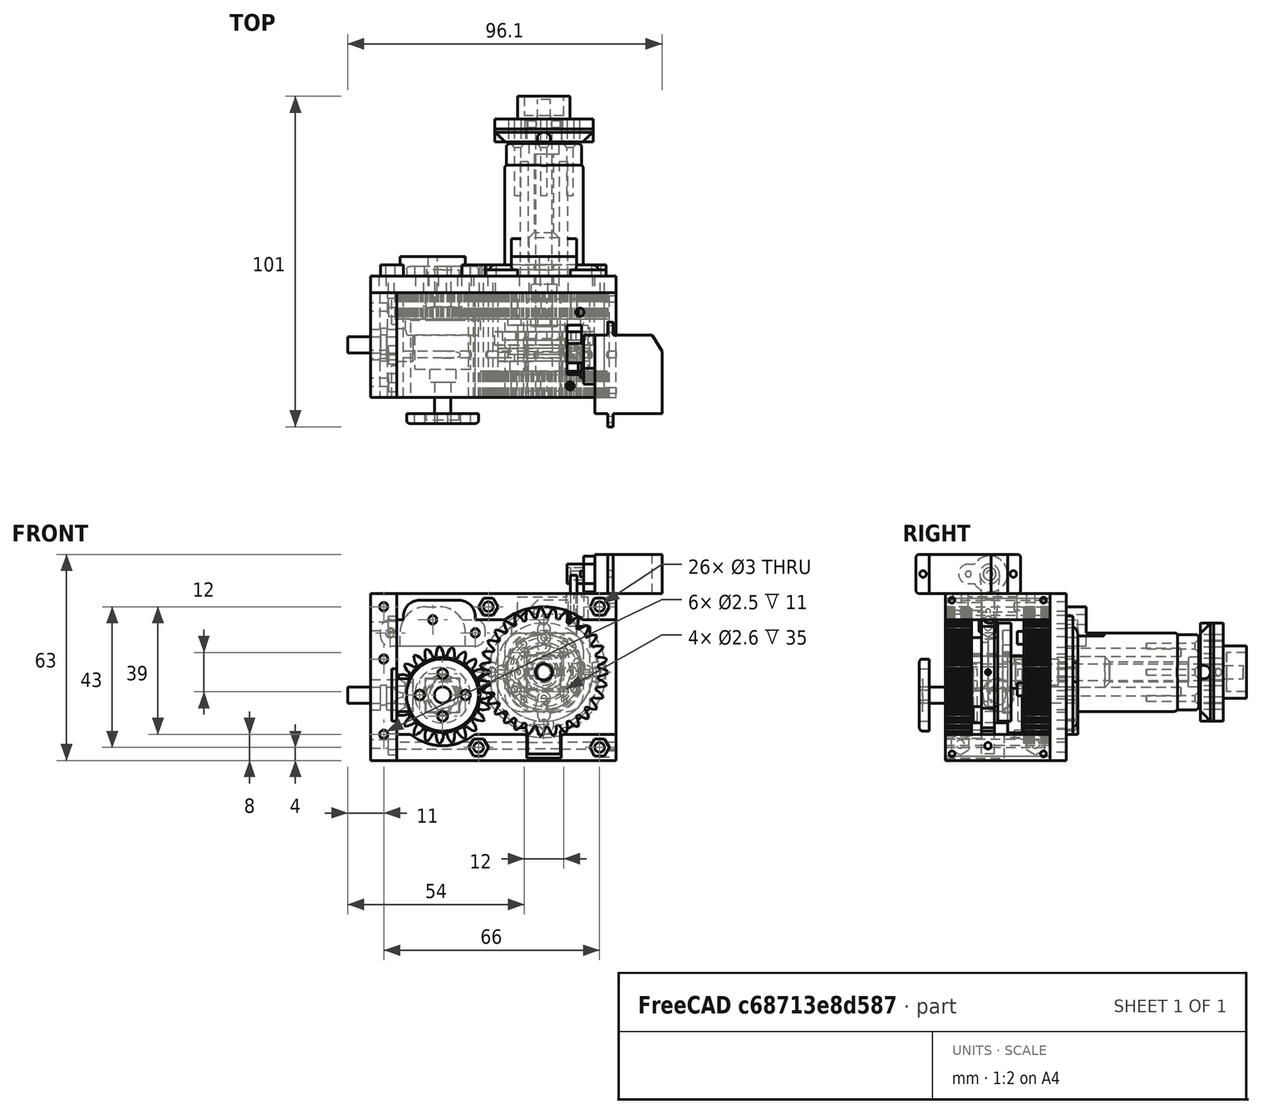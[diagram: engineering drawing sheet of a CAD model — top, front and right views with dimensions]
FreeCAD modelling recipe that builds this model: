
FCSTD DOCUMENT  (FreeCAD 0.20R)
Label: axles_00
License: Other
LicenseURL: https://www.gnu.org/licenses/gpl-3.0.en.html
objects: Part::Cylinder×477, Part::MultiFuse×208, Part::Cut×171, Part::Feature×154, Part::Box×150, Part::Chamfer×52, Part::Fillet×51, App::DocumentObjectGroup×23, Part::Part2DObjectPython×15, Part::Cone×7, Part::RegularPolygon×6, Part::Extrusion×6, Part::Compound×3, Part::Sphere×2, Mesh::Feature×2, Part::Mirroring×1
note: 1303 computed .brp shape members not serialized (recipe doc carries the construction recipe); baked Part::Feature solids carry a one-line shape summary decoded from their .brp

FEATURE [Part::Feature] Fusion017003004005003  label="rear-wheel-left"
  Placement = pos=(75,56,46) rot=(0,0,1;0rad)
  shape: bbox 96.33 x 28 x 96.33 mm, 456 faces (baked)
FEATURE [Part::Cylinder] Cylinder
  Angle = 360
  AttacherType = Attacher::AttachEngine3D
  FirstAngle = 0
  Height = 15
  Placement = pos=(0,0,-1) rot=(0,0,1;0rad)
  Radius = 8.5
  SecondAngle = 0
FEATURE [Part::Cylinder] Cylinder001
  Angle = 360
  AttacherType = Attacher::AttachEngine3D
  FirstAngle = 0
  Height = 4.5
  Placement = pos=(0,0,-1) rot=(0,0,1;0rad)
  Radius = 11.5
  SecondAngle = 0
FEATURE [Part::Cylinder] Cylinder002
  Angle = 360
  AttacherType = Attacher::AttachEngine3D
  FirstAngle = 0
  Height = 23
  Placement = pos=(0,0,-5) rot=(0,0,1;0rad)
  Radius = 4
  SecondAngle = 0
FEATURE [Part::Cylinder] Cylinder203
  Angle = 360
  AttacherType = Attacher::AttachEngine3D
  FirstAngle = 0
  Height = 5
  Placement = pos=(15,0,0) rot=(0,1,0;1.5708rad)
  Radius = 5
  SecondAngle = 0
FEATURE [Part::Cylinder] Cylinder204
  Angle = 360
  AttacherType = Attacher::AttachEngine3D
  FirstAngle = 0
  Height = 20
  Placement = pos=(0,0,0) rot=(0,1,0;1.5708rad)
  Radius = 2.5
  SecondAngle = 0
FEATURE [Part::MultiFuse] Fusion  label="differential"
  Placement = pos=(7.5,48,7.5) rot=(-1,0,0;1.5708rad)
  Refine = true
  Shapes = -> [Cylinder,Cylinder001,Cylinder002]
FEATURE [Part::MultiFuse] Fusion040  label="pinion"
  Placement = pos=(-21.5,54.5,7.5) rot=(0,0,1;0rad)
  Refine = true
  Shapes = -> [Cylinder204,Cylinder203]
FEATURE [Part::MultiFuse] Fusion041  label="differential+pinion"
  Placement = pos=(82.5,-54.5,53.5) rot=(0,1,0;3.14159rad)
  Refine = true
  Shapes = -> [Fusion,Fusion040]
FEATURE [Part::Part2DObjectPython] Line013  label="rear-wheels-axle-path"  # Draft 2D object (typed FeaturePython)
  Closed = true
  End = (75,75,46)
  FilletRadius = 0
  MapMode = 5
  Placement = pos=(75,-70,46) rot=(0,0,1;0rad)
  Points = (2) [(0,-5,0),(0,145,0)]
  Start = (75,-75,46)
FEATURE [Part::Box] Box153  label="Cube"
  AttacherType = Attacher::AttachEngine3D
  Height = 28
  Length = 24
  Placement = pos=(63,-20,32) rot=(0,0,1;0rad)
  Width = 40
FEATURE [Part::Cylinder] Cylinder406  label="Cylinder"
  Angle = 360
  AttacherType = Attacher::AttachEngine3D
  FirstAngle = 0
  Height = 48
  Placement = pos=(75,48,46) rot=(1,0,0;1.5708rad)
  Radius = 7.5
  SecondAngle = 0
FEATURE [Part::Cylinder] Cylinder407  label="Cylinder"
  Angle = 360
  AttacherType = Attacher::AttachEngine3D
  FirstAngle = 0
  Height = 39
  Placement = pos=(58,0,46) rot=(0,1,0;1.5708rad)
  Radius = 8.5
  SecondAngle = 0
FEATURE [Part::Feature] Compound001  label="joint-STEEL"
  Placement = pos=(0,-3,0) rot=(0,0,1;0rad)
  shape: bbox 11 x 24 x 40 mm, 54 faces (baked)
FEATURE [Part::Cylinder] Cylinder415  label="Cylinder"
  Angle = 360
  AttacherType = Attacher::AttachEngine3D
  FirstAngle = 0
  Height = 4
  Placement = pos=(75,69,46) rot=(1,0,0;1.5708rad)
  Radius = 7.5
  SecondAngle = 0
FEATURE [Part::Cylinder] Cylinder416  label="Cylinder"
  Angle = 360
  AttacherType = Attacher::AttachEngine3D
  FirstAngle = 0
  Height = 4
  Placement = pos=(75,69,46) rot=(1,0,0;1.5708rad)
  Radius = 5
  SecondAngle = 0
FEATURE [Part::Cut] Cut004026018020025012002  label="BEARING-10x15x4-6700"
  Base = -> Cylinder415
  Refine = true
  Tool = -> Cylinder416
FEATURE [Part::Feature] Fusion041001  label="differential+pinion"
  Placement = pos=(82.5,-54.5,53.5) rot=(0,1,0;3.14159rad)
  shape: bbox 40.5 x 23 x 23 mm, 14 faces (baked)
FEATURE [Part::Box] Box197  label="Cube197"
  AttacherType = Attacher::AttachEngine3D
  Height = 9.4
  Length = 9.8
  Placement = pos=(2.4,22.8,2.8) rot=(0,0,1;0rad)
  Width = 3.4
FEATURE [Part::Box] Box198  label="Cube198"
  AttacherType = Attacher::AttachEngine3D
  Height = 9.4
  Length = 9.8
  Placement = pos=(2.4,22.8,2.8) rot=(0,0,1;0rad)
  Width = 3.4
FEATURE [Part::Box] Box250  label="Cube250"
  AttacherType = Attacher::AttachEngine3D
  Height = 12.4
  Length = 12.8
  Placement = pos=(1.1,21.9,1.3) rot=(0,0,1;0rad)
  Width = 3.6
FEATURE [Part::Box] Box251  label="Cube251"
  AttacherType = Attacher::AttachEngine3D
  Height = 12.4
  Length = 12.8
  Placement = pos=(1.1,21.5,1.3) rot=(0,0,1;0rad)
  Width = 3.6
FEATURE [Part::Chamfer] Chamfer218  label="bearing_shape_031"
  Base = -> Box197
  Edges = 4 edges r=2.5: [Edge2,Edge4,Edge6,Edge8]
  Placement = pos=(-7.5,33.5,-7.5) rot=(0,0,1;0rad)
FEATURE [Part::Chamfer] Chamfer219  label="bearing_shape_032"
  Base = -> Box198
  Edges = 4 edges r=2.5: [Edge2,Edge4,Edge6,Edge8]
  Placement = pos=(-7.5,103.5,-7.5) rot=(0,0,1;0rad)
FEATURE [Part::Chamfer] Chamfer228008  label="bearing_shape_037"
  Base = -> Box251
  Edges = 4 edges r=3: [Edge2,Edge4,Edge6,Edge8]
  Placement = pos=(-7.5,79.5,-7.5) rot=(0,0,1;0rad)
FEATURE [Part::Chamfer] Chamfer228009  label="bearing_shape_038"
  Base = -> Box250
  Edges = 4 edges r=3: [Edge2,Edge4,Edge6,Edge8]
  Placement = pos=(-7.5,59.5,-7.5) rot=(0,0,1;0rad)
FEATURE [Part::Cylinder] Cylinder685
  Angle = 360
  AttacherType = Attacher::AttachEngine3D
  FirstAngle = 0
  Height = 16
  Placement = pos=(0,85,0) rot=(-1,0,0;1.5708rad)
  Radius = 12
  SecondAngle = 0
FEATURE [Part::Cylinder] Cylinder686
  Angle = 360
  AttacherType = Attacher::AttachEngine3D
  FirstAngle = 0
  Height = 5.5
  Placement = pos=(16,52,7.5) rot=(0,1,0;1.5708rad)
  Radius = 6
  SecondAngle = 0
FEATURE [Part::Cylinder] Cylinder687
  Angle = 360
  AttacherType = Attacher::AttachEngine3D
  FirstAngle = 0
  Height = 3
  Placement = pos=(21.5,52,7.5) rot=(0,1,0;1.5708rad)
  Radius = 4.7
  SecondAngle = 0
FEATURE [Part::Cylinder] Cylinder688
  Angle = 360
  AttacherType = Attacher::AttachEngine3D
  FirstAngle = 0
  Height = 3
  Placement = pos=(26.5,52,7.5) rot=(0,1,0;1.5708rad)
  Radius = 4.7
  SecondAngle = 0
FEATURE [Part::Cylinder] Cylinder689
  Angle = 360
  AttacherType = Attacher::AttachEngine3D
  FirstAngle = 0
  Height = 8
  Placement = pos=(21.5,52,7.5) rot=(0,1,0;1.5708rad)
  Radius = 3.2
  SecondAngle = 0
FEATURE [Part::Cylinder] Cylinder690
  Angle = 360
  AttacherType = Attacher::AttachEngine3D
  FirstAngle = 0
  Height = 3
  Placement = pos=(0,24,0) rot=(-1,0,0;1.5708rad)
  Radius = 4.6
  SecondAngle = 0
FEATURE [Part::Cylinder] Cylinder691
  Angle = 360
  AttacherType = Attacher::AttachEngine3D
  FirstAngle = 0
  Height = 3
  Placement = pos=(0,159,0) rot=(-1,0,0;1.5708rad)
  Radius = 4.6
  SecondAngle = 0
FEATURE [Part::Cylinder] Cylinder692
  Angle = 360
  AttacherType = Attacher::AttachEngine3D
  FirstAngle = 0
  Height = 138
  Placement = pos=(0,24,0) rot=(-1,0,0;1.5708rad)
  Radius = 3
  SecondAngle = 0
FEATURE [Part::MultiFuse] Fusion088026007031024007017  label="pinion-bearings-carving003"
  Placement = pos=(7.5,41,7.5) rot=(0,1,0;3.14159rad)
  Refine = true
  Shapes = -> [Cylinder686,Cylinder688,Cylinder689,Cylinder687]
FEATURE [Part::MultiFuse] Fusion088026007031024007008004058  label="inner-carving-rear"
  Placement = pos=(75,-93,46) rot=(0,1,0;3.14159rad)
  Refine = true
  Shapes = -> [Chamfer219,Chamfer218,Cylinder692,Fusion088026007031024007017,Chamfer228009,Chamfer228008,Cylinder685,Cylinder690,Cylinder691]
FEATURE [Part::Cylinder] Cylinder693  label="Cylinder"
  Angle = 360
  AttacherType = Attacher::AttachEngine3D
  FirstAngle = 0
  Height = 4
  Placement = pos=(75,69,46) rot=(1,0,0;1.5708rad)
  Radius = 11.5
  SecondAngle = 0
FEATURE [Part::Cylinder] Cylinder694  label="Cylinder"
  Angle = 360
  AttacherType = Attacher::AttachEngine3D
  FirstAngle = 0
  Height = 4
  Placement = pos=(75,69,46) rot=(1,0,0;1.5708rad)
  Radius = 8.5
  SecondAngle = 0
FEATURE [Part::Cut] Cut176013009033007019019008010045003002004008006021005002  label="BEARING-17x23x4-6703"
  Base = -> Cylinder693
  Refine = true
  Tool = -> Cylinder694
FEATURE [Part::Cylinder] Cylinder695  label="Cylinder"
  Angle = 360
  AttacherType = Attacher::AttachEngine3D
  FirstAngle = 0
  Height = 4
  Placement = pos=(75,69,46) rot=(1,0,0;1.5708rad)
  Radius = 13.5
  SecondAngle = 0
FEATURE [Part::Cylinder] Cylinder696  label="Cylinder"
  Angle = 360
  AttacherType = Attacher::AttachEngine3D
  FirstAngle = 0
  Height = 4
  Placement = pos=(75,69,46) rot=(1,0,0;1.5708rad)
  Radius = 10
  SecondAngle = 0
FEATURE [Part::Cut] Cut176013009033007019019008010045003002004008006021005003  label="BEARING-20x27x4-6704"
  Base = -> Cylinder695
  Refine = true
  Tool = -> Cylinder696
FEATURE [Part::Cylinder] Cylinder697  label="Cylinder"
  Angle = 360
  AttacherType = Attacher::AttachEngine3D
  FirstAngle = 0
  Height = 3
  Placement = pos=(75,69,46) rot=(1,0,0;1.5708rad)
  Radius = 4.5
  SecondAngle = 0
FEATURE [Part::Cylinder] Cylinder698  label="Cylinder"
  Angle = 360
  AttacherType = Attacher::AttachEngine3D
  FirstAngle = 0
  Height = 3
  Placement = pos=(75,69,46) rot=(1,0,0;1.5708rad)
  Radius = 2.5
  SecondAngle = 0
FEATURE [Part::Cut] Cut176013009033007019019008010045003002004008006021005004  label="BEARING-5x9x3-MR95ZZ"
  Base = -> Cylinder697
  Refine = true
  Tool = -> Cylinder698
FEATURE [Part::Cylinder] Cylinder699  label="Cylinder"
  Angle = 360
  AttacherType = Attacher::AttachEngine3D
  FirstAngle = 0
  Height = 3.5
  Placement = pos=(75,69,46) rot=(1,0,0;1.5708rad)
  Radius = 6
  SecondAngle = 0
FEATURE [Part::Cylinder] Cylinder700  label="Cylinder"
  Angle = 360
  AttacherType = Attacher::AttachEngine3D
  FirstAngle = 0
  Height = 3.5
  Placement = pos=(75,69,46) rot=(1,0,0;1.5708rad)
  Radius = 4
  SecondAngle = 0
FEATURE [Part::Cut] Cut176013009033007019019008010045003002004008006021005005  label="BEARING-8x12x3.5-MR128ZZ"
  Base = -> Cylinder699
  Refine = true
  Tool = -> Cylinder700
FEATURE [Part::Feature] Cut176013009033007019019008010045003002004008006021005004001  label="BEARING-5x9x3-MR95ZZ"
  Placement = pos=(0,-24.5,0) rot=(0,0,1;0rad)
  shape: bbox 9 x 3 x 9 mm, 4 faces (baked)
FEATURE [Part::Feature] Cut176013009033007019019008010045003002004008006021005004003  label="BEARING-5x9x3-MR95ZZ"
  Placement = pos=(0,-110.5,0) rot=(0,0,1;0rad)
  shape: bbox 9 x 3 x 9 mm, 4 faces (baked)
FEATURE [Part::Box] Box305  label="Cube"
  AttacherType = Attacher::AttachEngine3D
  Height = 11
  Length = 2
  Placement = pos=(-1,36,-5.5) rot=(0,0,1;0rad)
  Width = 6
FEATURE [Part::Cylinder] Cylinder828  label="Cylinder"
  Angle = 360
  AttacherType = Attacher::AttachEngine3D
  FirstAngle = 0
  Height = 3.5
  Placement = pos=(0,90,0) rot=(1,0,0;1.5708rad)
  Radius = 2
  SecondAngle = 0
FEATURE [Part::Cylinder] Cylinder830  label="Cylinder"
  Angle = 360
  AttacherType = Attacher::AttachEngine3D
  FirstAngle = 0
  Height = 38
  Placement = pos=(0,86.5,0) rot=(1,0,0;1.5708rad)
  Radius = 2.5
  SecondAngle = 0
FEATURE [Part::Cylinder] Cylinder831  label="Cylinder"
  Angle = 360
  AttacherType = Attacher::AttachEngine3D
  FirstAngle = 0
  Height = 0.5
  Placement = pos=(0,48.5,0) rot=(1,0,0;1.5708rad)
  Radius = 2
  SecondAngle = 0
FEATURE [Part::Cylinder] Cylinder832  label="Cylinder"
  Angle = 360
  AttacherType = Attacher::AttachEngine3D
  FirstAngle = 0
  Height = 2
  Placement = pos=(0,48,0) rot=(1,0,0;1.5708rad)
  Radius = 2.3
  SecondAngle = 0
FEATURE [Part::Cylinder] Cylinder833  label="Cylinder"
  Angle = 360
  AttacherType = Attacher::AttachEngine3D
  FirstAngle = 0
  Height = 6
  Placement = pos=(0,46,0) rot=(1,0,0;1.5708rad)
  Radius = 1.75
  SecondAngle = 0
FEATURE [Part::Cylinder] Cylinder834  label="Cylinder"
  Angle = 360
  AttacherType = Attacher::AttachEngine3D
  FirstAngle = 0
  Height = 11
  Placement = pos=(0,39.5,-5.5) rot=(0,0,1;1.5708rad)
  Radius = 1
  SecondAngle = 0
FEATURE [Part::Cylinder] Cylinder835  label="Cylinder"
  Angle = 360
  AttacherType = Attacher::AttachEngine3D
  FirstAngle = 0
  Height = 7
  Placement = pos=(0,41.5,0) rot=(1,0,0;1.5708rad)
  Radius = 5.5
  SecondAngle = 0
FEATURE [Part::Cylinder] Cylinder836  label="Cylinder"
  Angle = 360
  AttacherType = Attacher::AttachEngine3D
  FirstAngle = 0
  Height = 17
  Placement = pos=(0,41.5,0) rot=(1,0,0;1.5708rad)
  Radius = 2.5
  SecondAngle = 0
FEATURE [Part::Cylinder] Cylinder837  label="Cylinder"
  Angle = 360
  AttacherType = Attacher::AttachEngine3D
  FirstAngle = 0
  Height = 25
  Placement = pos=(0,41.5,0) rot=(1,0,0;1.5708rad)
  Radius = 2
  SecondAngle = 0
FEATURE [Part::Cylinder] Cylinder838  label="Cylinder"
  Angle = 360
  AttacherType = Attacher::AttachEngine3D
  FirstAngle = 0
  Height = 7
  Placement = pos=(0,41.5,0) rot=(1,0,0;1.5708rad)
  Radius = 4
  SecondAngle = 0
FEATURE [Part::MultiFuse] Fusion088026007031024007008004081022015  label="Fusion"
  Refine = true
  Shapes = -> [Cylinder837,Cylinder835,Cylinder836]
FEATURE [Part::Cut] Cut176013009033007019019008010045003002004008006021005009  label="Cut"
  Base = -> Fusion088026007031024007008004081022015
  Refine = true
  Tool = -> Cylinder838
FEATURE [Part::Chamfer] Chamfer228026
  Base = -> Cut176013009033007019019008010045003002004008006021005009
  Edges = 1 edges: [Edge4 r1=1 r2=3]
FEATURE [Part::Cut] Cut176013009033007019019008010045003002004008006021005010  label="wheel-axle-left"
  Base = -> Chamfer228026
  Placement = pos=(75,93,46) rot=(0,0,1;3.14159rad)
  Refine = true
  Tool = -> Box305
FEATURE [Part::Sphere] Sphere
  Angle1 = -90
  Angle2 = 90
  Angle3 = 360
  AttacherType = Attacher::AttachEngine3D
  Placement = pos=(0,39.5,0) rot=(0,0,1;0rad)
  Radius = 3
FEATURE [Part::MultiFuse] Fusion088026007031024007008004081022014  label="axle-shaft-left"
  Placement = pos=(75,93,46) rot=(0,0,1;3.14159rad)
  Refine = true
  Shapes = -> [Cylinder828,Cylinder830,Cylinder832,Cylinder831,Sphere,Cylinder833,Cylinder834]
FEATURE [Part::Part2DObjectPython] Line015  label="rear-axle-steering-point-left"  # Draft 2D object (typed FeaturePython)
  Closed = true
  End = (75,53.5,26)
  FilletRadius = 0
  MapMode = 5
  Placement = pos=(75,-86,42) rot=(0,0,1;0rad)
  Points = (2) [(0,139.5,24),(0,139.5,-16)]
  Start = (75,53.5,66)
FEATURE [Part::Sphere] Sphere001  label="Sphere"
  Angle1 = -90
  Angle2 = 90
  Angle3 = 360
  AttacherType = Attacher::AttachEngine3D
  Placement = pos=(75,54,46) rot=(0,0,1;0rad)
  Radius = 10
FEATURE [Part::MultiFuse] Fusion088026007031024007008004100051009001002  label="Fusion"
  Refine = true
  Shapes = -> [Cylinder406,Sphere001]
FEATURE [Part::Cylinder] Cylinder840  label="Cylinder"
  Angle = 360
  AttacherType = Attacher::AttachEngine3D
  FirstAngle = 0
  Height = 24
  Placement = pos=(75,66,46) rot=(1,0,0;1.5708rad)
  Radius = 6
  SecondAngle = 0
FEATURE [Part::Cylinder] Cylinder841  label="Cylinder"
  Angle = 360
  AttacherType = Attacher::AttachEngine3D
  FirstAngle = 0
  Height = 10
  Placement = pos=(75,66,46) rot=(1,0,0;1.5708rad)
  Radius = 11
  SecondAngle = 0
FEATURE [Part::Box] Box306  label="Cube"
  AttacherType = Attacher::AttachEngine3D
  Height = 14
  Length = 22
  Placement = pos=(56,54,39) rot=(0,0,1;0rad)
  Width = 12
FEATURE [Part::Fillet] Fillet
  Base = -> Box306
  Edges = 2 edges r=6.5: [Edge9,Edge10]
  Placement = pos=(5,-2,0) rot=(0,0,1;0rad)
FEATURE [Part::Cylinder] Cylinder842  label="Cylinder"
  Angle = 360
  AttacherType = Attacher::AttachEngine3D
  FirstAngle = 0
  Height = 15
  Placement = pos=(75,66,46) rot=(1,0,0;1.5708rad)
  Radius = 7
  SecondAngle = 0
FEATURE [Part::MultiFuse] Fusion088026007031024007008004100051009001003  label="Fusion"
  Refine = true
  Shapes = -> [Cylinder842,Cylinder841,Cylinder840]
FEATURE [Part::Cut] Cut176013009033007019019008010045003002004008006021005004004004002  label="Cut"
  Base = -> Fusion088026007031024007008004100051009001002
  Refine = true
  Tool = -> Fusion088026007031024007008004100051009001003
FEATURE [Part::Fillet] Fillet113
  Base = -> Fillet
  Edges = 4 edges r=5: [Edge2,Edge6,Edge11,Edge13]
  Placement = pos=(3,0,0) rot=(0,0,1;0rad)
FEATURE [Part::Cut] Cut176013009033007019019008010045003002004008006021005004004004003  label="Cut"
  Base = -> Cut176013009033007019019008010045003002004008006021005004004004002
  Refine = true
  Tool = -> Fillet113
FEATURE [Part::Box] Box278  label="Cube277"
  AttacherType = Attacher::AttachEngine3D
  Height = 5.4
  Length = 28
  Placement = pos=(-14,24,-13) rot=(0,0,1;0rad)
  Width = 20
FEATURE [Part::Box] Box279  label="Cube278"
  AttacherType = Attacher::AttachEngine3D
  Height = 5.4
  Length = 28
  Placement = pos=(-14,24,7.6) rot=(0,0,1;0rad)
  Width = 20
FEATURE [Part::Box] Box280  label="Cube279"
  AttacherType = Attacher::AttachEngine3D
  Height = 16
  Length = 20
  Placement = pos=(-10,48,-8) rot=(0,0,1;0rad)
  Width = 12
FEATURE [Part::Box] Box284  label="Cube283"
  AttacherType = Attacher::AttachEngine3D
  Height = 4
  Length = 18
  Placement = pos=(12.75,26,-2) rot=(0,0,1;1.26536rad)
  Width = 6
FEATURE [Part::Box] Box289  label="Cube288"
  AttacherType = Attacher::AttachEngine3D
  Height = 4
  Length = 7.2
  Placement = pos=(5.8,24,-2) rot=(0,0,1;0rad)
  Width = 12
FEATURE [Part::Box] Box290  label="Cube289"
  AttacherType = Attacher::AttachEngine3D
  Height = 4.4
  Length = 7.5
  Placement = pos=(5.7,24,-2.2) rot=(0,0,1;0rad)
  Width = 12
FEATURE [Part::Feature] Cut176013009033007019019008010045003002004002001  label="steering-knukle-body-left001"
  Placement = pos=(0,0.5,0) rot=(0,0,1;0rad)
  shape: bbox 25.81 x 12 x 15.2 mm, 30 faces (baked)
FEATURE [Part::Cylinder] Cylinder749
  Angle = 360
  AttacherType = Attacher::AttachEngine3D
  FirstAngle = 0
  Height = 6
  Placement = pos=(14.35,41,-3) rot=(0,0,1;0rad)
  Radius = 1.25
  SecondAngle = 0
FEATURE [Part::Cylinder] Cylinder752
  Angle = 360
  AttacherType = Attacher::AttachEngine3D
  FirstAngle = 0
  Height = 12
  Placement = pos=(0,24,0) rot=(-1,0,0;1.5708rad)
  Radius = 13
  SecondAngle = 0
FEATURE [Part::Cylinder] Cylinder753
  Angle = 360
  AttacherType = Attacher::AttachEngine3D
  FirstAngle = 0
  Height = 3.2
  Placement = pos=(0,24,0) rot=(-1,0,0;1.5708rad)
  Radius = 4.7
  SecondAngle = 0
FEATURE [Part::Cylinder] Cylinder754
  Angle = 360
  AttacherType = Attacher::AttachEngine3D
  FirstAngle = 0
  Height = 8
  Placement = pos=(0,34,0) rot=(-1,0,0;1.5708rad)
  Radius = 6.1
  SecondAngle = 0
FEATURE [Part::Cylinder] Cylinder755
  Angle = 360
  AttacherType = Attacher::AttachEngine3D
  FirstAngle = 0
  Height = 3.2
  Placement = pos=(0,30.8,0) rot=(-1,0,0;1.5708rad)
  Radius = 4.7
  SecondAngle = 0
FEATURE [Part::Cylinder] Cylinder756
  Angle = 360
  AttacherType = Attacher::AttachEngine3D
  FirstAngle = 0
  Height = 4
  Placement = pos=(0,27,0) rot=(-1,0,0;1.5708rad)
  Radius = 3.5
  SecondAngle = 0
FEATURE [Part::Cylinder] Cylinder788
  Angle = 360
  AttacherType = Attacher::AttachEngine3D
  FirstAngle = 0
  Height = 37
  Placement = pos=(-8,27.5,-19) rot=(0,0,1;0rad)
  Radius = 1.05
  SecondAngle = 0
FEATURE [Part::Cylinder] Cylinder789
  Angle = 360
  AttacherType = Attacher::AttachEngine3D
  FirstAngle = 0
  Height = 37
  Placement = pos=(8,33,-19) rot=(0,0,1;0rad)
  Radius = 1.05
  SecondAngle = 0
FEATURE [Part::Cylinder] Cylinder790
  Angle = 360
  AttacherType = Attacher::AttachEngine3D
  FirstAngle = 0
  Height = 37
  Placement = pos=(-8,33,-19) rot=(0,0,1;0rad)
  Radius = 1.05
  SecondAngle = 0
FEATURE [Part::Cylinder] Cylinder791
  Angle = 360
  AttacherType = Attacher::AttachEngine3D
  FirstAngle = 0
  Height = 37
  Placement = pos=(8,27.5,-19) rot=(0,0,1;0rad)
  Radius = 1.05
  SecondAngle = 0
FEATURE [Part::Cylinder] Cylinder792
  Angle = 360
  AttacherType = Attacher::AttachEngine3D
  FirstAngle = 0
  Height = 8
  Placement = pos=(0,34,0) rot=(-1,0,0;1.5708rad)
  Radius = 6.1
  SecondAngle = 0
FEATURE [Part::Cylinder] Cylinder810
  Angle = 360
  AttacherType = Attacher::AttachEngine3D
  FirstAngle = 0
  Height = 15.2
  Placement = pos=(-8,27.5,-7.6) rot=(0,0,1;0rad)
  Radius = 1.6
  SecondAngle = 0
FEATURE [Part::Cylinder] Cylinder812
  Angle = 360
  AttacherType = Attacher::AttachEngine3D
  FirstAngle = 0
  Height = 15.2
  Placement = pos=(-8,33,-7.6) rot=(0,0,1;0rad)
  Radius = 1.6
  SecondAngle = 0
FEATURE [Part::Cylinder] Cylinder813
  Angle = 360
  AttacherType = Attacher::AttachEngine3D
  FirstAngle = 0
  Height = 5.4
  Placement = pos=(8,27.5,-7.6) rot=(0,0,1;0rad)
  Radius = 1.6
  SecondAngle = 0
FEATURE [Part::Cylinder] Cylinder814
  Angle = 360
  AttacherType = Attacher::AttachEngine3D
  FirstAngle = 0
  Height = 5.4
  Placement = pos=(8,33,-7.6) rot=(0,0,1;0rad)
  Radius = 1.6
  SecondAngle = 0
FEATURE [Part::Cylinder] Cylinder815
  Angle = 360
  AttacherType = Attacher::AttachEngine3D
  FirstAngle = 0
  Height = 5.4
  Placement = pos=(8,27.5,2.2) rot=(0,0,1;0rad)
  Radius = 1.1
  SecondAngle = 0
FEATURE [Part::Cylinder] Cylinder816
  Angle = 360
  AttacherType = Attacher::AttachEngine3D
  FirstAngle = 0
  Height = 5.4
  Placement = pos=(8,33,2.2) rot=(0,0,1;0rad)
  Radius = 1.1
  SecondAngle = 0
FEATURE [Part::Fillet] Fillet125007020018
  Base = -> Box280
  Edges = 2 edges r=6: [Edge1,Edge5]
  Placement = pos=(0,-13,0) rot=(0,0,1;0rad)
FEATURE [Part::Fillet] Fillet125007020021
  Base = -> Box284
  Edges = 2 edges r=2.99: [Edge5,Edge7]
FEATURE [Part::MultiFuse] Fusion088026007031024007008004072  label="Fusion"
  Refine = true
  Shapes = -> [Box279,Box278]
FEATURE [Part::MultiFuse] Fusion088026007031024007008004081003  label="Fusion"
  Refine = true
  Shapes = -> [Cylinder754,Cylinder753,Cylinder755,Cylinder756]
FEATURE [Part::Cut] Cut176013009033007019019008010030  label="Cut"
  Base = -> Cylinder752
  Refine = true
  Tool = -> Fusion088026007031024007008004081003
FEATURE [Part::Cut] Cut176013009033007019019008010039  label="Cut"
  Base = -> Cut176013009033007019019008010030
  Refine = true
  Tool = -> Fusion088026007031024007008004072
FEATURE [Part::Cut] Cut176013009033007019019008010040  label="Cut"
  Base = -> Cut176013009033007019019008010039
  Refine = true
  Tool = -> Fillet125007020018
FEATURE [Part::Cut] Cut176013009033007019019008010041  label="Cut"
  Base = -> Cut176013009033007019019008010040
  Refine = true
  Tool = -> Box290
FEATURE [Part::MultiFuse] Fusion088026007031024007008004081010
  Refine = true
  Shapes = -> [Fillet125007020021,Box289]
FEATURE [Part::MultiFuse] Fusion088026007031024007008004081011
  Refine = true
  Shapes = -> [Cylinder788,Cylinder789,Cylinder790,Cylinder791]
FEATURE [Part::Cut] Cut176013009033007019019008010043
  Base = -> Fusion088026007031024007008004081010
  Refine = true
  Tool = -> Fusion088026007031024007008004081011
FEATURE [Part::Chamfer] Chamfer228022
  Base = -> Cut176013009033007019019008010043
  Edges = 1 edges: [Edge3 r1=0.75 r2=1.5]
FEATURE [Part::Cut] Cut176013009033007019019008010044  label="Cut"
  Base = -> Chamfer228022
  Refine = true
  Tool = -> Cylinder792
FEATURE [Part::Cut] Cut176013009033007019019008010045  label="rear-axle-steering-knukle-arm-right-ALU4mm.BAK"
  Base = -> Cut176013009033007019019008010044
  Placement = pos=(75,-93,46) rot=(0,0,1;0rad)
  Refine = true
  Tool = -> Cylinder749
FEATURE [Part::MultiFuse] Fusion088026007031024007008004081018  label="Fusion"
  Refine = true
  Shapes = -> [Cylinder810,Cylinder812,Cylinder813,Cylinder814,Cylinder815,Cylinder816]
FEATURE [Part::Cut] Cut176013009033007019019008010045003002004002  label="rear-axle-steering-knukle-body-right"
  Base = -> Cut176013009033007019019008010041
  Placement = pos=(75,-92.5,46) rot=(0,0,1;0rad)
  Refine = true
  Tool = -> Fusion088026007031024007008004081018
FEATURE [Part::Mirroring] Part__Mirroring007002003002002  label="rear-axle-steering-knukle-body-left"
  Base = (0,0,0)
  Normal = (0,1,0)
  Placement = pos=(75,93,46) rot=(0,0,1;0rad)
  Source = -> Cut176013009033007019019008010045003002004002001
FEATURE [Part::Part2DObjectPython] Line016  label="rear-axle-steering-point-right"  # Draft 2D object (typed FeaturePython)
  Closed = true
  End = (75,-53.5,26)
  FilletRadius = 0
  MapMode = 5
  Placement = pos=(75,-86,42) rot=(0,0,1;0rad)
  Points = (2) [(0,32.5,24),(0,32.5,-16)]
  Start = (75,-53.5,66)
FEATURE [Part::Box] Box201  label="Cube201"
  AttacherType = Attacher::AttachEngine3D
  Height = 12.4
  Length = 12.8
  Placement = pos=(1.1,21.7,1.3) rot=(0,0,1;0rad)
  Width = 3.8
FEATURE [Part::Box] Box202  label="Cube202"
  AttacherType = Attacher::AttachEngine3D
  Height = 12.4
  Length = 12.8
  Placement = pos=(1.1,21.5,1.3) rot=(0,0,1;0rad)
  Width = 3.8
FEATURE [Part::Chamfer] Chamfer228002  label="bearing_shape_035"
  Base = -> Box201
  Edges = 4 edges r=3: [Edge2,Edge4,Edge6,Edge8]
  Placement = pos=(-7.5,59.5,-7.5) rot=(0,0,1;0rad)
FEATURE [Part::Chamfer] Chamfer228003  label="bearing_shape_036"
  Base = -> Box202
  Edges = 4 edges r=3: [Edge2,Edge4,Edge6,Edge8]
  Placement = pos=(-7.5,79.5,-7.5) rot=(0,0,1;0rad)
FEATURE [Part::Cylinder] Cylinder601
  Angle = 360
  AttacherType = Attacher::AttachEngine3D
  FirstAngle = 0
  Height = 3
  Placement = pos=(-14.5,52,7.5) rot=(0,1,0;1.5708rad)
  Radius = 4.75
  SecondAngle = 0
FEATURE [Part::Cylinder] Cylinder602
  Angle = 360
  AttacherType = Attacher::AttachEngine3D
  FirstAngle = 0
  Height = 8
  Placement = pos=(-14.5,52,7.5) rot=(0,1,0;1.5708rad)
  Radius = 3.2
  SecondAngle = 0
FEATURE [Part::Cylinder] Cylinder603
  Angle = 360
  AttacherType = Attacher::AttachEngine3D
  FirstAngle = 0
  Height = 5.5
  Placement = pos=(-6.5,52,7.5) rot=(0,1,0;1.5708rad)
  Radius = 7
  SecondAngle = 0
FEATURE [Part::Cylinder] Cylinder604
  Angle = 360
  AttacherType = Attacher::AttachEngine3D
  FirstAngle = 0
  Height = 3.2
  Placement = pos=(-9.7,52,7.5) rot=(0,1,0;1.5708rad)
  Radius = 4.8
  SecondAngle = 0
FEATURE [Part::Cylinder] Cylinder616
  Angle = 360
  AttacherType = Attacher::AttachEngine3D
  FirstAngle = 0
  Height = 16
  Placement = pos=(0,85,0) rot=(-1,0,0;1.5708rad)
  Radius = 12
  SecondAngle = 0
FEATURE [Part::Cylinder] Cylinder620
  Angle = 360
  AttacherType = Attacher::AttachEngine3D
  FirstAngle = 0
  Height = 3.3
  Placement = pos=(0,48.5,0) rot=(-1,0,0;1.5708rad)
  Radius = 4.6
  SecondAngle = 0
FEATURE [Part::Cylinder] Cylinder621
  Angle = 360
  AttacherType = Attacher::AttachEngine3D
  FirstAngle = 0
  Height = 3.2
  Placement = pos=(0,134.3,0) rot=(-1,0,0;1.5708rad)
  Radius = 4.6
  SecondAngle = 0
FEATURE [Part::Cylinder] Cylinder622
  Angle = 360
  AttacherType = Attacher::AttachEngine3D
  FirstAngle = 0
  Height = 89
  Placement = pos=(0,48.5,0) rot=(-1,0,0;1.5708rad)
  Radius = 3
  SecondAngle = 0
FEATURE [Part::MultiFuse] Fusion247  label="pinion-bearings-carving002"
  Placement = pos=(7.5,41,7.5) rot=(0,1,0;3.14159rad)
  Refine = true
  Shapes = -> [Cylinder603,Cylinder601,Cylinder602,Cylinder604]
FEATURE [Part::MultiFuse] Fusion088026007031024007008004081019  label="inner-carving-rear"
  Placement = pos=(75,-93,46) rot=(0,0,1;0rad)
  Refine = true
  Shapes = -> [Cylinder622,Chamfer228002,Fusion247,Chamfer228003,Cylinder616,Cylinder620,Cylinder621]
FEATURE [Part::Cylinder] Cylinder843  label="Cylinder"
  Angle = 360
  AttacherType = Attacher::AttachEngine3D
  FirstAngle = 0
  Height = 89
  Placement = pos=(75,44.5,46) rot=(1,0,0;1.5708rad)
  Radius = 9
  SecondAngle = 0
FEATURE [Part::Fillet] Fillet125007020032008
  Base = -> Box153
  Edges = 4 edges r=12: [Edge9,Edge10,Edge11,Edge12]
FEATURE [Part::Fillet] Fillet125007020032009
  Base = -> Fillet125007020032008
  Edges = 8 edges r=7: [Edge2,Edge4,Edge6,Edge8,Edge13,Edge15,Edge20,Edge22]
FEATURE [Part::MultiFuse] Fusion088026007031024007008004100051009001004  label="Fusion-0001"
  Refine = true
  Shapes = -> [Cylinder407,Fillet125007020032009]
FEATURE [Part::MultiFuse] Fusion088026007031024007008004100051009001005  label="Fusion-0002"
  Refine = true
  Shapes = -> [Fusion088026007031024007008004100051009001004,Cylinder843]
FEATURE [Part::Box] Box307  label="Cube"
  AttacherType = Attacher::AttachEngine3D
  Height = 3.5
  Length = 18
  Placement = pos=(66,32.5,51.5) rot=(0,0,1;0rad)
  Width = 12
FEATURE [Part::Box] Box308  label="Cube"
  AttacherType = Attacher::AttachEngine3D
  Height = 3.5
  Length = 18
  Placement = pos=(66,32.5,37) rot=(0,0,1;0rad)
  Width = 12
FEATURE [Part::Box] Box309  label="Cube"
  AttacherType = Attacher::AttachEngine3D
  Height = 3.5
  Length = 18
  Placement = pos=(66,-44.5,37) rot=(0,0,1;0rad)
  Width = 12
FEATURE [Part::Box] Box310  label="Cube"
  AttacherType = Attacher::AttachEngine3D
  Height = 3.5
  Length = 18
  Placement = pos=(66,-44.5,51.5) rot=(0,0,1;0rad)
  Width = 12
FEATURE [Part::MultiFuse] Fusion088026007031024007008004100051009001006  label="Fusion-0002"
  Refine = true
  Shapes = -> [Box310,Box307,Box308,Box309]
FEATURE [Part::Cut] Cut176013009033007019019008010045003002004008006021005004004004004  label="rear-axle-base-01"
  Base = -> Fusion088026007031024007008004100051009001005
  Refine = true
  Tool = -> Fusion088026007031024007008004100051009001006
FEATURE [Part::Box] Box311  label="Cube290"
  AttacherType = Attacher::AttachEngine3D
  Height = 4
  Length = 19
  Placement = pos=(13,27,-2) rot=(0,0,1;0.802851rad)
  Width = 8.5
FEATURE [Part::Box] Box312  label="Cube291"
  AttacherType = Attacher::AttachEngine3D
  Height = 4
  Length = 7.2
  Placement = pos=(5.8,24,-2) rot=(0,0,1;0rad)
  Width = 12
FEATURE [Part::Cylinder] Cylinder844
  Angle = 360
  AttacherType = Attacher::AttachEngine3D
  FirstAngle = 0
  Height = 6
  Placement = pos=(26.25,42.75,-3) rot=(0,0,1;0rad)
  Radius = 1.25
  SecondAngle = 0
FEATURE [Part::Cylinder] Cylinder845
  Angle = 360
  AttacherType = Attacher::AttachEngine3D
  FirstAngle = 0
  Height = 37
  Placement = pos=(-8,27.5,-19) rot=(0,0,1;0rad)
  Radius = 1.05
  SecondAngle = 0
FEATURE [Part::Cylinder] Cylinder846
  Angle = 360
  AttacherType = Attacher::AttachEngine3D
  FirstAngle = 0
  Height = 37
  Placement = pos=(8,27.5,-19) rot=(0,0,1;0rad)
  Radius = 1.05
  SecondAngle = 0
FEATURE [Part::Cylinder] Cylinder847
  Angle = 360
  AttacherType = Attacher::AttachEngine3D
  FirstAngle = 0
  Height = 37
  Placement = pos=(-8,33,-19) rot=(0,0,1;0rad)
  Radius = 1.05
  SecondAngle = 0
FEATURE [Part::Cylinder] Cylinder848
  Angle = 360
  AttacherType = Attacher::AttachEngine3D
  FirstAngle = 0
  Height = 37
  Placement = pos=(8,33,-19) rot=(0,0,1;0rad)
  Radius = 1.05
  SecondAngle = 0
FEATURE [Part::Cylinder] Cylinder849
  Angle = 360
  AttacherType = Attacher::AttachEngine3D
  FirstAngle = 0
  Height = 8
  Placement = pos=(0,34,0) rot=(-1,0,0;1.5708rad)
  Radius = 6.1
  SecondAngle = 0
FEATURE [Part::MultiFuse] Fusion088026007031024007008004100051009001008  label="Fusion-0003"
  Refine = true
  Shapes = -> [Cylinder845,Cylinder848,Cylinder847,Cylinder846]
FEATURE [Part::Box] Box313  label="Cube292"
  AttacherType = Attacher::AttachEngine3D
  Height = 4
  Length = 10
  Placement = pos=(20,39.25,-2) rot=(0,0,1;0rad)
  Width = 7
FEATURE [Part::Box] Box314  label="Cube293"
  AttacherType = Attacher::AttachEngine3D
  Height = 4
  Length = 12
  Placement = pos=(14,46.25,-2) rot=(0,0,1;0rad)
  Width = 7
FEATURE [Part::Feature] Fusion088026007031024007008004100051009001010  label="rear-wheel-right"
  Placement = pos=(75,-84,46) rot=(0,0,1;0rad)
  shape: bbox 96.33 x 28 x 96.33 mm, 456 faces (baked)
FEATURE [Part::MultiFuse] Fusion088026007031024007008004100051009001011  label="Fusion"
  Refine = true
  Shapes = -> [Box311,Box312,Box313]
FEATURE [Part::Cut] Cut176013009033007019019008010045003002004008006021005004004004005  label="Cut"
  Base = -> Fusion088026007031024007008004100051009001011
  Refine = true
  Tool = -> Box314
FEATURE [Part::Cut] Cut176013009033007019019008010045003002004008006021005004004004006  label="Cut"
  Base = -> Cut176013009033007019019008010045003002004008006021005004004004005
  Refine = true
  Tool = -> Fusion088026007031024007008004100051009001008
FEATURE [Part::Fillet] Fillet125007020032010
  Base = -> Cut176013009033007019019008010045003002004008006021005004004004006
  Edges = 2 edges r=3: [Edge30,Edge31]
FEATURE [Part::Chamfer] Chamfer
  Base = -> Fillet125007020032010
  Edges = 1 edges: [Edge16 r1=2 r2=10]
FEATURE [Part::Fillet] Fillet125007020032011
  Base = -> Chamfer
  Edges = 2 edges r=3: [Edge17,Edge19]
FEATURE [Part::Chamfer] Chamfer228027
  Base = -> Fillet125007020032011
  Edges = 1 edges: [Edge37 r1=1.5 r2=0.75]
FEATURE [Part::Cut] Cut176013009033007019019008010045003002004008006021005004004004007  label="Cut"
  Base = -> Chamfer228027
  Refine = true
  Tool = -> Cylinder849
FEATURE [Part::Cut] Cut176013009033007019019008010045003002004008006021005004004004008  label="rear-axle-steering-knukle-arm-right-ALU4mm"
  Base = -> Cut176013009033007019019008010045003002004008006021005004004004007
  Placement = pos=(75,-92.5,46) rot=(0,0,1;0rad)
  Refine = true
  Tool = -> Cylinder844
FEATURE [Part::Feature] Cut176013009033007019019008010045003002004008006021005004004004004002004  label="BEARING-5x9x3-MR95ZZ"
  Placement = pos=(0,-0.5,0) rot=(0,0,1;0rad)
  shape: bbox 9 x 3 x 9 mm, 4 faces (baked)
FEATURE [Part::Feature] Cut176013009033007019019008010045003002004008006021005004004004004002005  label="BEARING-5x9x3-MR95ZZ"
  Placement = pos=(0,-7.5,0) rot=(0,0,1;0rad)
  shape: bbox 9 x 3 x 9 mm, 4 faces (baked)
FEATURE [Part::Feature] Cut176013009033007019019008010045003002004008006021005004004004004002006  label="BEARING-5x9x3-MR95ZZ"
  Placement = pos=(0,-134.5,0) rot=(0,0,1;0rad)
  shape: bbox 9 x 3 x 9 mm, 4 faces (baked)
FEATURE [Part::Feature] Cut176013009033007019019008010045003002004008006021005004004004004002007  label="BEARING-5x9x3-MR95ZZ"
  Placement = pos=(0,-127.5,0) rot=(0,0,1;0rad)
  shape: bbox 9 x 3 x 9 mm, 4 faces (baked)
FEATURE [Part::Feature] Cut176013009033007019019008010045003002004008006021005005001  label="BEARING-8x12x3.5-MR128ZZ"
  Placement = pos=(0,-57.5,0) rot=(0,0,1;0rad)
  shape: bbox 12 x 3.5 x 12 mm, 4 faces (baked)
FEATURE [Part::Feature] Cut176013009033007019019008010045003002004008006021005004004004004002008  label="BEARING-8x12x3.5-MR128ZZ"
  Placement = pos=(0,-77,0) rot=(0,0,1;0rad)
  shape: bbox 12 x 3.5 x 12 mm, 4 faces (baked)
FEATURE [Part::Cylinder] Cylinder850  label="Cylinder"
  Angle = 360
  AttacherType = Attacher::AttachEngine3D
  FirstAngle = 0
  Height = 14
  Placement = pos=(0,0,0) rot=(0,1,0;1.5708rad)
  Radius = 0.8
  SecondAngle = 0
FEATURE [Part::Cylinder] Cylinder851  label="Cylinder"
  Angle = 360
  AttacherType = Attacher::AttachEngine3D
  FirstAngle = 0
  Height = 7
  Placement = pos=(0,0,0) rot=(0,1,0;1.5708rad)
  Radius = 1.2
  SecondAngle = 0
FEATURE [Part::Cylinder] Cylinder852  label="Cylinder"
  Angle = 360
  AttacherType = Attacher::AttachEngine3D
  FirstAngle = 0
  Height = 2
  Placement = pos=(-2,0,0) rot=(0,1,0;1.5708rad)
  Radius = 1.8
  SecondAngle = 0
FEATURE [Part::MultiFuse] Fusion088026007031024007008004100051009001012  label="SCREW-S-T-M2x14"
  Refine = true
  Shapes = -> [Cylinder850,Cylinder851,Cylinder852]
FEATURE [Part::Cylinder] Cylinder853  label="Cylinder"
  Angle = 360
  AttacherType = Attacher::AttachEngine3D
  FirstAngle = 0
  Height = 10
  Placement = pos=(0,0,0) rot=(0,1,0;1.5708rad)
  Radius = 0.8
  SecondAngle = 0
FEATURE [Part::Cylinder] Cylinder854  label="Cylinder"
  Angle = 360
  AttacherType = Attacher::AttachEngine3D
  FirstAngle = 0
  Height = 5
  Placement = pos=(0,0,0) rot=(0,1,0;1.5708rad)
  Radius = 1.2
  SecondAngle = 0
FEATURE [Part::Cylinder] Cylinder855  label="Cylinder"
  Angle = 360
  AttacherType = Attacher::AttachEngine3D
  FirstAngle = 0
  Height = 2
  Placement = pos=(-2,0,0) rot=(0,1,0;1.5708rad)
  Radius = 1.8
  SecondAngle = 0
FEATURE [Part::MultiFuse] Fusion088026007031024007008004100051009001012005  label="SCREW-S-T-M2x10"
  Refine = true
  Shapes = -> [Cylinder853,Cylinder854,Cylinder855]
FEATURE [Part::Feature] Fusion088026007031024007008004100051009001012006001  label="SCREW-S-T-M2x014"
  Placement = pos=(68,12,56) rot=(0,0,1;0rad)
  shape: bbox 19 x 4 x 4 mm, 7 faces (baked)
FEATURE [Part::Feature] Fusion088026007031024007008004100051009001012006002  label="SCREW-S-T-M2x014"
  Placement = pos=(68,-12,56) rot=(0,0,1;0rad)
  shape: bbox 19 x 4 x 4 mm, 7 faces (baked)
FEATURE [Part::Feature] Fusion088026007031024007008004100051009001012006003  label="SCREW-S-T-M2x014"
  Placement = pos=(68,-12,36) rot=(0,0,1;0rad)
  shape: bbox 19 x 4 x 4 mm, 7 faces (baked)
FEATURE [Part::Feature] Fusion088026007031024007008004100051009001012006004  label="SCREW-S-T-M2x014"
  Placement = pos=(68,12,36) rot=(0,0,1;0rad)
  shape: bbox 19 x 4 x 4 mm, 7 faces (baked)
FEATURE [Part::Feature] Fusion088026007031024007008004100051009001012006005001  label="SCREW-S-T-M2x10"
  Placement = pos=(70,29,51.75) rot=(0,0,1;0rad)
  shape: bbox 15 x 3.6 x 3.6 mm, 7 faces (baked)
FEATURE [Part::Feature] Fusion088026007031024007008004100051009001012006005002  label="SCREW-S-T-M2x10"
  Placement = pos=(70,29,40.25) rot=(0,0,1;0rad)
  shape: bbox 15 x 3.6 x 3.6 mm, 7 faces (baked)
FEATURE [Part::Feature] Fusion088026007031024007008004100051009001012006005003  label="SCREW-S-T-M2x10"
  Placement = pos=(70,-29,40.25) rot=(0,0,1;0rad)
  shape: bbox 15 x 3.6 x 3.6 mm, 7 faces (baked)
FEATURE [Part::Feature] Fusion088026007031024007008004100051009001012006005004  label="SCREW-S-T-M2x10"
  Placement = pos=(70,-29,51.75) rot=(0,0,1;0rad)
  shape: bbox 15 x 3.6 x 3.6 mm, 7 faces (baked)
FEATURE [Part::Cylinder] Cylinder856  label="Cylinder"
  Angle = 360
  AttacherType = Attacher::AttachEngine3D
  FirstAngle = 0
  Height = 20
  Placement = pos=(80,35,36) rot=(0,0,1;0rad)
  Radius = 1
  SecondAngle = 0
FEATURE [Part::Cylinder] Cylinder857  label="Cylinder"
  Angle = 360
  AttacherType = Attacher::AttachEngine3D
  FirstAngle = 0
  Height = 20
  Placement = pos=(70,35,36) rot=(0,0,1;0rad)
  Radius = 1
  SecondAngle = 0
FEATURE [Part::Cylinder] Cylinder858  label="Cylinder"
  Angle = 360
  AttacherType = Attacher::AttachEngine3D
  FirstAngle = 0
  Height = 20
  Placement = pos=(70,40,36) rot=(0,0,1;0rad)
  Radius = 1
  SecondAngle = 0
FEATURE [Part::Cylinder] Cylinder859  label="Cylinder"
  Angle = 360
  AttacherType = Attacher::AttachEngine3D
  FirstAngle = 0
  Height = 20
  Placement = pos=(80,40,36) rot=(0,0,1;0rad)
  Radius = 1
  SecondAngle = 0
FEATURE [Part::MultiFuse] Fusion088026007031024007008004100051009001012006005005  label="screws-rear"
  Refine = true
  Shapes = -> [Fusion088026007031024007008004100051009001012006005004,Fusion088026007031024007008004100051009001012006001,Fusion088026007031024007008004100051009001012006002,Fusion088026007031024007008004100051009001012006003,Fusion088026007031024007008004100051009001012006004,Fusion088026007031024007008004100051009001012006005001,Fusion088026007031024007008004100051009001012006005002,+1 more]
FEATURE [Part::Cylinder] Cylinder860  label="Cylinder"
  Angle = 360
  AttacherType = Attacher::AttachEngine3D
  FirstAngle = 0
  Height = 20
  Placement = pos=(80,-35,36) rot=(0,0,1;0rad)
  Radius = 1
  SecondAngle = 0
FEATURE [Part::Cylinder] Cylinder861  label="Cylinder"
  Angle = 360
  AttacherType = Attacher::AttachEngine3D
  FirstAngle = 0
  Height = 20
  Placement = pos=(70,-35,36) rot=(0,0,1;0rad)
  Radius = 1
  SecondAngle = 0
FEATURE [Part::Cylinder] Cylinder862  label="Cylinder"
  Angle = 360
  AttacherType = Attacher::AttachEngine3D
  FirstAngle = 0
  Height = 20
  Placement = pos=(80,-40,36) rot=(0,0,1;0rad)
  Radius = 1
  SecondAngle = 0
FEATURE [Part::Cylinder] Cylinder863  label="Cylinder"
  Angle = 360
  AttacherType = Attacher::AttachEngine3D
  FirstAngle = 0
  Height = 20
  Placement = pos=(70,-40,36) rot=(0,0,1;0rad)
  Radius = 1
  SecondAngle = 0
FEATURE [Part::MultiFuse] Fusion088026007031024007008004100051009001012006005006  label="holes-rear"
  Refine = true
  Shapes = -> [Cylinder863,Cylinder856,Cylinder857,Cylinder858,Cylinder859,Cylinder860,Cylinder861,Cylinder862]
FEATURE [Part::Feature] Cut176013009033007019019008010045003002004008006021005004004004004002009  label="BEARING-5x9x3-MR95ZZ"
  Placement = pos=(163,-75,0) rot=(0,0,1;1.5708rad)
  shape: bbox 3 x 9 x 9 mm, 4 faces (baked)
FEATURE [Part::Feature] Cut176013009033007019019008010045003002004008006021005004004004004002010  label="BEARING-5x9x3-MR95ZZ"
  Placement = pos=(158,-75,0) rot=(0,0,1;1.5708rad)
  shape: bbox 3 x 9 x 9 mm, 4 faces (baked)
FEATURE [Part::Cylinder] Cylinder864  label="Cylinder"
  Angle = 360
  AttacherType = Attacher::AttachEngine3D
  FirstAngle = 0
  Height = 3
  Placement = pos=(91,0,46) rot=(0,1,0;1.5708rad)
  Radius = 8.5
  SecondAngle = 0
FEATURE [Part::Cylinder] Cylinder865  label="Cylinder"
  Angle = 360
  AttacherType = Attacher::AttachEngine3D
  FirstAngle = 0
  Height = 3
  Placement = pos=(91,0,46) rot=(0,1,0;1.5708rad)
  Radius = 7.5
  SecondAngle = 0
FEATURE [Part::Cut] Cut176013009033007019019008010045003002004008006021005004004004004002011  label="Cut"
  Base = -> Cylinder864
  Refine = true
  Tool = -> Cylinder865
FEATURE [Part::Chamfer] Chamfer228028
  Base = -> Cut176013009033007019019008010045003002004008006021005004004004004002011
  Edges = 1 edges r=0.9: [Edge4]
FEATURE [Part::Compound] Compound002  label="rear-axle-carvings"
  Links = -> [Fusion088026007031024007008004081019,Fusion088026007031024007008004100051009001012006005005,Fusion088026007031024007008004100051009001012006005006,Chamfer228028]
FEATURE [Part::Cut] Cut176013009033007019019008010045003002004008006021005004004004004002012  label="rear-axle-base-carved-narrow"
  Base = -> Cut176013009033007019019008010045003002004008006021005004004004004
  Refine = true
  Tool = -> Compound002
FEATURE [Part::Box] Box287  label="Cube286"
  AttacherType = Attacher::AttachEngine3D
  Height = 4.4
  Length = 24
  Placement = pos=(-12,24,7.6) rot=(0,0,1;0rad)
  Width = 12
FEATURE [Part::Box] Box288  label="Cube287"
  AttacherType = Attacher::AttachEngine3D
  Height = 3
  Length = 12
  Placement = pos=(-6,26,7.6) rot=(0,0,1;0rad)
  Width = 19.5
FEATURE [Part::Cylinder] Cylinder769
  Angle = 360
  AttacherType = Attacher::AttachEngine3D
  FirstAngle = 0
  Height = 37
  Placement = pos=(0,39,-19) rot=(0,0,1;0rad)
  Radius = 2.1
  SecondAngle = 0
FEATURE [Part::Cylinder] Cylinder770
  Angle = 360
  AttacherType = Attacher::AttachEngine3D
  FirstAngle = 0
  Height = 37
  Placement = pos=(-8,27.5,-19) rot=(0,0,1;0rad)
  Radius = 1.1
  SecondAngle = 0
FEATURE [Part::Cylinder] Cylinder771
  Angle = 360
  AttacherType = Attacher::AttachEngine3D
  FirstAngle = 0
  Height = 37
  Placement = pos=(8,33,-19) rot=(0,0,1;0rad)
  Radius = 1.1
  SecondAngle = 0
FEATURE [Part::Cylinder] Cylinder772
  Angle = 360
  AttacherType = Attacher::AttachEngine3D
  FirstAngle = 0
  Height = 37
  Placement = pos=(-8,33,-19) rot=(0,0,1;0rad)
  Radius = 1.1
  SecondAngle = 0
FEATURE [Part::Cylinder] Cylinder773
  Angle = 360
  AttacherType = Attacher::AttachEngine3D
  FirstAngle = 0
  Height = 37
  Placement = pos=(8,27.5,-19) rot=(0,0,1;0rad)
  Radius = 1.1
  SecondAngle = 0
FEATURE [Part::Cylinder] Cylinder774
  Angle = 360
  AttacherType = Attacher::AttachEngine3D
  FirstAngle = 0
  Height = 40
  Placement = pos=(0,24,0) rot=(-1,0,0;1.5708rad)
  Radius = 13
  SecondAngle = 0
FEATURE [Part::Cylinder] Cylinder775
  Angle = 360
  AttacherType = Attacher::AttachEngine3D
  FirstAngle = 0
  Height = 40
  Placement = pos=(0,24,0) rot=(-1,0,0;1.5708rad)
  Radius = 17
  SecondAngle = 0
FEATURE [Part::Cut] Cut176013009033007019019008010033  label="Cut"
  Base = -> Cylinder775
  Refine = true
  Tool = -> Cylinder774
FEATURE [Part::Cylinder] Cylinder776
  Angle = 360
  AttacherType = Attacher::AttachEngine3D
  FirstAngle = 0
  Height = 2
  Placement = pos=(8,27.5,8) rot=(0,0,1;0rad)
  Radius = 2.2
  SecondAngle = 0
FEATURE [Part::Cylinder] Cylinder777
  Angle = 360
  AttacherType = Attacher::AttachEngine3D
  FirstAngle = 0
  Height = 2
  Placement = pos=(-8,27.5,8) rot=(0,0,1;0rad)
  Radius = 2.2
  SecondAngle = 0
FEATURE [Part::Cylinder] Cylinder778
  Angle = 360
  AttacherType = Attacher::AttachEngine3D
  FirstAngle = 0
  Height = 2
  Placement = pos=(8,33,8) rot=(0,0,1;0rad)
  Radius = 2.2
  SecondAngle = 0
FEATURE [Part::Cylinder] Cylinder779
  Angle = 360
  AttacherType = Attacher::AttachEngine3D
  FirstAngle = 0
  Height = 2
  Placement = pos=(-8,33,8) rot=(0,0,1;0rad)
  Radius = 2.2
  SecondAngle = 0
FEATURE [Part::Cylinder] Cylinder780
  Angle = 360
  AttacherType = Attacher::AttachEngine3D
  FirstAngle = 0
  Height = 3
  Placement = pos=(8,27.5,8) rot=(0,0,1;0rad)
  Radius = 2.2
  SecondAngle = 0
FEATURE [Part::Cylinder] Cylinder781
  Angle = 360
  AttacherType = Attacher::AttachEngine3D
  FirstAngle = 0
  Height = 3
  Placement = pos=(8,33,8) rot=(0,0,1;0rad)
  Radius = 2.2
  SecondAngle = 0
FEATURE [Part::Cylinder] Cylinder782
  Angle = 360
  AttacherType = Attacher::AttachEngine3D
  FirstAngle = 0
  Height = 3
  Placement = pos=(-8,27.5,8) rot=(0,0,1;0rad)
  Radius = 2.2
  SecondAngle = 0
FEATURE [Part::Cylinder] Cylinder783
  Angle = 360
  AttacherType = Attacher::AttachEngine3D
  FirstAngle = 0
  Height = 3
  Placement = pos=(-8,33,8) rot=(0,0,1;0rad)
  Radius = 2.2
  SecondAngle = 0
FEATURE [Part::MultiFuse] Fusion088026007031024007008004080  label="Fusion"
  Refine = true
  Shapes = -> [Cylinder770,Cylinder771,Cylinder772,Cylinder773]
FEATURE [Part::MultiFuse] Fusion088026007031024007008004081006  label="Fusion"
  Refine = true
  Shapes = -> [Cylinder776,Cylinder778,Cylinder777,Cylinder779]
FEATURE [Part::MultiFuse] Fusion088026007031024007008004081008  label="Fusion"
  Placement = pos=(0,0,2) rot=(0,0,1;0rad)
  Refine = true
  Shapes = -> [Cylinder780,Cylinder781,Cylinder782,Cylinder783]
FEATURE [Part::Cylinder] Cylinder882
  Angle = 360
  AttacherType = Attacher::AttachEngine3D
  FirstAngle = 0
  Height = 0.15
  Placement = pos=(0,39,10.85) rot=(0,0,1;0rad)
  Radius = 3
  SecondAngle = 0
FEATURE [Part::MultiFuse] Fusion088026007031024007008004100051009001012006005014  label="Fusion"
  Placement = pos=(0,0,-0.4) rot=(0,0,1;0rad)
  Refine = true
  Shapes = -> [Cylinder882,Cylinder769]
FEATURE [Part::MultiFuse] Fusion088026007031024007008004100051009001012006005015  label="Fusion"
  Refine = true
  Shapes = -> [Box288,Box287]
FEATURE [Part::Fillet] Fillet125007020032013
  Base = -> Fusion088026007031024007008004100051009001012006005015
  Edges = 2 edges r=5.99: [Edge18,Edge21]
FEATURE [Part::Fillet] Fillet125007020032014
  Base = -> Fillet125007020032013
  Edges = 2 edges r=3: [Edge2,Edge13]
FEATURE [Part::Cut] Cut176013009033007019019008010045003002004008006021005004004004004002012010  label="Cut"
  Base = -> Fillet125007020032014
  Refine = true
  Tool = -> Cut176013009033007019019008010033
FEATURE [Part::MultiFuse] Fusion088026007031024007008004100051009001012006005016  label="Fusion"
  Refine = true
  Shapes = -> [Cut176013009033007019019008010045003002004008006021005004004004004002012010,Fusion088026007031024007008004081006]
FEATURE [Part::MultiFuse] Fusion088026007031024007008004100051009001012006005017  label="Fusion"
  Refine = true
  Shapes = -> [Fusion088026007031024007008004080,Fusion088026007031024007008004081008]
FEATURE [Part::Cut] Cut176013009033007019019008010045003002004008006021005004004004004002012011  label="Cut"
  Base = -> Fusion088026007031024007008004100051009001012006005016
  Refine = true
  Tool = -> Fusion088026007031024007008004100051009001012006005017
FEATURE [Part::Cut] Cut176013009033007019019008010045003002004008006021005004004004004002012012  label="rear-axle-steering-knukle-plate"
  Base = -> Cut176013009033007019019008010045003002004008006021005004004004004002012011
  Placement = pos=(75,-92.5,46) rot=(0,0,1;0rad)
  Refine = true
  Tool = -> Fusion088026007031024007008004100051009001012006005014
FEATURE [Part::Box] Box322  label="Cube286"
  AttacherType = Attacher::AttachEngine3D
  Height = 4.4
  Length = 24
  Placement = pos=(-12,24,7.6) rot=(0,0,1;0rad)
  Width = 12
FEATURE [Part::Box] Box323  label="Cube287"
  AttacherType = Attacher::AttachEngine3D
  Height = 3
  Length = 12
  Placement = pos=(-6,26,7.6) rot=(0,0,1;0rad)
  Width = 19.5
FEATURE [Part::Cylinder] Cylinder883
  Angle = 360
  AttacherType = Attacher::AttachEngine3D
  FirstAngle = 0
  Height = 37
  Placement = pos=(0,39,-11) rot=(0,0,1;0rad)
  Radius = 2.1
  SecondAngle = 0
FEATURE [Part::Cylinder] Cylinder884
  Angle = 360
  AttacherType = Attacher::AttachEngine3D
  FirstAngle = 0
  Height = 37
  Placement = pos=(-8,27.5,-19) rot=(0,0,1;0rad)
  Radius = 1.1
  SecondAngle = 0
FEATURE [Part::Cylinder] Cylinder885
  Angle = 360
  AttacherType = Attacher::AttachEngine3D
  FirstAngle = 0
  Height = 37
  Placement = pos=(8,33,-19) rot=(0,0,1;0rad)
  Radius = 1.1
  SecondAngle = 0
FEATURE [Part::Cylinder] Cylinder886
  Angle = 360
  AttacherType = Attacher::AttachEngine3D
  FirstAngle = 0
  Height = 37
  Placement = pos=(-8,33,-19) rot=(0,0,1;0rad)
  Radius = 1.1
  SecondAngle = 0
FEATURE [Part::Cylinder] Cylinder887
  Angle = 360
  AttacherType = Attacher::AttachEngine3D
  FirstAngle = 0
  Height = 37
  Placement = pos=(8,27.5,-19) rot=(0,0,1;0rad)
  Radius = 1.1
  SecondAngle = 0
FEATURE [Part::Cylinder] Cylinder888
  Angle = 360
  AttacherType = Attacher::AttachEngine3D
  FirstAngle = 0
  Height = 40
  Placement = pos=(0,24,0) rot=(-1,0,0;1.5708rad)
  Radius = 13
  SecondAngle = 0
FEATURE [Part::Cylinder] Cylinder889
  Angle = 360
  AttacherType = Attacher::AttachEngine3D
  FirstAngle = 0
  Height = 40
  Placement = pos=(0,24,0) rot=(-1,0,0;1.5708rad)
  Radius = 17
  SecondAngle = 0
FEATURE [Part::Cut] Cut176013009033007019019008010045003002004008006021005004004004004002012013  label="Cut"
  Base = -> Cylinder889
  Refine = true
  Tool = -> Cylinder888
FEATURE [Part::Cylinder] Cylinder890
  Angle = 360
  AttacherType = Attacher::AttachEngine3D
  FirstAngle = 0
  Height = 2
  Placement = pos=(8,27.5,8) rot=(0,0,1;0rad)
  Radius = 2.2
  SecondAngle = 0
FEATURE [Part::Cylinder] Cylinder891
  Angle = 360
  AttacherType = Attacher::AttachEngine3D
  FirstAngle = 0
  Height = 2
  Placement = pos=(-8,27.5,8) rot=(0,0,1;0rad)
  Radius = 2.2
  SecondAngle = 0
FEATURE [Part::Cylinder] Cylinder892
  Angle = 360
  AttacherType = Attacher::AttachEngine3D
  FirstAngle = 0
  Height = 2
  Placement = pos=(8,33,8) rot=(0,0,1;0rad)
  Radius = 2.2
  SecondAngle = 0
FEATURE [Part::Cylinder] Cylinder893
  Angle = 360
  AttacherType = Attacher::AttachEngine3D
  FirstAngle = 0
  Height = 2
  Placement = pos=(-8,33,8) rot=(0,0,1;0rad)
  Radius = 2.2
  SecondAngle = 0
FEATURE [Part::Cylinder] Cylinder894
  Angle = 360
  AttacherType = Attacher::AttachEngine3D
  FirstAngle = 0
  Height = 3
  Placement = pos=(8,27.5,8) rot=(0,0,1;0rad)
  Radius = 2.2
  SecondAngle = 0
FEATURE [Part::Cylinder] Cylinder895
  Angle = 360
  AttacherType = Attacher::AttachEngine3D
  FirstAngle = 0
  Height = 3
  Placement = pos=(8,33,8) rot=(0,0,1;0rad)
  Radius = 2.2
  SecondAngle = 0
FEATURE [Part::Cylinder] Cylinder896
  Angle = 360
  AttacherType = Attacher::AttachEngine3D
  FirstAngle = 0
  Height = 3
  Placement = pos=(-8,27.5,8) rot=(0,0,1;0rad)
  Radius = 2.2
  SecondAngle = 0
FEATURE [Part::Cylinder] Cylinder897
  Angle = 360
  AttacherType = Attacher::AttachEngine3D
  FirstAngle = 0
  Height = 3
  Placement = pos=(-8,33,8) rot=(0,0,1;0rad)
  Radius = 2.2
  SecondAngle = 0
FEATURE [Part::Cylinder] Cylinder898
  Angle = 360
  AttacherType = Attacher::AttachEngine3D
  FirstAngle = 0
  Height = 8.15
  Placement = pos=(0,39,10.85) rot=(0,0,1;0rad)
  Radius = 3
  SecondAngle = 0
FEATURE [Part::MultiFuse] Fusion088026007031024007008004100051009001012006005018  label="Fusion"
  Refine = true
  Shapes = -> [Cylinder884,Cylinder885,Cylinder886,Cylinder887]
FEATURE [Part::MultiFuse] Fusion088026007031024007008004100051009001012006005019  label="Fusion"
  Refine = true
  Shapes = -> [Cylinder890,Cylinder892,Cylinder891,Cylinder893]
FEATURE [Part::MultiFuse] Fusion088026007031024007008004100051009001012006005020  label="Fusion"
  Placement = pos=(0,0,2) rot=(0,0,1;0rad)
  Refine = true
  Shapes = -> [Cylinder894,Cylinder895,Cylinder896,Cylinder897]
FEATURE [Part::MultiFuse] Fusion088026007031024007008004100051009001012006005021  label="Fusion"
  Placement = pos=(75,-92.5,45.6) rot=(0,0,1;0rad)
  Refine = true
  Shapes = -> [Cylinder898,Cylinder883]
FEATURE [Part::MultiFuse] Fusion088026007031024007008004100051009001012006005022  label="Fusion"
  Refine = true
  Shapes = -> [Box323,Box322]
FEATURE [Part::Fillet] Fillet125007020032015
  Base = -> Fusion088026007031024007008004100051009001012006005022
  Edges = 2 edges r=5.99: [Edge18,Edge21]
FEATURE [Part::Fillet] Fillet125007020032016
  Base = -> Fillet125007020032015
  Edges = 2 edges r=3: [Edge2,Edge13]
FEATURE [Part::Cut] Cut176013009033007019019008010045003002004008006021005004004004004002012014  label="Cut"
  Base = -> Fillet125007020032016
  Refine = true
  Tool = -> Cut176013009033007019019008010045003002004008006021005004004004004002012013
FEATURE [Part::MultiFuse] Fusion088026007031024007008004100051009001012006005023  label="Fusion"
  Refine = true
  Shapes = -> [Cut176013009033007019019008010045003002004008006021005004004004004002012014,Fusion088026007031024007008004100051009001012006005019]
FEATURE [Part::MultiFuse] Fusion088026007031024007008004100051009001012006005024  label="Fusion"
  Refine = true
  Shapes = -> [Fusion088026007031024007008004100051009001012006005018,Fusion088026007031024007008004100051009001012006005020]
FEATURE [Part::Cut] Cut176013009033007019019008010045003002004008006021005004004004004002012015  label="Cut"
  Base = -> Fusion088026007031024007008004100051009001012006005023
  Placement = pos=(75,-92.5,46) rot=(0,0,1;0rad)
  Refine = true
  Tool = -> Fusion088026007031024007008004100051009001012006005024
FEATURE [Part::Box] Box324  label="Cube"
  AttacherType = Attacher::AttachEngine3D
  Height = 3
  Length = 10
  Placement = pos=(70,-67,56.6) rot=(0,0,1;0rad)
  Width = 10.5
FEATURE [Part::Box] Box325  label="Cube"
  AttacherType = Attacher::AttachEngine3D
  Height = 8
  Length = 7
  Placement = pos=(71.5,-64,56.6) rot=(0,0,1;0rad)
  Width = 29
FEATURE [Part::Box] Box326  label="Cube"
  AttacherType = Attacher::AttachEngine3D
  Height = 5
  Length = 7
  Placement = pos=(71.5,-43.5,56.6) rot=(0,0,1;0rad)
  Width = 32
FEATURE [Part::Cut] Cut176013009033007019019008010045003002004008006021005004004004004002012016  label="Cut"
  Base = -> Box325
  Refine = true
  Tool = -> Box326
FEATURE [Part::Chamfer] Chamfer228030
  Base = -> Cut176013009033007019019008010045003002004008006021005004004004004002012016
  Edges = 1 edges r=4.99: [Edge14]
FEATURE [Part::Chamfer] Chamfer228031
  Base = -> Chamfer228030
  Edges = 1 edges: [Edge20 r1=5 r2=16]
FEATURE [Part::Fillet] Fillet125007020032017
  Base = -> Box324
  Edges = 3 edges r=1.5: [Edge2,Edge6,Edge10]
FEATURE [Part::Fillet] Fillet125007020032018
  Base = -> Chamfer228031
  Edges = 4 edges r=1: [Edge1,Edge2,Edge10,Edge13]
FEATURE [Part::Cylinder] Cylinder899
  Angle = 360
  AttacherType = Attacher::AttachEngine3D
  FirstAngle = 0
  Height = 8.9
  Placement = pos=(75,-53.5,55) rot=(0,0,1;0rad)
  Radius = 5
  SecondAngle = 0
FEATURE [Part::Fillet] Fillet125007020032019
  Base = -> Cylinder899
  Edges = 1 edges r=1: [Edge3]
FEATURE [Part::MultiFuse] Fusion088026007031024007008004100051009001012006005025  label="Fusion"
  Refine = true
  Shapes = -> [Fillet125007020032017,Fillet125007020032018,Fillet125007020032019,Cut176013009033007019019008010045003002004008006021005004004004004002012015]
FEATURE [Part::Cut] Cut176013009033007019019008010045003002004008006021005004004004004002012017  label="Cut"
  Base = -> Fusion088026007031024007008004100051009001012006005025
  Refine = true
  Tool = -> Fusion088026007031024007008004100051009001012006005021
FEATURE [Part::Cylinder] Cylinder900
  Angle = 360
  AttacherType = Attacher::AttachEngine3D
  FirstAngle = 0
  Height = 3
  Placement = pos=(75,-32,61.6) rot=(0,0,1;0rad)
  Radius = 4
  SecondAngle = 0
FEATURE [Part::Cylinder] Cylinder901
  Angle = 360
  AttacherType = Attacher::AttachEngine3D
  FirstAngle = 0
  Height = 3
  Placement = pos=(75,-35,61.6) rot=(0,0,1;0rad)
  Radius = 1.25
  SecondAngle = 0
FEATURE [Part::Fillet] Fillet125007020032020
  Base = -> Cylinder900
  Edges = 1 edges r=1: [Edge3]
  Placement = pos=(0,-3,0) rot=(0,0,1;0rad)
FEATURE [Part::MultiFuse] Fusion088026007031024007008004100051009001012006005026  label="Fusion"
  Refine = true
  Shapes = -> [Fillet125007020032020,Cut176013009033007019019008010045003002004008006021005004004004004002012017]
FEATURE [Part::Cut] Cut176013009033007019019008010045003002004008006021005004004004004002012018  label="rear-axle-steering-knukle-upper-plate-right"
  Base = -> Fusion088026007031024007008004100051009001012006005026
  Refine = true
  Tool = -> Cylinder901
FEATURE [Part::Part2DObjectPython] Line017  label="front-wheels-axle-path"  # Draft 2D object (typed FeaturePython)
  Closed = true
  End = (260,90,62)
  FilletRadius = 0
  MapMode = 5
  Placement = pos=(260,-70,60) rot=(0,0,1;0rad)
  Points = (2) [(0,-20,2),(0,160,2)]
  Start = (260,-90,62)
FEATURE [Part::Part2DObjectPython] Line010  label="front-wheels-right-path"  # Draft 2D object (typed FeaturePython)
  Closed = true
  End = (325,-69,62)
  FilletRadius = 0
  MapMode = 5
  Placement = pos=(195,-69,62) rot=(0,0,1;0rad)
  Points = (2) [(0,0,0),(130,0,0)]
  Start = (195,-69,62)
FEATURE [Part::Part2DObjectPython] Line011  label="front-wheels-left-path"  # Draft 2D object (typed FeaturePython)
  Closed = true
  End = (325,69,62)
  FilletRadius = 0
  MapMode = 5
  Placement = pos=(195,69,62) rot=(0,0,1;0rad)
  Points = (2) [(0,0,0),(130,0,0)]
  Start = (195,69,62)
FEATURE [Part::Part2DObjectPython] Line009  label="rear-wheels-left-path"  # Draft 2D object (typed FeaturePython)
  Closed = true
  End = (140,70,46)
  FilletRadius = 0
  MapMode = 5
  Placement = pos=(10,70,46) rot=(0,0,1;0rad)
  Points = (2) [(0,0,0),(130,0,0)]
  Start = (10,70,46)
FEATURE [Part::Part2DObjectPython] Line008  label="rear-wheels-right-path"  # Draft 2D object (typed FeaturePython)
  Closed = true
  End = (140,-70,46)
  FilletRadius = 0
  MapMode = 5
  Placement = pos=(10,-70,46) rot=(0,0,1;0rad)
  Points = (2) [(0,0,0),(130,0,0)]
  Start = (10,-70,46)
FEATURE [Part::Part2DObjectPython] Line018  label="front-wheels-diff-path"  # Draft 2D object (typed FeaturePython)
  Closed = true
  End = (234,70,53)
  FilletRadius = 0
  MapMode = 5
  Placement = pos=(234,-70,53) rot=(0,0,1;0rad)
  Points = (2) [(0,0,0),(0,140,0)]
  Start = (234,-70,53)
FEATURE [Part::Feature] Cut176013009033007019019008010045003002004008006021005004004004004002012019  label="BEARING-8x12x3.5-MR128ZZ"
  Placement = pos=(154,-57.5,9) rot=(0,0,1;0rad)
  shape: bbox 12 x 3.5 x 12 mm, 4 faces (baked)
FEATURE [Part::Feature] Cut176013009033007019019008010045003002004008006021005004004004004002012020  label="BEARING-8x12x3.5-MR128ZZ"
  Placement = pos=(154,-77,9) rot=(0,0,1;0rad)
  shape: bbox 12 x 3.5 x 12 mm, 4 faces (baked)
FEATURE [Part::Box] Box328  label="Cube"
  AttacherType = Attacher::AttachEngine3D
  Height = 51
  Length = 75
  Placement = pos=(207,16,35) rot=(0,0,1;0rad)
  Width = 5
FEATURE [Part::Cylinder] Cylinder906
  Angle = 360
  AttacherType = Attacher::AttachEngine3D
  FirstAngle = 0
  Height = 37
  Placement = pos=(8,33,-19) rot=(0,0,1;0rad)
  Radius = 1.1
  SecondAngle = 0
FEATURE [Part::Box] Box330  label="Cube286"
  AttacherType = Attacher::AttachEngine3D
  Height = 4.4
  Length = 24
  Placement = pos=(-12,24,7.6) rot=(0,0,1;0rad)
  Width = 12
FEATURE [Part::Cylinder] Cylinder907
  Angle = 360
  AttacherType = Attacher::AttachEngine3D
  FirstAngle = 0
  Height = 37
  Placement = pos=(0,39,-19) rot=(0,0,1;0rad)
  Radius = 2.1
  SecondAngle = 0
FEATURE [Part::Cylinder] Cylinder908
  Angle = 360
  AttacherType = Attacher::AttachEngine3D
  FirstAngle = 0
  Height = 37
  Placement = pos=(-8,27.5,-19) rot=(0,0,1;0rad)
  Radius = 1.1
  SecondAngle = 0
FEATURE [Part::Box] Box331  label="Cube287"
  AttacherType = Attacher::AttachEngine3D
  Height = 3
  Length = 12
  Placement = pos=(-6,26,9) rot=(0,0,1;0rad)
  Width = 19.5
FEATURE [Part::MultiFuse] Fusion088026007031024007008004100051009001012006005029  label="Fusion"
  Refine = true
  Shapes = -> [Box331,Box330]
FEATURE [Part::Fillet] Fillet125007020032024
  Base = -> Fusion088026007031024007008004100051009001012006005029
  Edges = 2 edges r=5.99: [Edge18,Edge21]
FEATURE [Part::Fillet] Fillet125007020032023
  Base = -> Fillet125007020032024
  Edges = 2 edges r=3: [Edge2,Edge17]
FEATURE [Part::Cylinder] Cylinder909
  Angle = 360
  AttacherType = Attacher::AttachEngine3D
  FirstAngle = 0
  Height = 40
  Placement = pos=(0,24,0) rot=(-1,0,0;1.5708rad)
  Radius = 13
  SecondAngle = 0
FEATURE [Part::Cylinder] Cylinder910
  Angle = 360
  AttacherType = Attacher::AttachEngine3D
  FirstAngle = 0
  Height = 0.15
  Placement = pos=(0,39,10.85) rot=(0,0,1;0rad)
  Radius = 3
  SecondAngle = 0
FEATURE [Part::MultiFuse] Fusion088026007031024007008004100051009001012006005028  label="Fusion"
  Placement = pos=(0,0,1) rot=(0,0,1;0rad)
  Refine = true
  Shapes = -> [Cylinder910,Cylinder907]
FEATURE [Part::Cylinder] Cylinder911
  Angle = 360
  AttacherType = Attacher::AttachEngine3D
  FirstAngle = 0
  Height = 2
  Placement = pos=(-8,27.5,8) rot=(0,0,1;0rad)
  Radius = 2.2
  SecondAngle = 0
FEATURE [Part::Cylinder] Cylinder912
  Angle = 360
  AttacherType = Attacher::AttachEngine3D
  FirstAngle = 0
  Height = 37
  Placement = pos=(-8,33,-19) rot=(0,0,1;0rad)
  Radius = 1.1
  SecondAngle = 0
FEATURE [Part::Cylinder] Cylinder913
  Angle = 360
  AttacherType = Attacher::AttachEngine3D
  FirstAngle = 0
  Height = 2
  Placement = pos=(8,27.5,8) rot=(0,0,1;0rad)
  Radius = 2.2
  SecondAngle = 0
FEATURE [Part::Cylinder] Cylinder914
  Angle = 360
  AttacherType = Attacher::AttachEngine3D
  FirstAngle = 0
  Height = 40
  Placement = pos=(0,24,0) rot=(-1,0,0;1.5708rad)
  Radius = 17
  SecondAngle = 0
FEATURE [Part::Cut] Cut176013009033007019019008010045003002004008006021005004004004004002012021  label="Cut"
  Base = -> Cylinder914
  Refine = true
  Tool = -> Cylinder909
FEATURE [Part::Cylinder] Cylinder915
  Angle = 360
  AttacherType = Attacher::AttachEngine3D
  FirstAngle = 0
  Height = 2
  Placement = pos=(-8,33,8) rot=(0,0,1;0rad)
  Radius = 2.2
  SecondAngle = 0
FEATURE [Part::Cylinder] Cylinder916
  Angle = 360
  AttacherType = Attacher::AttachEngine3D
  FirstAngle = 0
  Height = 3
  Placement = pos=(8,27.5,8) rot=(0,0,1;0rad)
  Radius = 2.2
  SecondAngle = 0
FEATURE [Part::Cylinder] Cylinder917
  Angle = 360
  AttacherType = Attacher::AttachEngine3D
  FirstAngle = 0
  Height = 2
  Placement = pos=(8,33,8) rot=(0,0,1;0rad)
  Radius = 2.2
  SecondAngle = 0
FEATURE [Part::MultiFuse] Fusion088026007031024007008004100051009001012006005031  label="Fusion"
  Refine = true
  Shapes = -> [Cylinder913,Cylinder917,Cylinder911,Cylinder915]
FEATURE [Part::Cylinder] Cylinder918
  Angle = 360
  AttacherType = Attacher::AttachEngine3D
  FirstAngle = 0
  Height = 3
  Placement = pos=(8,33,8) rot=(0,0,1;0rad)
  Radius = 2.2
  SecondAngle = 0
FEATURE [Part::Cylinder] Cylinder919
  Angle = 360
  AttacherType = Attacher::AttachEngine3D
  FirstAngle = 0
  Height = 37
  Placement = pos=(8,27.5,-19) rot=(0,0,1;0rad)
  Radius = 1.1
  SecondAngle = 0
FEATURE [Part::MultiFuse] Fusion088026007031024007008004100051009001012006005030  label="Fusion"
  Refine = true
  Shapes = -> [Cylinder908,Cylinder906,Cylinder912,Cylinder919]
FEATURE [Part::Cylinder] Cylinder920
  Angle = 360
  AttacherType = Attacher::AttachEngine3D
  FirstAngle = 0
  Height = 3
  Placement = pos=(-8,27.5,8) rot=(0,0,1;0rad)
  Radius = 2.2
  SecondAngle = 0
FEATURE [Part::Cylinder] Cylinder921
  Angle = 360
  AttacherType = Attacher::AttachEngine3D
  FirstAngle = 0
  Height = 3
  Placement = pos=(-8,33,8) rot=(0,0,1;0rad)
  Radius = 2.2
  SecondAngle = 0
FEATURE [Part::MultiFuse] Fusion088026007031024007008004100051009001012006005027  label="Fusion"
  Placement = pos=(0,0,2) rot=(0,0,1;0rad)
  Refine = true
  Shapes = -> [Cylinder916,Cylinder918,Cylinder920,Cylinder921]
FEATURE [Part::MultiFuse] Fusion088026007031024007008004100051009001012006005033  label="Fusion"
  Refine = true
  Shapes = -> [Fusion088026007031024007008004100051009001012006005030,Fusion088026007031024007008004100051009001012006005027]
FEATURE [Part::Cut] Cut176013009033007019019008010045003002004008006021005004004004004002012022  label="Cut"
  Base = -> Fillet125007020032023
  Refine = true
  Tool = -> Cut176013009033007019019008010045003002004008006021005004004004004002012021
FEATURE [Part::MultiFuse] Fusion088026007031024007008004100051009001012006005034  label="Fusion"
  Refine = true
  Shapes = -> [Cut176013009033007019019008010045003002004008006021005004004004004002012022,Fusion088026007031024007008004100051009001012006005031]
FEATURE [Part::Cut] Cut176013009033007019019008010045003002004008006021005004004004004002012023  label="Cut"
  Base = -> Fusion088026007031024007008004100051009001012006005034
  Refine = true
  Tool = -> Fusion088026007031024007008004100051009001012006005033
FEATURE [Part::Cut] Cut176013009033007019019008010045003002004008006021005004004004004002012024  label="Cut"
  Base = -> Cut176013009033007019019008010045003002004008006021005004004004004002012023
  Placement = pos=(75,-92.5,46) rot=(1,0,0;0rad)
  Refine = true
  Tool = -> Fusion088026007031024007008004100051009001012006005028
FEATURE [Part::Box] Box332  label="Cube261"
  AttacherType = Attacher::AttachEngine3D
  Height = 3.5
  Length = 10
  Placement = pos=(70,32.5,51.5) rot=(0,0,1;0rad)
  Width = 24.5
FEATURE [Part::Box] Box333  label="Cube261"
  AttacherType = Attacher::AttachEngine3D
  Height = 3.5
  Length = 14
  Placement = pos=(68,32.5,51.5) rot=(0,0,1;0rad)
  Width = 12
FEATURE [Part::Box] Box334  label="Cube261"
  AttacherType = Attacher::AttachEngine3D
  Height = 3.5
  Length = 14
  Placement = pos=(68,32.5,51.5) rot=(0,0,1;0rad)
  Width = 25
FEATURE [Part::Cylinder] Cylinder922
  Angle = 360
  AttacherType = Attacher::AttachEngine3D
  FirstAngle = 0
  Height = 10
  Placement = pos=(-4.5,61,0) rot=(0,0,1;0rad)
  Radius = 0.8
  SecondAngle = 0
FEATURE [Part::Cylinder] Cylinder923
  Angle = 360
  AttacherType = Attacher::AttachEngine3D
  FirstAngle = 0
  Height = 10
  Placement = pos=(5.5,61,0) rot=(0,0,1;0rad)
  Radius = 0.8
  SecondAngle = 0
FEATURE [Part::Cylinder] Cylinder925
  Angle = 360
  AttacherType = Attacher::AttachEngine3D
  FirstAngle = 0
  Height = 10
  Placement = pos=(-4.5,66,0) rot=(0,0,1;0rad)
  Radius = 0.8
  SecondAngle = 0
FEATURE [Part::Cylinder] Cylinder926
  Angle = 360
  AttacherType = Attacher::AttachEngine3D
  FirstAngle = 0
  Height = 6.5
  Placement = pos=(75,53.5,51.5) rot=(0,0,1;0rad)
  Radius = 2
  SecondAngle = 0
FEATURE [Part::Cylinder] Cylinder927
  Angle = 360
  AttacherType = Attacher::AttachEngine3D
  FirstAngle = 0
  Height = 10
  Placement = pos=(75,53.5,50.5) rot=(0,0,1;0rad)
  Radius = 1.25
  SecondAngle = 0
FEATURE [Part::Cylinder] Cylinder928
  Angle = 360
  AttacherType = Attacher::AttachEngine3D
  FirstAngle = 0
  Height = 10
  Placement = pos=(5.5,66,0) rot=(0,0,1;0rad)
  Radius = 0.8
  SecondAngle = 0
FEATURE [Part::Cylinder] Cylinder929  label="Cylinder"
  Angle = 360
  AttacherType = Attacher::AttachEngine3D
  FirstAngle = 0
  Height = 25
  Placement = pos=(75,57.5,46) rot=(1,0,0;1.5708rad)
  Radius = 9
  SecondAngle = 0
FEATURE [Part::Cut] Cut176013009033007019019008010045003002004008006021005004004004004002012025  label="Cut"
  Base = -> Box334
  Refine = true
  Tool = -> Cylinder929
FEATURE [Part::Cylinder] Cylinder930
  Angle = 360
  AttacherType = Attacher::AttachEngine3D
  FirstAngle = 0
  Height = 1.5
  Placement = pos=(-4.5,61,0) rot=(0,0,1;0rad)
  Radius = 2
  SecondAngle = 0
FEATURE [Part::Cylinder] Cylinder931
  Angle = 360
  AttacherType = Attacher::AttachEngine3D
  FirstAngle = 0
  Height = 1.5
  Placement = pos=(5.5,61,0) rot=(0,0,1;0rad)
  Radius = 2
  SecondAngle = 0
FEATURE [Part::Cylinder] Cylinder932
  Angle = 360
  AttacherType = Attacher::AttachEngine3D
  FirstAngle = 0
  Height = 1.5
  Placement = pos=(-4.5,66,0) rot=(0,0,1;0rad)
  Radius = 2
  SecondAngle = 0
FEATURE [Part::Cylinder] Cylinder933
  Angle = 360
  AttacherType = Attacher::AttachEngine3D
  FirstAngle = 0
  Height = 1.5
  Placement = pos=(5.5,66,0) rot=(0,0,1;0rad)
  Radius = 2
  SecondAngle = 0
FEATURE [Part::Cylinder] Cylinder934
  Angle = 360
  AttacherType = Attacher::AttachEngine3D
  FirstAngle = 0
  Height = 1.5
  Placement = pos=(-4.5,61,0) rot=(0,0,1;0rad)
  Radius = 2
  SecondAngle = 0
FEATURE [Part::Cylinder] Cylinder935
  Angle = 360
  AttacherType = Attacher::AttachEngine3D
  FirstAngle = 0
  Height = 1.5
  Placement = pos=(5.5,61,0) rot=(0,0,1;0rad)
  Radius = 2
  SecondAngle = 0
FEATURE [Part::Cylinder] Cylinder936
  Angle = 360
  AttacherType = Attacher::AttachEngine3D
  FirstAngle = 0
  Height = 1.5
  Placement = pos=(-4.5,66,0) rot=(0,0,1;0rad)
  Radius = 2
  SecondAngle = 0
FEATURE [Part::Cylinder] Cylinder937
  Angle = 360
  AttacherType = Attacher::AttachEngine3D
  FirstAngle = 0
  Height = 1.5
  Placement = pos=(5.5,66,0) rot=(0,0,1;0rad)
  Radius = 2
  SecondAngle = 0
FEATURE [Part::MultiFuse] Fusion088026007031024007008004100051009001012006005035  label="Fusion"
  Placement = pos=(74.5,-26,46) rot=(0,0,1;0rad)
  Refine = true
  Shapes = -> [Cylinder923,Cylinder925,Cylinder922,Cylinder928]
FEATURE [Part::MultiFuse] Fusion088026007031024007008004100051009001012006005036  label="Fusion"
  Refine = true
  Shapes = -> [Box333,Box332]
FEATURE [Part::Chamfer] Chamfer228033
  Base = -> Fusion088026007031024007008004100051009001012006005036
  Edges = 2 edges: [Edge7 r1=1.99 r2=6,Edge13 r1=1.99 r2=6]
FEATURE [Part::Fillet] Fillet125007020032025
  Base = -> Chamfer228033
  Edges = 2 edges r=4.99: [Edge29,Edge30]
FEATURE [Part::MultiFuse] Fusion088026007031024007008004100051009001012006005038  label="Fusion"
  Placement = pos=(74.5,-26,51.5) rot=(0,0,1;0rad)
  Refine = true
  Shapes = -> [Cylinder931,Cylinder932,Cylinder930,Cylinder933]
FEATURE [Part::MultiFuse] Fusion088026007031024007008004100051009001012006005039  label="Fusion"
  Placement = pos=(74.5,-26,53) rot=(0,0,1;0rad)
  Refine = true
  Shapes = -> [Cylinder935,Cylinder936,Cylinder934,Cylinder937]
FEATURE [Part::MultiFuse] Fusion088026007031024007008004100051009001012006005040  label="Fusion"
  Refine = true
  Shapes = -> [Fusion088026007031024007008004100051009001012006005039,Fusion088026007031024007008004100051009001012006005035]
FEATURE [Part::Cylinder] Cylinder938
  Angle = 360
  AttacherType = Attacher::AttachEngine3D
  FirstAngle = 0
  Height = 3.5
  Placement = pos=(75,52,51.5) rot=(0,0,1;0rad)
  Radius = 5
  SecondAngle = 0
FEATURE [Part::Cut] Cut176013009033007019019008010045003002004008006021005004004004004002012026  label="Cut"
  Base = -> Fillet125007020032025
  Refine = true
  Tool = -> Cut176013009033007019019008010045003002004008006021005004004004004002012025
FEATURE [Part::MultiFuse] Fusion088026007031024007008004100051009001012006005041  label="Fusion"
  Refine = true
  Shapes = -> [Cut176013009033007019019008010045003002004008006021005004004004004002012026,Cylinder938]
FEATURE [Part::MultiFuse] Fusion088026007031024007008004100051009001012006005042  label="Fusion"
  Refine = true
  Shapes = -> [Fusion088026007031024007008004100051009001012006005041,Cylinder926]
FEATURE [Part::Cut] Cut176013009033007019019008010045003002004008006021005004004004004002012027  label="Cut"
  Base = -> Fusion088026007031024007008004100051009001012006005042
  Refine = true
  Tool = -> Cylinder927
FEATURE [Part::MultiFuse] Fusion088026007031024007008004100051009001012006005043  label="Fusion"
  Refine = true
  Shapes = -> [Fusion088026007031024007008004100051009001012006005038,Cut176013009033007019019008010045003002004008006021005004004004004002012027]
FEATURE [Part::Cut] Cut176013009033007019019008010045003002004008006021005004004004004002012028  label="rear-axle-knukle-holder-upper-right"
  Base = -> Fusion088026007031024007008004100051009001012006005043
  Placement = pos=(150,-7e-15,0) rot=(0,0,1;3.14159rad)
  Refine = true
  Tool = -> Fusion088026007031024007008004100051009001012006005040
FEATURE [Part::Cylinder] Cylinder939
  Angle = 360
  AttacherType = Attacher::AttachEngine3D
  FirstAngle = 0
  Height = 3.5
  Placement = pos=(75,-52,51.5) rot=(0,0,1;0rad)
  Radius = 5.5
  SecondAngle = 0
FEATURE [Part::Cut] Cut176013009033007019019008010045003002004008006021005004004004004002012029  label="rear-axle-steering-knukle-upper-plate-right"
  Base = -> Cut176013009033007019019008010045003002004008006021005004004004004002012024
  Refine = true
  Tool = -> Cylinder939
FEATURE [Part::Cylinder] Cylinder940  label="Cylinder"
  Angle = 360
  AttacherType = Attacher::AttachEngine3D
  FirstAngle = 0
  Height = 3.5
  Placement = pos=(75,48,46) rot=(1,0,0;1.5708rad)
  Radius = 9
  SecondAngle = 0
FEATURE [Part::Cylinder] Cylinder941  label="Cylinder"
  Angle = 360
  AttacherType = Attacher::AttachEngine3D
  FirstAngle = 0
  Height = 3.5
  Placement = pos=(75,48,46) rot=(1,0,0;1.5708rad)
  Radius = 3
  SecondAngle = 0
FEATURE [Part::Cut] Cut176013009033007019019008010045003002004008006021005004004004004002012030  label="Cut"
  Base = -> Cylinder940
  Refine = true
  Tool = -> Cylinder941
FEATURE [Part::Box] Box335  label="Cube"
  AttacherType = Attacher::AttachEngine3D
  Height = 28
  Length = 24
  Placement = pos=(63,-20,32) rot=(0,0,1;0rad)
  Width = 40
FEATURE [Part::Box] Box336  label="Cube"
  AttacherType = Attacher::AttachEngine3D
  Height = 3.5
  Length = 18
  Placement = pos=(66,32.5,51.5) rot=(0,0,1;0rad)
  Width = 16
FEATURE [Part::Box] Box337  label="Cube"
  AttacherType = Attacher::AttachEngine3D
  Height = 3.5
  Length = 18
  Placement = pos=(66,32.5,37) rot=(0,0,1;0rad)
  Width = 16
FEATURE [Part::Box] Box338  label="Cube"
  AttacherType = Attacher::AttachEngine3D
  Height = 3.5
  Length = 18
  Placement = pos=(66,-48.5,37) rot=(0,0,1;0rad)
  Width = 16
FEATURE [Part::Box] Box339  label="Cube"
  AttacherType = Attacher::AttachEngine3D
  Height = 3.5
  Length = 18
  Placement = pos=(66,-48.5,51.5) rot=(0,0,1;0rad)
  Width = 16
FEATURE [Part::Cylinder] Cylinder942  label="Cylinder"
  Angle = 360
  AttacherType = Attacher::AttachEngine3D
  FirstAngle = 0
  Height = 40
  Placement = pos=(57,0,46) rot=(0,1,0;1.5708rad)
  Radius = 8.6
  SecondAngle = 0
FEATURE [Part::Cylinder] Cylinder943  label="Cylinder"
  Angle = 360
  AttacherType = Attacher::AttachEngine3D
  FirstAngle = 0
  Height = 96
  Placement = pos=(75,48,46) rot=(1,0,0;1.5708rad)
  Radius = 9
  SecondAngle = 0
FEATURE [Part::Fillet] Fillet125007020032026
  Base = -> Box335
  Edges = 4 edges r=12: [Edge9,Edge10,Edge11,Edge12]
FEATURE [Part::Fillet] Fillet125007020032027
  Base = -> Fillet125007020032026
  Edges = 8 edges r=7: [Edge2,Edge4,Edge6,Edge8,Edge13,Edge15,Edge20,Edge22]
FEATURE [Part::MultiFuse] Fusion088026007031024007008004100051009001012006005046  label="Fusion-0002"
  Refine = true
  Shapes = -> [Box339,Box336,Box337,Box338]
FEATURE [Part::Box] Box340  label="Cube201"
  AttacherType = Attacher::AttachEngine3D
  Height = 12.4
  Length = 12.8
  Placement = pos=(1.1,21.7,1.3) rot=(0,0,1;0rad)
  Width = 3.8
FEATURE [Part::Box] Box341  label="Cube202"
  AttacherType = Attacher::AttachEngine3D
  Height = 12.4
  Length = 12.8
  Placement = pos=(1.1,21.5,1.3) rot=(0,0,1;0rad)
  Width = 3.8
FEATURE [Part::Chamfer] Chamfer228034  label="bearing_shape_035"
  Base = -> Box340
  Edges = 4 edges r=3: [Edge2,Edge4,Edge6,Edge8]
  Placement = pos=(-7.5,59.5,-7.5) rot=(0,0,1;0rad)
FEATURE [Part::Chamfer] Chamfer228035  label="bearing_shape_036"
  Base = -> Box341
  Edges = 4 edges r=3: [Edge2,Edge4,Edge6,Edge8]
  Placement = pos=(-7.5,79.5,-7.5) rot=(0,0,1;0rad)
FEATURE [Part::Cylinder] Cylinder944
  Angle = 360
  AttacherType = Attacher::AttachEngine3D
  FirstAngle = 0
  Height = 3
  Placement = pos=(-14.5,52,7.5) rot=(0,1,0;1.5708rad)
  Radius = 4.75
  SecondAngle = 0
FEATURE [Part::Cylinder] Cylinder945
  Angle = 360
  AttacherType = Attacher::AttachEngine3D
  FirstAngle = 0
  Height = 8
  Placement = pos=(-14.5,52,7.5) rot=(0,1,0;1.5708rad)
  Radius = 3.2
  SecondAngle = 0
FEATURE [Part::Cylinder] Cylinder946
  Angle = 360
  AttacherType = Attacher::AttachEngine3D
  FirstAngle = 0
  Height = 5.5
  Placement = pos=(-6.5,52,7.5) rot=(0,1,0;1.5708rad)
  Radius = 7
  SecondAngle = 0
FEATURE [Part::Cylinder] Cylinder947
  Angle = 360
  AttacherType = Attacher::AttachEngine3D
  FirstAngle = 0
  Height = 3.2
  Placement = pos=(-9.7,52,7.5) rot=(0,1,0;1.5708rad)
  Radius = 4.8
  SecondAngle = 0
FEATURE [Part::Cylinder] Cylinder948
  Angle = 360
  AttacherType = Attacher::AttachEngine3D
  FirstAngle = 0
  Height = 16
  Placement = pos=(0,85,0) rot=(-1,0,0;1.5708rad)
  Radius = 12
  SecondAngle = 0
FEATURE [Part::Cylinder] Cylinder949
  Angle = 360
  AttacherType = Attacher::AttachEngine3D
  FirstAngle = 0
  Height = 4.2
  Placement = pos=(0,47.5,0) rot=(-1,0,0;1.5708rad)
  Radius = 4.6
  SecondAngle = 0
FEATURE [Part::Cylinder] Cylinder950
  Angle = 360
  AttacherType = Attacher::AttachEngine3D
  FirstAngle = 0
  Height = 4.2
  Placement = pos=(0,134.3,0) rot=(-1,0,0;1.5708rad)
  Radius = 4.6
  SecondAngle = 0
FEATURE [Part::Cylinder] Cylinder951
  Angle = 360
  AttacherType = Attacher::AttachEngine3D
  FirstAngle = 0
  Height = 96
  Placement = pos=(0,45,0) rot=(-1,0,0;1.5708rad)
  Radius = 3
  SecondAngle = 0
FEATURE [Part::Cylinder] Cylinder952  label="Cylinder"
  Angle = 360
  AttacherType = Attacher::AttachEngine3D
  FirstAngle = 0
  Height = 20
  Placement = pos=(79.25,35,36) rot=(0,0,1;0rad)
  Radius = 1
  SecondAngle = 0
FEATURE [Part::Cylinder] Cylinder953  label="Cylinder"
  Angle = 360
  AttacherType = Attacher::AttachEngine3D
  FirstAngle = 0
  Height = 20
  Placement = pos=(70.75,35,36) rot=(0,0,1;0rad)
  Radius = 1
  SecondAngle = 0
FEATURE [Part::Cylinder] Cylinder954  label="Cylinder"
  Angle = 360
  AttacherType = Attacher::AttachEngine3D
  FirstAngle = 0
  Height = 20
  Placement = pos=(70.75,40,36) rot=(0,0,1;0rad)
  Radius = 1
  SecondAngle = 0
FEATURE [Part::Cylinder] Cylinder955  label="Cylinder"
  Angle = 360
  AttacherType = Attacher::AttachEngine3D
  FirstAngle = 0
  Height = 20
  Placement = pos=(79.25,40,36) rot=(0,0,1;0rad)
  Radius = 1
  SecondAngle = 0
FEATURE [Part::Cylinder] Cylinder956  label="Cylinder"
  Angle = 360
  AttacherType = Attacher::AttachEngine3D
  FirstAngle = 0
  Height = 20
  Placement = pos=(79.25,-35,36) rot=(0,0,1;0rad)
  Radius = 1
  SecondAngle = 0
FEATURE [Part::Cylinder] Cylinder957  label="Cylinder"
  Angle = 360
  AttacherType = Attacher::AttachEngine3D
  FirstAngle = 0
  Height = 20
  Placement = pos=(70.75,-35,36) rot=(0,0,1;0rad)
  Radius = 1
  SecondAngle = 0
FEATURE [Part::Cylinder] Cylinder958  label="Cylinder"
  Angle = 360
  AttacherType = Attacher::AttachEngine3D
  FirstAngle = 0
  Height = 20
  Placement = pos=(79.25,-40,36) rot=(0,0,1;0rad)
  Radius = 1
  SecondAngle = 0
FEATURE [Part::Cylinder] Cylinder959  label="Cylinder"
  Angle = 360
  AttacherType = Attacher::AttachEngine3D
  FirstAngle = 0
  Height = 20
  Placement = pos=(70.75,-40,36) rot=(0,0,1;0rad)
  Radius = 1
  SecondAngle = 0
FEATURE [Part::Cylinder] Cylinder960  label="Cylinder"
  Angle = 360
  AttacherType = Attacher::AttachEngine3D
  FirstAngle = 0
  Height = 3
  Placement = pos=(91,0,46) rot=(0,1,0;1.5708rad)
  Radius = 8.5
  SecondAngle = 0
FEATURE [Part::Cylinder] Cylinder961  label="Cylinder"
  Angle = 360
  AttacherType = Attacher::AttachEngine3D
  FirstAngle = 0
  Height = 3
  Placement = pos=(91,0,46) rot=(0,1,0;1.5708rad)
  Radius = 7.5
  SecondAngle = 0
FEATURE [Part::Cut] Cut176013009033007019019008010045003002004008006021005004004004004002012032  label="Cut"
  Base = -> Cylinder960
  Refine = true
  Tool = -> Cylinder961
FEATURE [Part::Chamfer] Chamfer228036
  Base = -> Cut176013009033007019019008010045003002004008006021005004004004004002012032
  Edges = 1 edges r=0.9: [Edge4]
FEATURE [Part::Feature] Fusion088026007031024007008004100051009001012006005048  label="SCREW-S-T-M2x014"
  Placement = pos=(68,12,56) rot=(0,0,1;0rad)
  shape: bbox 19 x 4 x 4 mm, 7 faces (baked)
FEATURE [Part::Feature] Fusion088026007031024007008004100051009001012006005049  label="SCREW-S-T-M2x014"
  Placement = pos=(68,-12,56) rot=(0,0,1;0rad)
  shape: bbox 19 x 4 x 4 mm, 7 faces (baked)
FEATURE [Part::Feature] Fusion088026007031024007008004100051009001012006005050  label="SCREW-S-T-M2x014"
  Placement = pos=(68,-12,36) rot=(0,0,1;0rad)
  shape: bbox 19 x 4 x 4 mm, 7 faces (baked)
FEATURE [Part::Feature] Fusion088026007031024007008004100051009001012006005051  label="SCREW-S-T-M2x014"
  Placement = pos=(68,12,36) rot=(0,0,1;0rad)
  shape: bbox 19 x 4 x 4 mm, 7 faces (baked)
FEATURE [Part::Feature] Fusion088026007031024007008004100051009001012006005052  label="SCREW-S-T-M2x10"
  Placement = pos=(70,29,51.75) rot=(0,0,1;0rad)
  shape: bbox 15 x 3.6 x 3.6 mm, 7 faces (baked)
FEATURE [Part::Feature] Fusion088026007031024007008004100051009001012006005053  label="SCREW-S-T-M2x10"
  Placement = pos=(70,29,40.25) rot=(0,0,1;0rad)
  shape: bbox 15 x 3.6 x 3.6 mm, 7 faces (baked)
FEATURE [Part::Feature] Fusion088026007031024007008004100051009001012006005054  label="SCREW-S-T-M2x10"
  Placement = pos=(70,-29,40.25) rot=(0,0,1;0rad)
  shape: bbox 15 x 3.6 x 3.6 mm, 7 faces (baked)
FEATURE [Part::Feature] Fusion088026007031024007008004100051009001012006005055  label="SCREW-S-T-M2x10"
  Placement = pos=(70,-29,51.75) rot=(0,0,1;0rad)
  shape: bbox 15 x 3.6 x 3.6 mm, 7 faces (baked)
FEATURE [Part::MultiFuse] Fusion088026007031024007008004100051009001012006005056  label="screws-rear"
  Refine = true
  Shapes = -> [Fusion088026007031024007008004100051009001012006005055,Fusion088026007031024007008004100051009001012006005048,Fusion088026007031024007008004100051009001012006005049,Fusion088026007031024007008004100051009001012006005050,Fusion088026007031024007008004100051009001012006005051,Fusion088026007031024007008004100051009001012006005052,Fusion088026007031024007008004100051009001012006005053,+1 more]
FEATURE [Part::MultiFuse] Fusion088026007031024007008004100051009001012006005057  label="holes-rear"
  Refine = true
  Shapes = -> [Cylinder959,Cylinder952,Cylinder953,Cylinder954,Cylinder955,Cylinder956,Cylinder957,Cylinder958]
FEATURE [Part::MultiFuse] Fusion088026007031024007008004100051009001012006005058  label="pinion-bearings-carving002"
  Placement = pos=(7.5,41,7.5) rot=(0,1,0;3.14159rad)
  Refine = true
  Shapes = -> [Cylinder946,Cylinder944,Cylinder945,Cylinder947]
FEATURE [Part::MultiFuse] Fusion088026007031024007008004100051009001012006005047  label="inner-carving-rear"
  Placement = pos=(75,-93,46) rot=(0,0,1;0rad)
  Refine = true
  Shapes = -> [Cylinder951,Chamfer228034,Fusion088026007031024007008004100051009001012006005058,Chamfer228035,Cylinder948,Cylinder949,Cylinder950]
FEATURE [Part::Box] Box346  label="Cube261"
  AttacherType = Attacher::AttachEngine3D
  Height = 3.5
  Length = 14
  Placement = pos=(68,32.5,51.5) rot=(0,0,1;0rad)
  Width = 25
FEATURE [Part::Cylinder] Cylinder964  label="Cylinder741"
  Angle = 360
  AttacherType = Attacher::AttachEngine3D
  FirstAngle = 0
  Height = 1.4
  Placement = pos=(75,53.5,53.6) rot=(0,0,1;0rad)
  Radius = 8
  SecondAngle = 0
FEATURE [Part::Cylinder] Cylinder969  label="Cylinder"
  Angle = 360
  AttacherType = Attacher::AttachEngine3D
  FirstAngle = 0
  Height = 25
  Placement = pos=(75,57.5,46) rot=(1,0,0;1.5708rad)
  Radius = 9
  SecondAngle = 0
FEATURE [Part::Cut] Cut176013009033007019019008010045003002004008006021005004004004004002012033005  label="Cut"
  Base = -> Box346
  Refine = true
  Tool = -> Cylinder969
FEATURE [Part::MultiFuse] Fusion088026007031024007008004100051009001012006005067  label="rear-axle-carvings"
  Refine = true
  Shapes = -> [Chamfer228036,Fusion088026007031024007008004100051009001012006005047,Fusion088026007031024007008004100051009001012006005056,Fusion088026007031024007008004100051009001012006005057]
FEATURE [Part::Feature] Cut176013009033007019019008010045003002004008006021005004004004004002012033009001  label="rear-axle-base-carved"
  shape: bbox 39 x 96 x 28 mm, 141 faces (baked)
FEATURE [Part::Box] Box347  label="Cube"
  AttacherType = Attacher::AttachEngine3D
  Height = 28
  Length = 17
  Placement = pos=(58,-50,32) rot=(0,0,1;0rad)
  Width = 100
FEATURE [Part::Box] Box348  label="Cube"
  AttacherType = Attacher::AttachEngine3D
  Height = 28
  Length = 22
  Placement = pos=(75,-50,32) rot=(0,0,1;0rad)
  Width = 100
FEATURE [Part::Cut] Cut176013009033007019019008010045003002004008006021005004004004004002012033009003  label="rear-axle-pinion-side"
  Base = -> Cut176013009033007019019008010045003002004008006021005004004004004002012033009001
  Refine = true
  Tool = -> Box347
FEATURE [Part::Box] Box351  label="Cube"
  AttacherType = Attacher::AttachEngine3D
  Height = 10
  Length = 10
  Placement = pos=(255,-14,55) rot=(0,0,1;0rad)
  Width = 22
FEATURE [Part::Box] Box352  label="Cube"
  AttacherType = Attacher::AttachEngine3D
  Height = 10
  Length = 10
  Placement = pos=(255,8,55) rot=(0,0,1;0rad)
  Width = 6
FEATURE [Part::Box] Box353  label="Cube"
  AttacherType = Attacher::AttachEngine3D
  Height = 10.4
  Length = 10.4
  Placement = pos=(254.8,8,54.8) rot=(0,0,1;0rad)
  Width = 6
FEATURE [Part::Box] Box354  label="Cube"
  AttacherType = Attacher::AttachEngine3D
  Height = 10.4
  Length = 10.4
  Placement = pos=(254.8,-14,54.8) rot=(0,0,1;0rad)
  Width = 6
FEATURE [Part::Cylinder] Cylinder997  label="Cylinder"
  Angle = 360
  AttacherType = Attacher::AttachEngine3D
  FirstAngle = 0
  Height = 8
  Placement = pos=(260,-16,60) rot=(-1,0,0;1.5708rad)
  Radius = 2.5
  SecondAngle = 0
FEATURE [Part::Cylinder] Cylinder998  label="Cylinder"
  Angle = 360
  AttacherType = Attacher::AttachEngine3D
  FirstAngle = 0
  Height = 8
  Placement = pos=(260,8,60) rot=(-1,0,0;1.5708rad)
  Radius = 2.5
  SecondAngle = 0
FEATURE [Part::Feature] Diff_Gear_35T_pitch160001001003_solid  label="Diff_Gear_35T_pitch160"
  shape: bbox 32.85 x 8 x 32.88 mm, 1956 faces (baked)
FEATURE [Part::Feature] Diff_Gear_35T_pitch160001001003_solid001  label="Diff_Gear_35T_pitch160"
  Placement = pos=(0,24,0) rot=(0,0,1;0rad)
  shape: bbox 32.85 x 8 x 32.88 mm, 1956 faces (baked)
FEATURE [Part::MultiFuse] Fusion088026007031024007008004100051009001012006005074  label="Fusion"
  Refine = true
  Shapes = -> [Box353,Cylinder998]
FEATURE [Part::MultiFuse] Fusion088026007031024007008004100051009001012006005075  label="Fusion"
  Refine = true
  Shapes = -> [Box354,Cylinder997]
FEATURE [Part::Cut] Cut176013009033007019019008010045003002004008006021005004004004004002012033009009  label="diff_front_gear_right"
  Base = -> Diff_Gear_35T_pitch160001001003_solid
  Refine = true
  Tool = -> Fusion088026007031024007008004100051009001012006005075
FEATURE [Part::Cut] Cut176013009033007019019008010045003002004008006021005004004004004002012033009010  label="Cut"
  Base = -> Diff_Gear_35T_pitch160001001003_solid001
  Refine = true
  Tool = -> Fusion088026007031024007008004100051009001012006005074
FEATURE [Part::Cylinder] Cylinder999  label="Cylinder"
  Angle = 360
  AttacherType = Attacher::AttachEngine3D
  FirstAngle = 0
  Height = 8
  Placement = pos=(260,68,60) rot=(-1,0,0;1.5708rad)
  Radius = 8
  SecondAngle = 0
FEATURE [Part::Feature] Fusion088026007031024007008004100051055007010008005001  label="front-hub-screws"
  Placement = pos=(260,97,60) rot=(0,0,1;3.14159rad)
  shape: bbox 23.97 x 16 x 25 mm, 70 faces, 10 solids (baked)
FEATURE [Part::Cylinder] Cylinder1000  label="Cylinder"
  Angle = 360
  AttacherType = Attacher::AttachEngine3D
  FirstAngle = 0
  Height = 3
  Placement = pos=(260,66,60) rot=(-1,0,0;1.5708rad)
  Radius = 15
  SecondAngle = 0
FEATURE [Part::Cylinder] Cylinder1001  label="Cylinder"
  Angle = 360
  AttacherType = Attacher::AttachEngine3D
  FirstAngle = 0
  Height = 4
  Placement = pos=(260,62,60) rot=(-1,0,0;1.5708rad)
  Radius = 15
  SecondAngle = 0
FEATURE [Part::Feature] Fusion088026007031024007008004100051018001  label="axle-rod-lock-SHAPE"
  Placement = pos=(260,69.5,60) rot=(-1,0,0;1.5708rad)
  shape: bbox 11.6 x 10 x 5.628 mm, 19 faces (baked)
FEATURE [Part::Cylinder] Cylinder1002  label="Cylinder"
  Angle = 360
  AttacherType = Attacher::AttachEngine3D
  FirstAngle = 0
  Height = 6
  Placement = pos=(260,70,60) rot=(-1,0,0;1.5708rad)
  Radius = 6
  SecondAngle = 0
FEATURE [Part::MultiFuse] Fusion088026007031024007008004100051055007010008005002  label="Fusion"
  Refine = true
  Shapes = -> [Cylinder1000,Cylinder999]
FEATURE [Part::Cut] Cut176013009033007019019008010045003002004008006021005004004004004002012033009011  label="Cut"
  Base = -> Fusion088026007031024007008004100051055007010008005002
  Refine = true
  Tool = -> Cylinder1002
FEATURE [Part::Cut] Cut176013009033007019019008010045003002004008006021005004004004004002012033009012  label="Cut"
  Base = -> Cut176013009033007019019008010045003002004008006021005004004004004002012033009011
  Refine = true
  Tool = -> Fusion088026007031024007008004100051018001
FEATURE [Part::Cylinder] Cylinder1003  label="Cylinder"
  Angle = 360
  AttacherType = Attacher::AttachEngine3D
  FirstAngle = 0
  Height = 4
  Placement = pos=(260,62,60) rot=(-1,0,0;1.5708rad)
  Radius = 5.6
  SecondAngle = 0
FEATURE [Part::Cut] Cut176013009033007019019008010045003002004008006021005004004004004002012033009013  label="Cut"
  Base = -> Cylinder1001
  Refine = true
  Tool = -> Cylinder1003
FEATURE [Part::Chamfer] Chamfer228039
  Base = -> Cut176013009033007019019008010045003002004008006021005004004004004002012033009013
  Edges = 1 edges r=2.99: [Edge2]
  Placement = pos=(0,0,2) rot=(0,0,1;0rad)
FEATURE [Part::Feature] Fusion088026007031024007008004100051055007010008005003  label="front-hub-screws"
  Placement = pos=(260,97,62) rot=(0,0,1;3.14159rad)
  shape: bbox 23.97 x 16 x 25 mm, 70 faces, 10 solids (baked)
FEATURE [Part::Cut] Cut176013009033007019019008010045003002004008006021005004004004004002012033009014  label="front-hub-external-left"
  Base = -> Cut176013009033007019019008010045003002004008006021005004004004004002012033009012
  Placement = pos=(0,0,2) rot=(0,0,1;0rad)
  Refine = true
  Tool = -> Fusion088026007031024007008004100051055007010008005001
FEATURE [Part::Cylinder] Cylinder1004  label="Cylinder"
  Angle = 360
  AttacherType = Attacher::AttachEngine3D
  FirstAngle = 0
  Height = 4
  Placement = pos=(75,69,46) rot=(1,0,0;1.5708rad)
  Radius = 5.5
  SecondAngle = 0
FEATURE [Part::Cylinder] Cylinder1005  label="Cylinder"
  Angle = 360
  AttacherType = Attacher::AttachEngine3D
  FirstAngle = 0
  Height = 4
  Placement = pos=(75,69,46) rot=(1,0,0;1.5708rad)
  Radius = 2.5
  SecondAngle = 0
FEATURE [Part::Cut] Cut176013009033007019019008010045003002004008006021005004004004004002012033009016  label="BUSH-5x11x4"
  Base = -> Cylinder1004
  Refine = true
  Tool = -> Cylinder1005
FEATURE [Part::Feature] Cut176013009033007019019008010045003002004008006021005004004004004002012033009016001  label="BUSH-5x11x4"
  Placement = pos=(185,-3,16) rot=(0,0,1;0rad)
  shape: bbox 11 x 4 x 11 mm, 4 faces (baked)
FEATURE [Part::Cylinder] Cylinder1006  label="Cylinder"
  Angle = 360
  AttacherType = Attacher::AttachEngine3D
  FirstAngle = 0
  Height = 2.5
  Placement = pos=(75,69,46) rot=(1,0,0;1.5708rad)
  Radius = 4
  SecondAngle = 0
FEATURE [Part::Cylinder] Cylinder1007  label="Cylinder"
  Angle = 360
  AttacherType = Attacher::AttachEngine3D
  FirstAngle = 0
  Height = 2.5
  Placement = pos=(75,69,46) rot=(1,0,0;1.5708rad)
  Radius = 2.5
  SecondAngle = 0
FEATURE [Part::Cut] Cut176013009033007019019008010045003002004008006021005004004004004002012033009016002  label="BEARING-5x8x2.5-MR85ZZ"
  Base = -> Cylinder1006
  Refine = true
  Tool = -> Cylinder1007
FEATURE [Part::Cylinder] Cylinder1008  label="Cylinder"
  Angle = 360
  AttacherType = Attacher::AttachEngine3D
  FirstAngle = 0
  Height = 2.5
  Placement = pos=(260,8,60) rot=(1,0,0;1.5708rad)
  Radius = 4
  SecondAngle = 0
FEATURE [Part::Cylinder] Cylinder1009  label="Cylinder"
  Angle = 360
  AttacherType = Attacher::AttachEngine3D
  FirstAngle = 0
  Height = 22
  Placement = pos=(260,8,60) rot=(1,0,0;1.5708rad)
  Radius = 2.5
  SecondAngle = 0
FEATURE [Part::MultiFuse] Fusion088026007031024007008004100051055007010008005004  label="Fusion"
  Refine = true
  Shapes = -> [Cylinder1009,Cylinder1008]
FEATURE [Part::Cut] Cut176013009033007019019008010045003002004008006021005004004004004002012033009016002002  label="diff_front_gear_lock_right"
  Base = -> Box351
  Placement = pos=(0,0,2) rot=(0,0,1;0rad)
  Refine = true
  Tool = -> Fusion088026007031024007008004100051055007010008005004
FEATURE [Part::Cylinder] Cylinder1010  label="Cylinder"
  Angle = 360
  AttacherType = Attacher::AttachEngine3D
  FirstAngle = 0
  Height = 6
  Placement = pos=(260,14,60) rot=(1,0,0;1.5708rad)
  Radius = 2.5
  SecondAngle = 0
FEATURE [Part::Cut] Cut176013009033007019019008010045003002004008006021005004004004004002012033009016002003  label="diff_front_gear_lock_left"
  Base = -> Box352
  Placement = pos=(0,0,2) rot=(0,0,1;0rad)
  Refine = true
  Tool = -> Cylinder1010
FEATURE [Part::Box] Box355  label="Cube"
  AttacherType = Attacher::AttachEngine3D
  Height = 10
  Length = 10
  Placement = pos=(255,8,55) rot=(0,0,1;0rad)
  Width = 4.5
FEATURE [Part::Cylinder] Cylinder1011  label="Cylinder"
  Angle = 360
  AttacherType = Attacher::AttachEngine3D
  FirstAngle = 0
  Height = 6
  Placement = pos=(260,14,60) rot=(1,0,0;1.5708rad)
  Radius = 2.5
  SecondAngle = 0
FEATURE [Part::Cut] Cut176013009033007019019008010045003002004008006021005004004004004002012033009016002004  label="diff_rear_gear_lock_left"
  Base = -> Box355
  Placement = pos=(-31,3.5,-5) rot=(0,0,1;0rad)
  Refine = true
  Tool = -> Cylinder1011
FEATURE [Part::Box] Box356  label="Cube"
  AttacherType = Attacher::AttachEngine3D
  Height = 10.4
  Length = 10.4
  Placement = pos=(228.8,8,47.8) rot=(0,0,1;0rad)
  Width = 8
FEATURE [Part::Cylinder] Cylinder1012  label="Cylinder"
  Angle = 360
  AttacherType = Attacher::AttachEngine3D
  FirstAngle = 0
  Height = 3.5
  Placement = pos=(234,11.5,53) rot=(1,0,0;1.5708rad)
  Radius = 6.2
  SecondAngle = 0
FEATURE [Part::MultiFuse] Fusion088026007031024007008004100051055007010008005005  label="Fusion"
  Refine = true
  Shapes = -> [Box356,Cylinder1012]
FEATURE [Part::Feature] Diff_Gear_26T_pitch160001001003_solid  label="Diff_Gear_26T_pitch160"
  Placement = pos=(0,0,53) rot=(0,0,1;0rad)
  shape: bbox 24.88 x 8 x 24.78 mm, 1452 faces (baked)
FEATURE [Part::Feature] Diff_Gear_26T_pitch160001001003_solid001  label="Diff_Gear_26T_pitch160"
  Placement = pos=(0,-24,53) rot=(0,0,1;0rad)
  shape: bbox 24.88 x 8 x 24.78 mm, 1452 faces (baked)
FEATURE [Part::Cut] Cut176013009033007019019008010045003002004008006021005004004004004002012033009016002005  label="diff_rear_gear_left"
  Base = -> Diff_Gear_26T_pitch160001001003_solid
  Refine = true
  Tool = -> Fusion088026007031024007008004100051055007010008005005
FEATURE [Part::Box] Box357  label="Cube"
  AttacherType = Attacher::AttachEngine3D
  Height = 10.4
  Length = 10.4
  Placement = pos=(228.8,-16,47.8) rot=(0,0,1;0rad)
  Width = 8
FEATURE [Part::Cylinder] Cylinder1013  label="Cylinder"
  Angle = 360
  AttacherType = Attacher::AttachEngine3D
  FirstAngle = 0
  Height = 3.5
  Placement = pos=(234,-8,53) rot=(1,0,0;1.5708rad)
  Radius = 6.2
  SecondAngle = 0
FEATURE [Part::MultiFuse] Fusion088026007031024007008004100051055007010008005006  label="Fusion"
  Refine = true
  Shapes = -> [Box357,Cylinder1013]
FEATURE [Part::Cut] Cut176013009033007019019008010045003002004008006021005004004004004002012033009016002006  label="diff_rear_gear_right"
  Base = -> Diff_Gear_26T_pitch160001001003_solid001
  Refine = true
  Tool = -> Fusion088026007031024007008004100051055007010008005006
FEATURE [Part::Box] Box358  label="Cube"
  AttacherType = Attacher::AttachEngine3D
  Height = 10
  Length = 10
  Placement = pos=(255,8,55) rot=(0,0,1;0rad)
  Width = 4.5
FEATURE [Part::Cylinder] Cylinder1014  label="Cylinder"
  Angle = 360
  AttacherType = Attacher::AttachEngine3D
  FirstAngle = 0
  Height = 6
  Placement = pos=(260,14,60) rot=(1,0,0;1.5708rad)
  Radius = 2.5
  SecondAngle = 0
FEATURE [Part::Cut] Cut176013009033007019019008010045003002004008006021005004004004004002012033009016002007  label="diff_rear_gear_lock_right"
  Base = -> Box358
  Placement = pos=(-31,-24,-5) rot=(0,0,1;0rad)
  Refine = true
  Tool = -> Cylinder1014
FEATURE [Part::Box] Box361  label="Cube"
  AttacherType = Attacher::AttachEngine3D
  Height = 24
  Length = 24
  Placement = pos=(248,21,48) rot=(0,0,1;0rad)
  Width = 34
FEATURE [Part::Cylinder] Cylinder1015  label="Cylinder"
  Angle = 360
  AttacherType = Attacher::AttachEngine3D
  FirstAngle = 0
  Height = 7.5
  Placement = pos=(260,54,62) rot=(-1,0,0;1.5708rad)
  Radius = 11.5
  SecondAngle = 0
FEATURE [Part::Cylinder] Cylinder1016  label="Cylinder"
  Angle = 360
  AttacherType = Attacher::AttachEngine3D
  FirstAngle = 0
  Height = 2
  Placement = pos=(260,21,62) rot=(-1,0,0;1.5708rad)
  Radius = 19
  SecondAngle = 0
FEATURE [Part::Cylinder] Cylinder1017  label="Cylinder"
  Angle = 360
  AttacherType = Attacher::AttachEngine3D
  FirstAngle = 0
  Height = 2
  Placement = pos=(260,22.5,62) rot=(-1,0,0;1.5708rad)
  Radius = 17
  SecondAngle = 0
FEATURE [Part::Fillet] Fillet125007020032034
  Base = -> Cylinder1017
  Edges = 1 edges r=1.99: [Edge3]
FEATURE [Part::Fillet] Fillet125007020032035
  Base = -> Box361
  Edges = 4 edges r=5: [Edge2,Edge4,Edge6,Edge8]
FEATURE [Part::Fillet] Fillet125007020032036
  Base = -> Fillet125007020032035
  Edges = 4 edges r=1: [Edge3,Edge16,Edge17,Edge19]
  Placement = pos=(0,0,2) rot=(0,0,1;0rad)
FEATURE [Part::Cylinder] Cylinder1022  label="Cylinder"
  Angle = 360
  AttacherType = Attacher::AttachEngine3D
  FirstAngle = 0
  Height = 2
  Placement = pos=(260,5,70.5) rot=(-1,0,0;1.5708rad)
  Radius = 2
  SecondAngle = 0
FEATURE [Part::Cylinder] Cylinder1023  label="Cylinder"
  Angle = 360
  AttacherType = Attacher::AttachEngine3D
  FirstAngle = 0
  Height = 2
  Placement = pos=(269.093,5,54.75) rot=(-0.377964,0.654654,0.654654;2.41886rad)
  Radius = 2
  SecondAngle = 0
FEATURE [Part::Cylinder] Cylinder1024  label="Cylinder"
  Angle = 360
  AttacherType = Attacher::AttachEngine3D
  FirstAngle = 0
  Height = 2
  Placement = pos=(250.907,5,54.75) rot=(0.377964,0.654654,0.654654;3.86433rad)
  Radius = 2
  SecondAngle = 0
FEATURE [Part::MultiFuse] Fusion088026007031024007008004100051055007010008005010  label="Fusion"
  Refine = true
  Shapes = -> [Cylinder1022,Cylinder1023,Cylinder1024]
FEATURE [Part::Cylinder] Cylinder1025  label="Cylinder"
  Angle = 360
  AttacherType = Attacher::AttachEngine3D
  FirstAngle = 0
  Height = 8
  Placement = pos=(260,5,70.5) rot=(-1,0,0;1.5708rad)
  Radius = 1
  SecondAngle = 0
FEATURE [Part::Cylinder] Cylinder1026  label="Cylinder"
  Angle = 360
  AttacherType = Attacher::AttachEngine3D
  FirstAngle = 0
  Height = 8
  Placement = pos=(269.093,5,54.75) rot=(-0.377964,0.654654,0.654654;2.41886rad)
  Radius = 1
  SecondAngle = 0
FEATURE [Part::Cylinder] Cylinder1027  label="Cylinder"
  Angle = 360
  AttacherType = Attacher::AttachEngine3D
  FirstAngle = 0
  Height = 8
  Placement = pos=(250.907,5,54.75) rot=(0.377964,0.654654,0.654654;3.86433rad)
  Radius = 1
  SecondAngle = 0
FEATURE [Part::MultiFuse] Fusion088026007031024007008004100051055007010008005011  label="Fusion"
  Refine = true
  Shapes = -> [Cylinder1025,Cylinder1026,Cylinder1027]
FEATURE [Part::Cylinder] Cylinder1028  label="Cylinder"
  Angle = 360
  AttacherType = Attacher::AttachEngine3D
  FirstAngle = 0
  Height = 6
  Placement = pos=(260,5,70.5) rot=(-1,0,0;1.5708rad)
  Radius = 0.9
  SecondAngle = 0
FEATURE [Part::Cylinder] Cylinder1029  label="Cylinder"
  Angle = 360
  AttacherType = Attacher::AttachEngine3D
  FirstAngle = 0
  Height = 6
  Placement = pos=(269.093,5,54.75) rot=(-0.377964,0.654654,0.654654;2.41886rad)
  Radius = 0.9
  SecondAngle = 0
FEATURE [Part::Cylinder] Cylinder1030  label="Cylinder"
  Angle = 360
  AttacherType = Attacher::AttachEngine3D
  FirstAngle = 0
  Height = 6
  Placement = pos=(250.907,5,54.75) rot=(0.377964,0.654654,0.654654;3.86433rad)
  Radius = 0.9
  SecondAngle = 0
FEATURE [Part::MultiFuse] Fusion088026007031024007008004100051055007010008005012  label="Fusion"
  Placement = pos=(0,3,0) rot=(0,0,1;0rad)
  Refine = true
  Shapes = -> [Cylinder1028,Cylinder1029,Cylinder1030]
FEATURE [Part::MultiFuse] Fusion088026007031024007008004100051055007010008005013  label="diff_front_gear_lock_screws"
  Placement = pos=(0,1,2) rot=(0,0,1;0rad)
  Refine = true
  Shapes = -> [Fusion088026007031024007008004100051055007010008005011,Fusion088026007031024007008004100051055007010008005010]
FEATURE [Part::Cut] Cut176013009033007019019008010045003002004008006021005004004004004002012033009016002012  label="diff_front_gear_left"
  Base = -> Cut176013009033007019019008010045003002004008006021005004004004004002012033009010
  Refine = true
  Tool = -> Fusion088026007031024007008004100051055007010008005012
FEATURE [Part::Part2DObjectPython] Line019  label="front-wheels-diff-path"  # Draft 2D object (typed FeaturePython)
  Closed = true
  End = (228.5,70,55)
  FilletRadius = 0
  MapMode = 5
  Placement = pos=(228.5,-70,55) rot=(0,0,1;0rad)
  Points = (2) [(0,0,0),(0,140,0)]
  Start = (228.5,-70,55)
FEATURE [Part::Cylinder] Cylinder1042  label="Cylinder"
  Angle = 360
  AttacherType = Attacher::AttachEngine3D
  FirstAngle = 0
  Height = 69
  Placement = pos=(260,0,60) rot=(-1,0,0;1.5708rad)
  Radius = 2.5
  SecondAngle = 0
FEATURE [Part::Cylinder] Cylinder1043  label="Cylinder"
  Angle = 360
  AttacherType = Attacher::AttachEngine3D
  FirstAngle = 0
  Height = 6
  Placement = pos=(260,69,60) rot=(-1,0,0;1.5708rad)
  Radius = 2
  SecondAngle = 0
FEATURE [Part::Cylinder] Cylinder1044  label="Cylinder"
  Angle = 360
  AttacherType = Attacher::AttachEngine3D
  FirstAngle = 0
  Height = 10
  Placement = pos=(255,67.5,60) rot=(0,1,0;1.5708rad)
  Radius = 1
  SecondAngle = 0
FEATURE [Part::MultiFuse] Fusion088026007031024007008004100051055007010008005020  label="front-axle-rod"
  Refine = true
  Shapes = -> [Cylinder1042,Cylinder1043,Cylinder1044]
FEATURE [Part::Feature] Fusion088026007031024007008004100051055007010008005020001  label="front-axle-rod-left"
  Placement = pos=(0,0,2) rot=(0,0,1;0rad)
  shape: bbox 10 x 75 x 5 mm, 9 faces (baked)
FEATURE [Part::Feature] Part__Mirroring007002003002018002002002002  label="front-axle-rod-right"
  Placement = pos=(0,0,2) rot=(0,0,1;0rad)
  shape: bbox 10 x 75 x 5 mm, 9 faces (baked)
FEATURE [Part::Feature] Cut176013009033007019019008010045003002004008006021005004004004004002012033009016002012014  label="BEARING-5x9x3-MR95ZZ"
  Placement = pos=(185,-100,16) rot=(0,0,1;0rad)
  shape: bbox 9 x 3 x 9 mm, 4 faces (baked)
FEATURE [Part::Feature] Cut176013009033007019019008010045003002004008006021005004004004004002012033009016002012015  label="BEARING-5x9x3-MR95ZZ"
  Placement = pos=(185,-35,16) rot=(0,0,1;0rad)
  shape: bbox 9 x 3 x 9 mm, 4 faces (baked)
FEATURE [Part::Box] Box367  label="Cube"
  AttacherType = Attacher::AttachEngine3D
  Height = 2
  Length = 4
  Placement = pos=(73,52,49) rot=(0,0,1;0rad)
  Width = 7
FEATURE [Part::Box] Box368  label="Cube"
  AttacherType = Attacher::AttachEngine3D
  Height = 4
  Length = 2
  Placement = pos=(70,55,44) rot=(0,0,1;0rad)
  Width = 7
FEATURE [Part::Box] Box369  label="Cube"
  AttacherType = Attacher::AttachEngine3D
  Height = 2
  Length = 4
  Placement = pos=(73,52,41) rot=(0,0,1;0rad)
  Width = 7
FEATURE [Part::Box] Box370  label="Cube"
  AttacherType = Attacher::AttachEngine3D
  Height = 4
  Length = 2
  Placement = pos=(78,55,44) rot=(0,0,1;0rad)
  Width = 7
FEATURE [Part::Box] Box371  label="Cube"
  AttacherType = Attacher::AttachEngine3D
  Height = 5
  Length = 5
  Placement = pos=(72.5,55,43.5) rot=(0,0,1;0rad)
  Width = 4
FEATURE [Part::Cylinder] Cylinder1045  label="Cylinder"
  Angle = 360
  AttacherType = Attacher::AttachEngine3D
  FirstAngle = 0
  Height = 11
  Placement = pos=(75,57,40.5) rot=(0,0,1;1.5708rad)
  Radius = 1
  SecondAngle = 0
FEATURE [Part::Cylinder] Cylinder1046  label="Cylinder"
  Angle = 360
  AttacherType = Attacher::AttachEngine3D
  FirstAngle = 0
  Height = 9
  Placement = pos=(75,69,46) rot=(1,0,0;1.5708rad)
  Radius = 5.5
  SecondAngle = 0
FEATURE [Part::Cylinder] Cylinder1047  label="Cylinder"
  Angle = 360
  AttacherType = Attacher::AttachEngine3D
  FirstAngle = 0
  Height = 9
  Placement = pos=(75,54,46) rot=(1,0,0;1.5708rad)
  Radius = 5.5
  SecondAngle = 0
FEATURE [Part::Cylinder] Cylinder1048  label="Cylinder"
  Angle = 360
  AttacherType = Attacher::AttachEngine3D
  FirstAngle = 0
  Height = 9
  Placement = pos=(75,69,46) rot=(1,0,0;1.5708rad)
  Radius = 2.5
  SecondAngle = 0
FEATURE [Part::Cylinder] Cylinder1049  label="Cylinder"
  Angle = 360
  AttacherType = Attacher::AttachEngine3D
  FirstAngle = 0
  Height = 11
  Placement = pos=(69.5,57,46) rot=(0,1,0;1.5708rad)
  Radius = 1
  SecondAngle = 0
FEATURE [Part::Cylinder] Cylinder1050  label="Cylinder"
  Angle = 360
  AttacherType = Attacher::AttachEngine3D
  FirstAngle = 0
  Height = 9
  Placement = pos=(75,54,46) rot=(1,0,0;1.5708rad)
  Radius = 2.5
  SecondAngle = 0
FEATURE [Part::MultiFuse] Fusion088026007031024007008004100051055007010008005020004  label="Fusion"
  Refine = true
  Shapes = -> [Box367,Box369,Box371,Cylinder1045,Cylinder1047,Cylinder1049]
FEATURE [Part::Cut] Cut176013009033007019019008010045003002004008006021005004004004004002012033009016002012016  label="Cut"
  Base = -> Fusion088026007031024007008004100051055007010008005020004
  Placement = pos=(0,-57,0) rot=(0,0,1;0rad)
  Refine = true
  Tool = -> Cylinder1050
FEATURE [Part::MultiFuse] Fusion088026007031024007008004100051055007010008005020005  label="Fusion"
  Refine = true
  Shapes = -> [Box368,Box370,Cylinder1046]
FEATURE [Part::Cut] Cut176013009033007019019008010045003002004008006021005004004004004002012033009016002012017  label="Cut"
  Base = -> Fusion088026007031024007008004100051055007010008005020005
  Placement = pos=(0,-57,0) rot=(0,0,1;0rad)
  Refine = true
  Tool = -> Cylinder1048
FEATURE [Part::Fillet] Fillet125007020032038
  Base = -> Cut176013009033007019019008010045003002004008006021005004004004004002012033009016002012017
  Edges = 4 edges r=1: [Edge7,Edge17,Edge27,Edge29]
  Placement = pos=(86.9057,-75,1.56741) rot=(-0.129428,-0.129428,0.983106;1.58783rad)
FEATURE [Part::Fillet] Fillet125007020032039
  Base = -> Cut176013009033007019019008010045003002004008006021005004004004004002012033009016002012016
  Edges = 4 edges r=1: [Edge2,Edge10,Edge28,Edge36]
  Placement = pos=(75,-75,0) rot=(0,0,1;1.5708rad)
FEATURE [Part::Feature] Compound003001  label="Joint"
  Placement = pos=(36,0,0) rot=(0,0,1;0rad)
  shape: bbox 25.01 x 11 x 13.99 mm, 52 faces, 2 solids (baked)
FEATURE [Part::Compound] Compound003002  label="joint-STEEL"
  Links = -> [Fillet125007020032038,Fillet125007020032039]
FEATURE [Part::Feature] Compound003002001  label="Joint"
  Placement = pos=(70,0,9) rot=(0,0,1;0rad)
  shape: bbox 25.01 x 11 x 13.92 mm, 52 faces, 2 solids (baked)
FEATURE [Part::Cylinder] Cylinder1051  label="Cylinder"
  Angle = 360
  AttacherType = Attacher::AttachEngine3D
  FirstAngle = 0
  Height = 22
  Placement = pos=(118.375,0,47.903) rot=(0,1,0;1.309rad)
  Radius = 4
  SecondAngle = 0
FEATURE [Part::MultiFuse] Fusion088026007031024007008004100051055007010008005020006  label="rear-prop-shaft-STEEL"
  Refine = true
  Shapes = -> [Compound003002001,Compound003001,Cylinder1051]
FEATURE [Part::Fillet] Fillet125007020032040
  Base = -> Cylinder1015
  Edges = 1 edges r=1: [Edge3]
FEATURE [Part::Feature] Fusion088026007031024007008004100051055007010008005020019001  label="differential+pinion+rod"
  Placement = pos=(2,0,110) rot=(1,0,0;3.14159rad)
  shape: bbox 40.5 x 48 x 23 mm, 18 faces (baked)
FEATURE [Part::Part2DObjectPython] Line020  label="front-axle-midframe-path"  # Draft 2D object (typed FeaturePython)
  Closed = true
  End = (350,0,62)
  FilletRadius = 0
  MapMode = 5
  Placement = pos=(0,0,62) rot=(0,0,1;0rad)
  Points = (2) [(160,0,0),(350,0,0)]
  Start = (160,0,62)
FEATURE [Part::Box] Box375  label="Cube"
  AttacherType = Attacher::AttachEngine3D
  Height = 10.2
  Length = 10.2
  Placement = pos=(254.9,8,54.9) rot=(0,0,1;0rad)
  Width = 6
FEATURE [Part::Cylinder] Cylinder1064  label="Cylinder"
  Angle = 360
  AttacherType = Attacher::AttachEngine3D
  FirstAngle = 0
  Height = 6
  Placement = pos=(269.093,5,54.75) rot=(-0.377964,0.654654,0.654654;2.41886rad)
  Radius = 0.9
  SecondAngle = 0
FEATURE [Part::Cylinder] Cylinder1065  label="Cylinder"
  Angle = 360
  AttacherType = Attacher::AttachEngine3D
  FirstAngle = 0
  Height = 8
  Placement = pos=(260,8,60) rot=(-1,0,0;1.5708rad)
  Radius = 2.5
  SecondAngle = 0
FEATURE [Part::MultiFuse] Fusion088026007031024007008004100051055007010008005020019004  label="Fusion"
  Refine = true
  Shapes = -> [Box375,Cylinder1065]
FEATURE [Part::Cylinder] Cylinder1066  label="Cylinder"
  Angle = 360
  AttacherType = Attacher::AttachEngine3D
  FirstAngle = 0
  Height = 6
  Placement = pos=(260,5,70.5) rot=(-1,0,0;1.5708rad)
  Radius = 0.9
  SecondAngle = 0
FEATURE [Part::Cylinder] Cylinder1067  label="Cylinder"
  Angle = 360
  AttacherType = Attacher::AttachEngine3D
  FirstAngle = 0
  Height = 6
  Placement = pos=(250.907,5,54.75) rot=(0.377964,0.654654,0.654654;3.86433rad)
  Radius = 0.9
  SecondAngle = 0
FEATURE [Part::MultiFuse] Fusion088026007031024007008004100051055007010008005020019002  label="Fusion"
  Placement = pos=(0,3,0) rot=(0,0,1;0rad)
  Refine = true
  Shapes = -> [Cylinder1066,Cylinder1064,Cylinder1067]
FEATURE [Part::MultiFuse] Fusion088026007031024007008004100051055007010008005020019003  label="Fusion"
  Placement = pos=(0,0,2) rot=(0,0,1;0rad)
  Refine = true
  Shapes = -> [Fusion088026007031024007008004100051055007010008005020019004,Fusion088026007031024007008004100051055007010008005020019002]
FEATURE [Part::Feature] Cut176013009033007019019008010045003002004008006021005004004004004002012033009016002012007006  label="BEARING-5x9x3-MR95ZZ"
  Placement = pos=(146,75,9) rot=(0,0,-1;1.5708rad)
  shape: bbox 3 x 9 x 9 mm, 4 faces (baked)
FEATURE [Part::Feature] Cut176013009033007019019008010045003002004008006021005004004004004002012033009016002012007007  label="BEARING-5x9x3-MR95ZZ"
  Placement = pos=(141,75,9) rot=(0,0,-1;1.5708rad)
  shape: bbox 3 x 9 x 9 mm, 4 faces (baked)
FEATURE [Part::RegularPolygon] RegularPolygon  label="Regular polygon"
  AttacherType = Attacher::AttachEngine3D
  Circumradius = 3
  Placement = pos=(0,0,0) rot=(1,0,0;1.5708rad)
  Polygon = 6
FEATURE [Part::Extrusion] Extrude  label="HEX-BAR-32mm"
  Base = -> RegularPolygon
  Dir = (0,1,0)
  DirMode = 0
  FaceMakerClass = Part::FaceMakerBullseye
  LengthFwd = 32
  LengthRev = 0
  Solid = true
  Symmetric = false
FEATURE [Part::Feature] Extrude001  label="HEX-BAR-32mm"
  Placement = pos=(277,-16,82) rot=(0,0,1;0rad)
  shape: bbox 6 x 32 x 5.196 mm, 8 faces (baked)
FEATURE [Part::Feature] Extrude002  label="HEX-BAR-32mm"
  Placement = pos=(277,-16,39) rot=(0,0,1;0rad)
  shape: bbox 6 x 32 x 5.196 mm, 8 faces (baked)
FEATURE [Part::Feature] Extrude003  label="HEX-BAR-32mm"
  Placement = pos=(240,-16,39) rot=(0,0,1;0rad)
  shape: bbox 6 x 32 x 5.196 mm, 8 faces (baked)
FEATURE [Part::Feature] Extrude005  label="HEX-BAR-32mm"
  Placement = pos=(243,-16,82) rot=(0,0,1;0rad)
  shape: bbox 6 x 32 x 5.196 mm, 8 faces (baked)
FEATURE [Part::Box] Box722  label="Cube948"
  AttacherType = Attacher::AttachEngine3D
  Height = 3
  Length = 1.5
  Placement = pos=(80,6.5,9) rot=(0,0,1;0rad)
  Width = 12
FEATURE [Part::Chamfer] Chamfer039025078004018
  Base = -> Box722
  Edges = 2 edges: [Edge9 r1=0.7 r2=3.5,Edge11 r1=0.7 r2=3.5]
FEATURE [Part::Cylinder] Cylinder1492014  label="Cylinder1492016"
  Angle = 360
  AttacherType = Attacher::AttachEngine3D
  FirstAngle = 0
  Height = 4.5
  Placement = pos=(79,12.5,12) rot=(0,1,0;1.5708rad)
  Radius = 3
  SecondAngle = 0
FEATURE [Part::Feature] Fusion004002009002027014004009002002008002004029002015013017006002012002031033002013006007008014029072011018024002019049062029014012006016002033001057001  label="pendulum-lock-SERVO"
  Placement = pos=(109,18,6) rot=(0,0,1;3.14159rad)
  shape: bbox 27.75 x 32 x 12 mm, 30 faces (baked)
FEATURE [Part::Feature] Part__Mirroring012031002002001  label="Chamfer039025078004018 (Mirror #27)001"
  Placement = pos=(0,0,24) rot=(0,0,1;0rad)
  shape: bbox 1.5 x 12 x 3 mm, 8 faces (baked)
FEATURE [Part::MultiFuse] Fusion004002009002027014004009002002008002004029002015013017006002012002031033002013006007008014029072011018024002019049062029014012006016002033001057004  label="Fusion-0393"
  Refine = true
  Shapes = -> [Part__Mirroring012031002002001,Chamfer039025078004018]
FEATURE [Part::MultiFuse] Fusion004002009002027014004009002002008002004029002015013017006002012002031033002013006007008014029072011018024002019049062029014012006016002033001057005  label="Fusion-0394"
  Refine = true
  Shapes = -> [Fusion004002009002027014004009002002008002004029002015013017006002012002031033002013006007008014029072011018024002019049062029014012006016002033001057004,Cylinder1492014]
FEATURE [Part::MultiFuse] Fusion004002009002027014004009002002008002004029002015013017006002012002031033002013006007008014029072011018024002019049062029014012006016002033001057008  label="SERVO-EMAX_ES08MA_II"
  Placement = pos=(0,-12.5,0) rot=(0,0,1;0rad)
  Refine = true
  Shapes = -> [Fusion004002009002027014004009002002008002004029002015013017006002012002031033002013006007008014029072011018024002019049062029014012006016002033001057005,Fusion004002009002027014004009002002008002004029002015013017006002012002031033002013006007008014029072011018024002019049062029014012006016002033001057001]
FEATURE [Part::Box] Box081  label="Cube081"
  AttacherType = Attacher::AttachEngine3D
  Height = 20
  Length = 41
  Placement = pos=(50,-20,20) rot=(0,0,1;0rad)
  Width = 40
FEATURE [Part::Box] Box082  label="Cube082"
  AttacherType = Attacher::AttachEngine3D
  Height = 20
  Length = 3
  Placement = pos=(60,-27,20) rot=(0,0,1;0rad)
  Width = 54
FEATURE [Part::Cylinder] Cylinder282  label="Cylinder284"
  Angle = 360
  AttacherType = Attacher::AttachEngine3D
  FirstAngle = 0
  Height = 10
  Placement = pos=(59,11,30) rot=(0,-1,0;1.5708rad)
  Radius = 8
  SecondAngle = 0
FEATURE [Part::Cylinder] Cylinder337  label="Cylinder339"
  Angle = 360
  AttacherType = Attacher::AttachEngine3D
  FirstAngle = 0
  Height = 10
  Placement = pos=(57,-28.75,25) rot=(0,1,0;1.5708rad)
  Radius = 2
  SecondAngle = 0
FEATURE [Part::Cylinder] Cylinder338  label="Cylinder340"
  Angle = 360
  AttacherType = Attacher::AttachEngine3D
  FirstAngle = 0
  Height = 10
  Placement = pos=(57,-28.75,35) rot=(0,1,0;1.5708rad)
  Radius = 2
  SecondAngle = 0
FEATURE [Part::Cylinder] Cylinder339  label="Cylinder341"
  Angle = 360
  AttacherType = Attacher::AttachEngine3D
  FirstAngle = 0
  Height = 10
  Placement = pos=(57,20.25,35) rot=(0,1,0;1.5708rad)
  Radius = 2
  SecondAngle = 0
FEATURE [Part::Cylinder] Cylinder340  label="Cylinder342"
  Angle = 360
  AttacherType = Attacher::AttachEngine3D
  FirstAngle = 0
  Height = 10
  Placement = pos=(57,20.25,25) rot=(0,1,0;1.5708rad)
  Radius = 2
  SecondAngle = 0
FEATURE [Part::MultiFuse] Fusion004002009002027014004009002002008002004029002015013017006002012002031033002013006007008014029072011018014  label="Fusion-0108"
  Placement = pos=(0,4.25,0) rot=(0,0,1;0rad)
  Refine = true
  Shapes = -> [Cylinder337,Cylinder338,Cylinder340,Cylinder339]
FEATURE [Part::MultiFuse] Fusion004002009002027014004009002002008002004029002015013017006002012002031033002013006007008014029072011018015  label="Fusion-0109"
  Refine = true
  Shapes = -> [Cylinder282,Box081,Box082]
FEATURE [Part::Cut] Cut176013009033007019019008010045003002004008006010017027003005052  label="chassis-steering-SERVO"
  Base = -> Fusion004002009002027014004009002002008002004029002015013017006002012002031033002013006007008014029072011018015
  Placement = pos=(5,-5,0) rot=(0,0,1;0rad)
  Refine = true
  Tool = -> Fusion004002009002027014004009002002008002004029002015013017006002012002031033002013006007008014029072011018014
FEATURE [App::DocumentObjectGroup] Group013  label="Bearings"
  Group = -> [Cut004026018020025012002,Cut176013009033007019019008010045003002004008006021005002,Cut176013009033007019019008010045003002004008006021005003,Cut176013009033007019019008010045003002004008006021005004,Cut176013009033007019019008010045003002004008006021005005,Cut176013009033007019019008010045003002004008006021005004004004004002012033009016002,+1 more]
FEATURE [App::DocumentObjectGroup] Group015  label="Servos"
  Group = -> [Cut176013009033007019019008010045003002004008006010017027003005052,Fusion004002009002027014004009002002008002004029002015013017006002012002031033002013006007008014029072011018024002019049062029014012006016002033001057008]
FEATURE [Part::Cylinder] Cylinder1492015  label="Cylinder"
  Angle = 360
  AttacherType = Attacher::AttachEngine3D
  FirstAngle = 0
  Height = 3
  Placement = pos=(58,0,46) rot=(0,1,0;1.5708rad)
  Radius = 4
  SecondAngle = 0
FEATURE [Part::Cylinder] Cylinder1492016  label="Cylinder"
  Angle = 360
  AttacherType = Attacher::AttachEngine3D
  FirstAngle = 0
  Height = 5
  Placement = pos=(58,0,6) rot=(0,1,0;1.5708rad)
  Radius = 0.9
  SecondAngle = 0
FEATURE [Part::Cylinder] Cylinder1492017  label="Cylinder"
  Angle = 360
  AttacherType = Attacher::AttachEngine3D
  FirstAngle = 0
  Height = 5
  Placement = pos=(58,0,-6) rot=(0,1,0;1.5708rad)
  Radius = 0.9
  SecondAngle = 0
FEATURE [Part::MultiFuse] Fusion004002009002027014004009002002008002004029002015013017006002012002031033002013006007008014029072011018024002019049062029014012006016002033001057009  label="Fusion"
  Refine = true
  Shapes = -> [Cylinder1492017,Cylinder1492016]
FEATURE [Part::Feature] Fusion004002009002027014004009002002008002004029002015013017006002012002031033002013006007008014029072011018024002019049062029014012006016002033001057009001  label="Fusion"
  Placement = pos=(0,0,0) rot=(1,0,0;1.0472rad)
  shape: bbox 5 x 12.19 x 7.8 mm, 6 faces, 2 solids (baked)
FEATURE [Part::Feature] Fusion004002009002027014004009002002008002004029002015013017006002012002031033002013006007008014029072011018024002019049062029014012006016002033001057009002  label="Fusion"
  Placement = pos=(0,0,0) rot=(1,0,0;2.0944rad)
  shape: bbox 5 x 12.19 x 7.8 mm, 6 faces, 2 solids (baked)
FEATURE [Part::MultiFuse] Fusion004002009002027014004009002002008002004029002015013017006002012002031033002013006007008014029072011018024002019049062029014012006016002033001057009003  label="Fusion"
  Placement = pos=(0,0,46) rot=(0,0,1;0rad)
  Refine = true
  Shapes = -> [Fusion004002009002027014004009002002008002004029002015013017006002012002031033002013006007008014029072011018024002019049062029014012006016002033001057009002,Fusion004002009002027014004009002002008002004029002015013017006002012002031033002013006007008014029072011018024002019049062029014012006016002033001057009,+1 more]
FEATURE [Part::MultiFuse] Fusion004002009002027014004009002002008002004029002015013017006002012002031033002013006007008014029072011018024002019049062029014012006016002033001057009004  label="Fusion"
  Placement = pos=(-1,0,0) rot=(0,0,1;0rad)
  Refine = true
  Shapes = -> [Fusion004002009002027014004009002002008002004029002015013017006002012002031033002013006007008014029072011018024002019049062029014012006016002033001057009003,Cylinder1492015]
FEATURE [Part::Box] Box723  label="Cube"
  AttacherType = Attacher::AttachEngine3D
  Height = 30
  Length = 5
  Placement = pos=(87,-25,46) rot=(0,0,1;0rad)
  Width = 50
FEATURE [Part::Chamfer] Chamfer039025078004019
  Base = -> Box723
  Edges = 2 edges: [Edge9 r1=11 r2=12,Edge11 r1=11 r2=12]
FEATURE [Part::Cylinder] Cylinder1492018  label="Cylinder"
  Angle = 360
  AttacherType = Attacher::AttachEngine3D
  FirstAngle = 0
  Height = 5
  Placement = pos=(87,0,46) rot=(0,1,0;1.5708rad)
  Radius = 14
  SecondAngle = 0
FEATURE [Part::Box] Box724  label="Cube"
  AttacherType = Attacher::AttachEngine3D
  Height = 22
  Length = 5
  Placement = pos=(87,-32,60) rot=(0,0,1;0rad)
  Width = 64
FEATURE [Part::Chamfer] Chamfer039025078004020
  Base = -> Box724
  Edges = 2 edges: [Edge9 r1=21.99 r2=7,Edge11 r1=21.99 r2=7]
FEATURE [Part::Box] Box725  label="Cube"
  AttacherType = Attacher::AttachEngine3D
  Height = 22
  Length = 5
  Placement = pos=(87,-32,60) rot=(0,0,1;0rad)
  Width = 64
FEATURE [Part::Chamfer] Chamfer039025078004021
  Base = -> Box725
  Edges = 2 edges: [Edge9 r1=21.99 r2=7,Edge11 r1=21.99 r2=7]
  Placement = pos=(-29,0,0) rot=(0,0,1;0rad)
FEATURE [Part::Box] Box726  label="Cube"
  AttacherType = Attacher::AttachEngine3D
  Height = 32
  Length = 5
  Placement = pos=(58,-25,32) rot=(0,0,1;0rad)
  Width = 50
FEATURE [Part::Chamfer] Chamfer039025078004022
  Base = -> Box726
  Edges = 2 edges: [Edge9 r1=7 r2=22,Edge11 r1=7 r2=22]
FEATURE [Part::Chamfer] Chamfer039025078004023
  Base = -> Chamfer039025078004022
  Edges = 2 edges: [Edge8 r1=18 r2=10,Edge17 r1=18 r2=10]
FEATURE [Part::Cylinder] Cylinder1492019  label="Cylinder"
  Angle = 360
  AttacherType = Attacher::AttachEngine3D
  FirstAngle = 0
  Height = 4
  Placement = pos=(87,0,46) rot=(0,1,0;1.5708rad)
  Radius = 11.5
  SecondAngle = 0
FEATURE [Part::Cylinder] Cylinder1492020  label="Cylinder"
  Angle = 360
  AttacherType = Attacher::AttachEngine3D
  FirstAngle = 0
  Height = 5
  Placement = pos=(87,0,46) rot=(0,1,0;1.5708rad)
  Radius = 10.5
  SecondAngle = 0
FEATURE [Part::Feature] Cut176013009033007019019008010045003002004008006021005002002  label="BEARING-17x23x4-6703"
  Placement = pos=(156,-75,0) rot=(0,0,1;1.5708rad)
  shape: bbox 4 x 23 x 23 mm, 4 faces (baked)
FEATURE [Part::Feature] Cut176013009033007019019008010045003002004008006021005004004004004002012033009016002012007009  label="BEARING-17x23x4-6703"
  Placement = pos=(127,-75,0) rot=(0,0,1;1.5708rad)
  shape: bbox 4 x 23 x 23 mm, 4 faces (baked)
FEATURE [Part::Cylinder] Cylinder1492021  label="Cylinder"
  Angle = 360
  AttacherType = Attacher::AttachEngine3D
  FirstAngle = 0
  Height = 5
  Placement = pos=(58,0,46) rot=(0,1,0;1.5708rad)
  Radius = 10.5
  SecondAngle = 0
FEATURE [Part::Cylinder] Cylinder1492022  label="Cylinder"
  Angle = 360
  AttacherType = Attacher::AttachEngine3D
  FirstAngle = 0
  Height = 4
  Placement = pos=(59,0,46) rot=(0,1,0;1.5708rad)
  Radius = 11.5
  SecondAngle = 0
FEATURE [Part::MultiFuse] Fusion004002009002027014004009002002008002004029002015013017006002012002031033002013006007008014029072011018024002019049062029014012006016002033001057009007  label="Fusion"
  Refine = true
  Shapes = -> [Cylinder1492019,Cylinder1492020]
FEATURE [Part::MultiFuse] Fusion004002009002027014004009002002008002004029002015013017006002012002031033002013006007008014029072011018024002019049062029014012006016002033001057009008  label="Fusion"
  Refine = true
  Shapes = -> [Cylinder1492021,Cylinder1492022]
FEATURE [Part::Box] Box727  label="Cube"
  AttacherType = Attacher::AttachEngine3D
  Height = 34
  Length = 5
  Placement = pos=(87,-20,62) rot=(0,0,1;0rad)
  Width = 40
FEATURE [Part::Box] Box728  label="Cube"
  AttacherType = Attacher::AttachEngine3D
  Height = 34
  Length = 5
  Placement = pos=(58,-20,62) rot=(0,0,1;0rad)
  Width = 40
FEATURE [Part::Box] Box731  label="Cube"
  AttacherType = Attacher::AttachEngine3D
  Height = 29
  Length = 5
  Placement = pos=(87,-27,68) rot=(0,0,1;0rad)
  Width = 54
FEATURE [Part::Box] Box732  label="Cube"
  AttacherType = Attacher::AttachEngine3D
  Height = 30
  Length = 5
  Placement = pos=(58,-27,67) rot=(0,0,1;0rad)
  Width = 54
FEATURE [Part::RegularPolygon] RegularPolygon001  label="Regular polygon"
  AttacherType = Attacher::AttachEngine3D
  Circumradius = 3
  Placement = pos=(0,0,0) rot=(1,0,0;1.5708rad)
  Polygon = 6
FEATURE [Part::Extrusion] Extrude007  label="HEX-BAR-25mm"
  Base = -> RegularPolygon001
  Dir = (0,1,0)
  DirMode = 0
  FaceMakerClass = Part::FaceMakerBullseye
  LengthFwd = 25
  LengthRev = 0
  Solid = true
  Symmetric = false
FEATURE [App::DocumentObjectGroup] Group017  label="Hex bars"
  Group = -> [Extrude,Extrude007]
FEATURE [Part::Part2DObjectPython] Line021  label="rear-wheels-tilting-path"  # Draft 2D object (typed FeaturePython)
  Closed = true
  End = (140,7.87924e-09,46)
  FilletRadius = 0
  MapMode = 5
  Placement = pos=(10,7.87924e-09,46) rot=(1,0,0;0.139626rad)
  Points = (2) [(0,0,0),(130,0,0)]
  Start = (10,7.87924e-09,46)
FEATURE [Part::Feature] Part__Mirroring007002003002018002002002006  label="axle-shaft-right"
  shape: bbox 6 x 53.5 x 11 mm, 15 faces (baked)
FEATURE [Part::Feature] Part__Mirroring007002003002018002002002005001  label="wheel-axle-right"
  shape: bbox 11 x 25 x 11 mm, 19 faces, 2 solids (baked)
FEATURE [App::DocumentObjectGroup] Group007  label="Inner Parts"
  Group = -> [Fusion041001,Fusion088026007031024007008004081022014,Cut176013009033007019019008010045003002004008006021005010,Part__Mirroring007002003002018002002002006,Part__Mirroring007002003002018002002002005001]
FEATURE [Part::Box] Box733  label="Cube"
  AttacherType = Attacher::AttachEngine3D
  Height = 22
  Length = 25
  Placement = pos=(62,-32,60) rot=(0,0,1;0rad)
  Width = 7
FEATURE [Part::Chamfer] Chamfer039025078004026
  Base = -> Box733
  Edges = 1 edges: [Edge9 r1=21.99 r2=6.99]
FEATURE [Part::Chamfer] Chamfer039025078004027
  Base = -> Box727
  Edges = 2 edges r=8: [Edge9,Edge11]
  Placement = pos=(0,0,7.5) rot=(0,0,1;0rad)
FEATURE [Part::MultiFuse] Fusion004002009002027014004009002002008002004029002015013017006002012002031033002013006007008014029072011018024002019049062029014012006016002033001057009016  label="Fusion"
  Refine = true
  Shapes = -> [Chamfer039025078004019,Chamfer039025078004020]
FEATURE [Part::MultiFuse] Fusion004002009002027014004009002002008002004029002015013017006002012002031033002013006007008014029072011018024002019049062029014012006016002033001057009017  label="Fusion"
  Refine = true
  Shapes = -> [Fusion004002009002027014004009002002008002004029002015013017006002012002031033002013006007008014029072011018024002019049062029014012006016002033001057009016,Cylinder1492018]
FEATURE [Part::MultiFuse] Fusion004002009002027014004009002002008002004029002015013017006002012002031033002013006007008014029072011018024002019049062029014012006016002033001057009018  label="Fusion"
  Refine = true
  Shapes = -> [Fusion004002009002027014004009002002008002004029002015013017006002012002031033002013006007008014029072011018024002019049062029014012006016002033001057009017,Box731]
FEATURE [Part::Cut] Cut176013009033007019019008010045003002004008006021005004004004004002012033009016002012007017  label="Cut"
  Base = -> Fusion004002009002027014004009002002008002004029002015013017006002012002031033002013006007008014029072011018024002019049062029014012006016002033001057009018
  Refine = true
  Tool = -> Fusion004002009002027014004009002002008002004029002015013017006002012002031033002013006007008014029072011018024002019049062029014012006016002033001057009007
FEATURE [Part::Cut] Cut176013009033007019019008010045003002004008006021005004004004004002012033009016002012007018  label="Cut"
  Base = -> Cut176013009033007019019008010045003002004008006021005004004004004002012033009016002012007017
  Refine = true
  Tool = -> Chamfer039025078004027
FEATURE [Part::MultiFuse] Fusion004002009002027014004009002002008002004029002015013017006002012002031033002013006007008014029072011018024002019049062029014012006016002033001057009019  label="Fusion"
  Refine = true
  Shapes = -> [Box732,Chamfer039025078004023,Chamfer039025078004021]
FEATURE [Part::Chamfer] Chamfer039025078004028
  Base = -> Box728
  Edges = 2 edges r=8: [Edge9,Edge11]
  Placement = pos=(0,0,7.5) rot=(0,0,1;0rad)
FEATURE [Part::Cut] Cut176013009033007019019008010045003002004008006021005004004004004002012033009016002012007019  label="Cut"
  Base = -> Fusion004002009002027014004009002002008002004029002015013017006002012002031033002013006007008014029072011018024002019049062029014012006016002033001057009019
  Refine = true
  Tool = -> Chamfer039025078004028
FEATURE [Part::Feature] Cut176013009033007019019008010045003002004008006021005004004004004002012018001  label="rear-axle-steering-knukle-upper-plate-right"
  Placement = pos=(1.4e-14,-6.40196,0.447669) rot=(-1,0,0;0.139626rad)
  shape: bbox 21.09 x 38.85 x 11.71 mm, 67 faces (baked)
FEATURE [Part::Box] Box734  label="Cube"
  AttacherType = Attacher::AttachEngine3D
  Height = 33
  Length = 25
  Placement = pos=(62,-20,64.5) rot=(0,0,1;0rad)
  Width = 40
FEATURE [Part::Box] Box736  label="Cube"
  AttacherType = Attacher::AttachEngine3D
  Height = 22
  Length = 25
  Placement = pos=(62,-35,60) rot=(0,0,1;0rad)
  Width = 7
FEATURE [Part::Chamfer] Chamfer039025078004029
  Base = -> Box736
  Edges = 1 edges: [Edge11 r1=21.99 r2=6.99]
  Placement = pos=(0,60,0) rot=(0,0,1;0rad)
FEATURE [Part::Box] Box737  label="Cube"
  AttacherType = Attacher::AttachEngine3D
  Height = 25
  Length = 25
  Placement = pos=(62,-25,57) rot=(0,0,1;0rad)
  Width = 50
FEATURE [Part::Cylinder] Cylinder1492030  label="Cylinder"
  Angle = 360
  AttacherType = Attacher::AttachEngine3D
  FirstAngle = 0
  Height = 59
  Placement = pos=(75,0,46) rot=(-1,0,0;1.43117rad)
  Radius = 9
  SecondAngle = 0
FEATURE [Part::Box] Box738  label="Cube"
  AttacherType = Attacher::AttachEngine3D
  Height = 31.5
  Length = 25
  Placement = pos=(63,0,30) rot=(1,0,0;0rad)
  Width = 18
FEATURE [Part::Cut] Cut176013009033007019019008010045003002004008006021005004004004004002012033009016002012007021  label="Cut"
  Base = -> Cut176013009033007019019008010045003002004008006021005004004004004002012033009016002012007019
  Refine = true
  Tool = -> Fusion004002009002027014004009002002008002004029002015013017006002012002031033002013006007008014029072011018024002019049062029014012006016002033001057009008
FEATURE [Part::Feature] Cut176013009033007019019008010045003002004008006021005004004004004002012033009016002012007022002  label="rear-axle-base-carved"
  Placement = pos=(1.4e-14,-7.98577,0.701105) rot=(-1,0,0;0.174533rad)
  shape: bbox 39 x 97.67 x 34.4 mm, 141 faces (baked)
FEATURE [Part::Fillet] Fillet125007020032041
  Base = -> Box738
  Edges = 1 edges r=7: [Edge12]
  Placement = pos=(-1,0,0) rot=(0,0,1;0rad)
FEATURE [Part::MultiFuse] Fusion004002009002027014004009002002008002004029002015013017006002012002031033002013006007008014029072011018024002019049062029014012006016002033001057009021  label="Fusion"
  Refine = true
  Shapes = -> [Cylinder1492030,Fillet125007020032041]
FEATURE [Part::Box] Box742  label="Cube"
  AttacherType = Attacher::AttachEngine3D
  Height = 3
  Length = 6
  Placement = pos=(72,-50,62) rot=(0,0,1;0rad)
  Width = 18
FEATURE [Part::Cylinder] Cylinder1492060
  Angle = 360
  AttacherType = Attacher::AttachEngine3D
  FirstAngle = 0
  Height = 3
  Placement = pos=(75,-35,62) rot=(0,0,1;0rad)
  Radius = 1.25
  SecondAngle = 0
FEATURE [Part::Box] Box743  label="Cube"
  AttacherType = Attacher::AttachEngine3D
  Height = 3
  Length = 10
  Placement = pos=(70,-62.5,62) rot=(0,0,1;0rad)
  Width = 15
FEATURE [Part::MultiFuse] Fusion004002009002027014004009002002008002004029002015013017006002012002031033002013006007008014029072011018024002019049062029014012006016002033001057009041  label="Fusion"
  Refine = true
  Shapes = -> [Box743,Box742]
FEATURE [Part::Chamfer] Chamfer039025078004032
  Base = -> Fusion004002009002027014004009002002008002004029002015013017006002012002031033002013006007008014029072011018024002019049062029014012006016002033001057009041
  Edges = 2 edges r=1.9: [Edge9,Edge16]
FEATURE [Part::Cylinder] Cylinder1492065
  Angle = 360
  AttacherType = Attacher::AttachEngine3D
  FirstAngle = 0
  Height = 3
  Placement = pos=(69.5,-49,53.6) rot=(0,0,1;0rad)
  Radius = 2.2
  SecondAngle = 0
FEATURE [Part::Cylinder] Cylinder1492066
  Angle = 360
  AttacherType = Attacher::AttachEngine3D
  FirstAngle = 0
  Height = 3
  Placement = pos=(80.5,-49,53.6) rot=(0,0,1;0rad)
  Radius = 2.2
  SecondAngle = 0
FEATURE [Part::Cylinder] Cylinder1492068
  Angle = 360
  AttacherType = Attacher::AttachEngine3D
  FirstAngle = 0
  Height = 8.4
  Placement = pos=(69.5,-49,60) rot=(0,0,1;0rad)
  Radius = 1.1
  SecondAngle = 0
FEATURE [Part::Cylinder] Cylinder1492069
  Angle = 360
  AttacherType = Attacher::AttachEngine3D
  FirstAngle = 0
  Height = 8.4
  Placement = pos=(80.5,-49,60) rot=(0,0,1;0rad)
  Radius = 1.1
  SecondAngle = 0
FEATURE [Part::Cylinder] Cylinder1492070
  Angle = 360
  AttacherType = Attacher::AttachEngine3D
  FirstAngle = 0
  Height = 8.4
  Placement = pos=(75,-60,60) rot=(0,0,1;0rad)
  Radius = 1.1
  SecondAngle = 0
FEATURE [Part::MultiFuse] Fusion004002009002027014004009002002008002004029002015013017006002012002031033002013006007008014029072011018024002019049062029014012006016002033001057009044  label="Fusion"
  Placement = pos=(0,0,8.4) rot=(0,0,1;0rad)
  Refine = true
  Shapes = -> [Cylinder1492065,Cylinder1492066]
FEATURE [Part::MultiFuse] Fusion004002009002027014004009002002008002004029002015013017006002012002031033002013006007008014029072011018024002019049062029014012006016002033001057009045  label="Fusion"
  Refine = true
  Shapes = -> [Chamfer039025078004032,Fusion004002009002027014004009002002008002004029002015013017006002012002031033002013006007008014029072011018024002019049062029014012006016002033001057009044]
FEATURE [Part::Fillet] Fillet125007020032044
  Base = -> Fusion004002009002027014004009002002008002004029002015013017006002012002031033002013006007008014029072011018024002019049062029014012006016002033001057009045
  Edges = 4 edges r=3: [Edge4,Edge16,Edge18,Edge27]
FEATURE [Part::Fillet] Fillet125007020032045
  Base = -> Fillet125007020032044
  Edges = 4 edges r=2.99: [Edge22,Edge40,Edge41,Edge42]
FEATURE [Part::MultiFuse] Fusion004002009002027014004009002002008002004029002015013017006002012002031033002013006007008014029072011018024002019049062029014012006016002033001057009046  label="Fusion"
  Refine = true
  Shapes = -> [Cylinder1492060,Cylinder1492068,Cylinder1492069,Cylinder1492070]
FEATURE [Part::Cut] Cut176013009033007019019008010045003002004008006021005004004004004002012033009016002012007022011  label="rear-axle-steering-knukle-lever-ALU3mm"
  Base = -> Fillet125007020032045
  Refine = true
  Tool = -> Fusion004002009002027014004009002002008002004029002015013017006002012002031033002013006007008014029072011018024002019049062029014012006016002033001057009046
FEATURE [Part::Cylinder] Cylinder1492075  label="Cylinder"
  Angle = 360
  AttacherType = Attacher::AttachEngine3D
  FirstAngle = 0
  Height = 34
  Placement = pos=(58,21.5,64) rot=(0,1,0;1.5708rad)
  Radius = 1.5
  SecondAngle = 0
FEATURE [Part::Cylinder] Cylinder1492076  label="Cylinder"
  Angle = 360
  AttacherType = Attacher::AttachEngine3D
  FirstAngle = 0
  Height = 34
  Placement = pos=(58,25,77) rot=(0,1,0;1.5708rad)
  Radius = 1.5
  SecondAngle = 0
FEATURE [Part::Cylinder] Cylinder1492077  label="Cylinder"
  Angle = 360
  AttacherType = Attacher::AttachEngine3D
  FirstAngle = 0
  Height = 34
  Placement = pos=(58,-25,77) rot=(0,1,0;1.5708rad)
  Radius = 1.5
  SecondAngle = 0
FEATURE [Part::Cylinder] Cylinder1492078  label="Cylinder"
  Angle = 360
  AttacherType = Attacher::AttachEngine3D
  FirstAngle = 0
  Height = 34
  Placement = pos=(58,-21.5,64) rot=(0,1,0;1.5708rad)
  Radius = 1.5
  SecondAngle = 0
FEATURE [Part::MultiFuse] Fusion004002009002027014004009002002008002004029002015013017006002012002031033002013006007008014029072011018024002019049062029014012006016002033001057009048  label="Fusion"
  Refine = true
  Shapes = -> [Cylinder1492075,Cylinder1492076,Cylinder1492077,Cylinder1492078]
FEATURE [Part::Cylinder] Cylinder1492079  label="Cylinder"
  Angle = 360
  AttacherType = Attacher::AttachEngine3D
  FirstAngle = 0
  Height = 35
  Placement = pos=(57,21.5,64) rot=(0,1,0;1.5708rad)
  Radius = 1.5
  SecondAngle = 0
FEATURE [Part::Cylinder] Cylinder1492080  label="Cylinder"
  Angle = 360
  AttacherType = Attacher::AttachEngine3D
  FirstAngle = 0
  Height = 35
  Placement = pos=(57,25,77) rot=(0,1,0;1.5708rad)
  Radius = 1.5
  SecondAngle = 0
FEATURE [Part::Cylinder] Cylinder1492081  label="Cylinder"
  Angle = 360
  AttacherType = Attacher::AttachEngine3D
  FirstAngle = 0
  Height = 35
  Placement = pos=(57,-25,77) rot=(0,1,0;1.5708rad)
  Radius = 1.5
  SecondAngle = 0
FEATURE [Part::Cylinder] Cylinder1492082  label="Cylinder"
  Angle = 360
  AttacherType = Attacher::AttachEngine3D
  FirstAngle = 0
  Height = 35
  Placement = pos=(57,-21.5,64) rot=(0,1,0;1.5708rad)
  Radius = 1.5
  SecondAngle = 0
FEATURE [Part::MultiFuse] Fusion004002009002027014004009002002008002004029002015013017006002012002031033002013006007008014029072011018024002019049062029014012006016002033001057009049  label="Fusion"
  Refine = true
  Shapes = -> [Cylinder1492079,Cylinder1492080,Cylinder1492081,Cylinder1492082]
FEATURE [Part::Cut] Cut176013009033007019019008010045003002004008006021005004004004004002012033009016002012007022014  label="Cut"
  Base = -> Cut176013009033007019019008010045003002004008006021005004004004004002012033009016002012007018
  Refine = true
  Tool = -> Fusion004002009002027014004009002002008002004029002015013017006002012002031033002013006007008014029072011018024002019049062029014012006016002033001057009048
FEATURE [Part::Cut] Cut176013009033007019019008010045003002004008006021005004004004004002012033009016002012007022015  label="Cut"
  Base = -> Cut176013009033007019019008010045003002004008006021005004004004004002012033009016002012007021
  Refine = true
  Tool = -> Fusion004002009002027014004009002002008002004029002015013017006002012002031033002013006007008014029072011018024002019049062029014012006016002033001057009049
FEATURE [Part::Feature] Fusion088026007031024007008004100051055007010008005003006007005002001  label="front-wheel-right"
  Placement = pos=(260,-87,62) rot=(0,0,1;0rad)
  shape: bbox 129.9 x 36 x 129.9 mm, 584 faces (baked)
FEATURE [Part::Feature] Fusion004002009002027014004009002002008002004029002015013017006002012002031033002013006007008014029072011018024002019049062029014012006016002033001057009050  label="front-wheel-left"
  Placement = pos=(260,51,62) rot=(0,0,1;0rad)
  shape: bbox 129.9 x 36 x 129.9 mm, 584 faces (baked)
FEATURE [Mesh::Feature] Diff_Gear_23T_pitch213  label="Diff-Gear-23T-pitch213"
  Placement = pos=(0,0,0) rot=(1,0,0;1.5708rad)
FEATURE [Mesh::Feature] Diff_Gear_31T_pitch213  label="Diff-Gear-31T-pitch213"
  Placement = pos=(0,0,0) rot=(1,0,0;1.5708rad)
FEATURE [App::DocumentObjectGroup] Group018  label="Gears"
  Group = -> [Diff_Gear_23T_pitch213,Diff_Gear_31T_pitch213]
FEATURE [Part::Feature] Diff_Gear_31T_pitch213001_solid  label="Diff_Gear_31T_pitch213"
  Placement = pos=(260,16,62) rot=(0,0,1;0rad)
  shape: bbox 38.98 x 8 x 39.03 mm, 1732 faces (baked)
FEATURE [Part::Cut] Cut176013009033007019019008010045003002004008006021005004004004004002012033009016002012007022017  label="diff_front_gear_left"
  Base = -> Diff_Gear_31T_pitch213001_solid
  Refine = true
  Tool = -> Fusion088026007031024007008004100051055007010008005020019003
FEATURE [Part::Feature] Diff_Gear_23T_pitch213001_solid  label="Diff_Gear_23T_pitch213"
  Placement = pos=(228.5,16,55) rot=(0,0,1;0rad)
  shape: bbox 29.48 x 8 x 29.55 mm, 1284 faces (baked)
FEATURE [Part::Box] Box376  label="Cube"
  AttacherType = Attacher::AttachEngine3D
  Height = 10.5
  Length = 10.5
  Placement = pos=(228.75,8,47.75) rot=(0,0,1;0rad)
  Width = 8
FEATURE [Part::Cylinder] Cylinder1068  label="Cylinder"
  Angle = 360
  AttacherType = Attacher::AttachEngine3D
  FirstAngle = 0
  Height = 3.75
  Placement = pos=(234,11.75,53) rot=(1,0,0;1.5708rad)
  Radius = 6.05
  SecondAngle = 0
FEATURE [Part::MultiFuse] Fusion088026007031024007008004100051055007010008005020019005  label="Fusion"
  Placement = pos=(-5.5,0,2) rot=(0,0,1;0rad)
  Refine = true
  Shapes = -> [Box376,Cylinder1068]
FEATURE [Part::Cut] Cut176013009033007019019008010045003002004008006021005004004004004002012033009016002012007022016  label="diff_rear_gear_left"
  Base = -> Diff_Gear_23T_pitch213001_solid
  Placement = pos=(0.5,0,0) rot=(0,0,1;0rad)
  Refine = true
  Tool = -> Fusion088026007031024007008004100051055007010008005020019005
FEATURE [Part::Feature] Cut176013009033007019019008010045003002004008006021005004078021006001  label="rim-front-external-right"
  Placement = pos=(75,-87,62) rot=(0,0,1;0rad)
  shape: bbox 79.47 x 17 x 79.47 mm, 83 faces (baked)
FEATURE [Part::Feature] Cut176013009033007019019008010045003002004008006021005004078021008001  label="rim-front-internal-right"
  Placement = pos=(75,-87,62) rot=(0,0,1;0rad)
  shape: bbox 79.47 x 17 x 79.47 mm, 46 faces (baked)
FEATURE [Part::Feature] Cut176013009033007019019008010045003002004008006021005004078021012001  label="rim-rear-internal-right"
  Placement = pos=(75,-84,46) rot=(0,0,1;0rad)
  shape: bbox 63.76 x 12.5 x 63.76 mm, 44 faces (baked)
FEATURE [Part::Feature] Cut176013009033007019019008010045003002004008006021005004078021017006001  label="rim-rear-external-right"
  Placement = pos=(75,-84,46) rot=(0,0,1;0rad)
  shape: bbox 63.76 x 15.5 x 63.76 mm, 94 faces (baked)
FEATURE [Part::Feature] Part__Mirroring007002003002018002002002005004005  label="rim-front-external-left"
  Placement = pos=(75,87,62) rot=(0,0,1;0rad)
  shape: bbox 79.47 x 17 x 79.47 mm, 83 faces (baked)
FEATURE [Part::Feature] Part__Mirroring007002003002018002002002005004002001  label="rim-front-internal-left"
  Placement = pos=(75,87,62) rot=(0,0,1;0rad)
  shape: bbox 79.47 x 17 x 79.47 mm, 46 faces (baked)
FEATURE [Part::Feature] Part__Mirroring007002003002018002002002005004003001  label="rim-rear-internal-left"
  Placement = pos=(75,84,46) rot=(0,0,1;0rad)
  shape: bbox 63.76 x 12.5 x 63.76 mm, 44 faces (baked)
FEATURE [Part::Feature] Part__Mirroring007002003002018002002002005004004001  label="rim-rear-external-left"
  Placement = pos=(75,84,46) rot=(0,0,1;0rad)
  shape: bbox 63.76 x 15.5 x 63.76 mm, 94 faces (baked)
FEATURE [App::DocumentObjectGroup] Group  label="Wheels"
  Group = -> [Fusion017003004005003,Fusion088026007031024007008004100051009001010,Fusion088026007031024007008004100051055007010008005003006007005002001,Fusion004002009002027014004009002002008002004029002015013017006002012002031033002013006007008014029072011018024002019049062029014012006016002033001057009050,Cut176013009033007019019008010045003002004008006021005004078021006001,+7 more]
FEATURE [Part::Box] Box006  label="frame-left_ALU"
  AttacherType = Attacher::AttachEngine3D
  Height = 15
  Length = 300
  Placement = pos=(11,27,82) rot=(0,0,1;0rad)
  Width = 5
FEATURE [Part::Box] Box007  label="frame-right_ALU"
  AttacherType = Attacher::AttachEngine3D
  Height = 15
  Length = 300
  Placement = pos=(11,-32,82) rot=(0,0,1;0rad)
  Width = 5
FEATURE [Part::Cylinder] Cylinder1492083  label="Cylinder"
  Angle = 360
  AttacherType = Attacher::AttachEngine3D
  FirstAngle = 0
  Height = 4
  Placement = pos=(0,0,-13) rot=(1,0,0;1.5708rad)
  Radius = 2
  SecondAngle = 0
FEATURE [Part::Cylinder] Cylinder1492085  label="Cylinder"
  Angle = 360
  AttacherType = Attacher::AttachEngine3D
  FirstAngle = 0
  Height = 4
  Placement = pos=(0,0,13) rot=(1,0,0;1.5708rad)
  Radius = 2
  SecondAngle = 0
FEATURE [Part::Cylinder] Cylinder1492086  label="Cylinder"
  Angle = 360
  AttacherType = Attacher::AttachEngine3D
  FirstAngle = 0
  Height = 4
  Placement = pos=(13,0,0) rot=(1,0,0;1.5708rad)
  Radius = 2
  SecondAngle = 0
FEATURE [Part::Cylinder] Cylinder1492087  label="Cylinder"
  Angle = 360
  AttacherType = Attacher::AttachEngine3D
  FirstAngle = 0
  Height = 4
  Placement = pos=(-13,0,0) rot=(1,0,0;1.5708rad)
  Radius = 2
  SecondAngle = 0
FEATURE [Part::MultiFuse] Fusion004002009002027014004009002002008002004029002015013017006002012002031033002013006007008014029072011018024002019049062029014012006016002033001057009052  label="Fusion"
  Placement = pos=(260,66,62) rot=(0,0,1;0rad)
  Refine = true
  Shapes = -> [Cylinder1492083,Cylinder1492085,Cylinder1492086,Cylinder1492087]
FEATURE [Part::MultiFuse] Fusion004002009002027014004009002002008002004029002015013017006002012002031033002013006007008014029072011018024002019049062029014012006016002033001057009053  label="Fusion"
  Refine = true
  Shapes = -> [Chamfer228039,Fusion004002009002027014004009002002008002004029002015013017006002012002031033002013006007008014029072011018024002019049062029014012006016002033001057009052]
FEATURE [Part::Cut] Cut176013009033007019019008010045003002004008006021005004004004004002012033009016002012007022019  label="front-hub-internal-left"
  Base = -> Fusion004002009002027014004009002002008002004029002015013017006002012002031033002013006007008014029072011018024002019049062029014012006016002033001057009053
  Refine = true
  Tool = -> Fusion088026007031024007008004100051055007010008005003
FEATURE [Part::Box] Box745  label="Cube261"
  AttacherType = Attacher::AttachEngine3D
  Height = 2.1
  Length = 10
  Placement = pos=(70,32.5,51.5) rot=(0,0,1;0rad)
  Width = 24.5
FEATURE [Part::Box] Box746  label="Cube261"
  AttacherType = Attacher::AttachEngine3D
  Height = 2.1
  Length = 14
  Placement = pos=(68,32.5,51.5) rot=(0,0,1;0rad)
  Width = 15.5
FEATURE [Part::Box] Box747  label="Cube261"
  AttacherType = Attacher::AttachEngine3D
  Height = 2.1
  Length = 10
  Placement = pos=(70,32.5,51.5) rot=(0,0,1;0rad)
  Width = 24.5
FEATURE [Part::Box] Box748  label="Cube261"
  AttacherType = Attacher::AttachEngine3D
  Height = 2.1
  Length = 14
  Placement = pos=(68,32.5,51.5) rot=(0,0,1;0rad)
  Width = 15.5
FEATURE [Part::Cylinder] Cylinder1492088
  Angle = 360
  AttacherType = Attacher::AttachEngine3D
  FirstAngle = 0
  Height = 5
  Placement = pos=(75,53.5,51.5) rot=(0,0,1;0rad)
  Radius = 2
  SecondAngle = 0
FEATURE [Part::Cylinder] Cylinder1492089
  Angle = 360
  AttacherType = Attacher::AttachEngine3D
  FirstAngle = 0
  Height = 8.1
  Placement = pos=(75,53.5,50.5) rot=(0,0,1;0rad)
  Radius = 1.25
  SecondAngle = 0
FEATURE [Part::Cylinder] Cylinder1492090  label="Cylinder"
  Angle = 360
  AttacherType = Attacher::AttachEngine3D
  FirstAngle = 0
  Height = 20
  Placement = pos=(79.25,35,36) rot=(0,0,1;0rad)
  Radius = 1
  SecondAngle = 0
FEATURE [Part::Cylinder] Cylinder1492091  label="Cylinder"
  Angle = 360
  AttacherType = Attacher::AttachEngine3D
  FirstAngle = 0
  Height = 20
  Placement = pos=(70.75,35,36) rot=(0,0,1;0rad)
  Radius = 1
  SecondAngle = 0
FEATURE [Part::Cylinder] Cylinder1492092  label="Cylinder"
  Angle = 360
  AttacherType = Attacher::AttachEngine3D
  FirstAngle = 0
  Height = 20
  Placement = pos=(70.75,40,36) rot=(0,0,1;0rad)
  Radius = 1
  SecondAngle = 0
FEATURE [Part::Cylinder] Cylinder1492093  label="Cylinder"
  Angle = 360
  AttacherType = Attacher::AttachEngine3D
  FirstAngle = 0
  Height = 20
  Placement = pos=(79.25,40,36) rot=(0,0,1;0rad)
  Radius = 1
  SecondAngle = 0
FEATURE [Part::Cylinder] Cylinder1492098
  Angle = 360
  AttacherType = Attacher::AttachEngine3D
  FirstAngle = 0
  Height = 5
  Placement = pos=(75,53.5,35.5) rot=(0,0,1;0rad)
  Radius = 2
  SecondAngle = 0
FEATURE [Part::Cylinder] Cylinder1492099
  Angle = 360
  AttacherType = Attacher::AttachEngine3D
  FirstAngle = 0
  Height = 8.1
  Placement = pos=(75,53.5,34.5) rot=(0,0,1;0rad)
  Radius = 1.25
  SecondAngle = 0
FEATURE [Part::Cylinder] Cylinder1492100  label="Cylinder"
  Angle = 360
  AttacherType = Attacher::AttachEngine3D
  FirstAngle = 0
  Height = 20
  Placement = pos=(79.25,35,36) rot=(0,0,1;0rad)
  Radius = 1
  SecondAngle = 0
FEATURE [Part::Cylinder] Cylinder1492101  label="Cylinder"
  Angle = 360
  AttacherType = Attacher::AttachEngine3D
  FirstAngle = 0
  Height = 20
  Placement = pos=(70.75,35,36) rot=(0,0,1;0rad)
  Radius = 1
  SecondAngle = 0
FEATURE [Part::Cylinder] Cylinder1492102  label="Cylinder"
  Angle = 360
  AttacherType = Attacher::AttachEngine3D
  FirstAngle = 0
  Height = 20
  Placement = pos=(70.75,40,36) rot=(0,0,1;0rad)
  Radius = 1
  SecondAngle = 0
FEATURE [Part::Cylinder] Cylinder1492103  label="Cylinder"
  Angle = 360
  AttacherType = Attacher::AttachEngine3D
  FirstAngle = 0
  Height = 20
  Placement = pos=(79.25,40,36) rot=(0,0,1;0rad)
  Radius = 1
  SecondAngle = 0
FEATURE [Part::MultiFuse] Fusion004002009002027014004009002002008002004029002015013017006002012002031033002013006007008014029072011018024002019049062029014012006016002033001057009054  label="Fusion"
  Refine = true
  Shapes = -> [Box746,Box745]
FEATURE [Part::Chamfer] Chamfer039025078004033
  Base = -> Fusion004002009002027014004009002002008002004029002015013017006002012002031033002013006007008014029072011018024002019049062029014012006016002033001057009054
  Edges = 2 edges: [Edge7 r1=1.99 r2=3.5,Edge13 r1=1.99 r2=3.5]
FEATURE [Part::Fillet] Fillet125007020032046
  Base = -> Chamfer039025078004033
  Edges = 2 edges r=4.99: [Edge29,Edge30]
FEATURE [Part::MultiFuse] Fusion004002009002027014004009002002008002004029002015013017006002012002031033002013006007008014029072011018024002019049062029014012006016002033001057009057  label="Fusion"
  Refine = true
  Shapes = -> [Box748,Box747]
FEATURE [Part::Chamfer] Chamfer039025078004034
  Base = -> Fusion004002009002027014004009002002008002004029002015013017006002012002031033002013006007008014029072011018024002019049062029014012006016002033001057009057
  Edges = 2 edges: [Edge7 r1=1.99 r2=3.5,Edge13 r1=1.99 r2=3.5]
FEATURE [Part::Fillet] Fillet125007020032047
  Base = -> Chamfer039025078004034
  Edges = 2 edges r=4.99: [Edge29,Edge30]
  Placement = pos=(0,0,-13.1) rot=(0,0,1;0rad)
FEATURE [Part::MultiFuse] Fusion004002009002027014004009002002008002004029002015013017006002012002031033002013006007008014029072011018024002019049062029014012006016002033001057009059  label="Fusion"
  Refine = true
  Shapes = -> [Cylinder1492098,Fillet125007020032047]
FEATURE [Part::Cut] Cut176013009033007019019008010045003002004008006021005004004004004002012033009016002012007022022  label="Cut"
  Base = -> Fusion004002009002027014004009002002008002004029002015013017006002012002031033002013006007008014029072011018024002019049062029014012006016002033001057009059
  Refine = true
  Tool = -> Cylinder1492099
FEATURE [Part::MultiFuse] Fusion004002009002027014004009002002008002004029002015013017006002012002031033002013006007008014029072011018024002019049062029014012006016002033001057009060  label="Fusion"
  Refine = true
  Shapes = -> [Cylinder1492090,Cylinder1492091,Cylinder1492092,Cylinder1492093]
FEATURE [Part::MultiFuse] Fusion004002009002027014004009002002008002004029002015013017006002012002031033002013006007008014029072011018024002019049062029014012006016002033001057009061  label="Fusion"
  Refine = true
  Shapes = -> [Cylinder1492100,Cylinder1492101,Cylinder1492102,Cylinder1492103]
FEATURE [Part::Cut] Cut176013009033007019019008010045003002004008006021005004004004004002012033009016002012007022025  label="rear-axle-knukle-holder-lower-left-ALU5mm"
  Base = -> Cut176013009033007019019008010045003002004008006021005004004004004002012033009016002012007022022
  Refine = true
  Tool = -> Fusion004002009002027014004009002002008002004029002015013017006002012002031033002013006007008014029072011018024002019049062029014012006016002033001057009061
FEATURE [Part::Feature] Part__Mirroring007002003002018002002002005004004003  label="rear-axle-knukle-holder-upper-right-ALU5mm"
  shape: bbox 14 x 24.5 x 5 mm, 21 faces (baked)
FEATURE [Part::Feature] Part__Mirroring007002003002018002002002005004004002001  label="rear-axle-knukle-holder-lower-right-ALU5mm"
  shape: bbox 14 x 24.5 x 5 mm, 21 faces (baked)
FEATURE [Part::Box] Box749  label="Cube286"
  AttacherType = Attacher::AttachEngine3D
  Height = 4.4
  Length = 24
  Placement = pos=(-12,24,7.6) rot=(0,0,1;0rad)
  Width = 12
FEATURE [Part::Box] Box750  label="Cube287"
  AttacherType = Attacher::AttachEngine3D
  Height = 4.4
  Length = 12
  Placement = pos=(-6,26,7.6) rot=(0,0,1;0rad)
  Width = 19.5
FEATURE [Part::Cylinder] Cylinder1492104
  Angle = 360
  AttacherType = Attacher::AttachEngine3D
  FirstAngle = 0
  Height = 37
  Placement = pos=(0,39,-19) rot=(0,0,1;0rad)
  Radius = 2.1
  SecondAngle = 0
FEATURE [Part::Cylinder] Cylinder1492105
  Angle = 360
  AttacherType = Attacher::AttachEngine3D
  FirstAngle = 0
  Height = 37
  Placement = pos=(-8,27.5,-19) rot=(0,0,1;0rad)
  Radius = 1.1
  SecondAngle = 0
FEATURE [Part::Cylinder] Cylinder1492106
  Angle = 360
  AttacherType = Attacher::AttachEngine3D
  FirstAngle = 0
  Height = 37
  Placement = pos=(8,33,-19) rot=(0,0,1;0rad)
  Radius = 1.1
  SecondAngle = 0
FEATURE [Part::Cylinder] Cylinder1492107
  Angle = 360
  AttacherType = Attacher::AttachEngine3D
  FirstAngle = 0
  Height = 37
  Placement = pos=(-8,33,-19) rot=(0,0,1;0rad)
  Radius = 1.1
  SecondAngle = 0
FEATURE [Part::Cylinder] Cylinder1492108
  Angle = 360
  AttacherType = Attacher::AttachEngine3D
  FirstAngle = 0
  Height = 37
  Placement = pos=(8,27.5,-19) rot=(0,0,1;0rad)
  Radius = 1.1
  SecondAngle = 0
FEATURE [Part::Cylinder] Cylinder1492109
  Angle = 360
  AttacherType = Attacher::AttachEngine3D
  FirstAngle = 0
  Height = 40
  Placement = pos=(0,24,0) rot=(-1,0,0;1.5708rad)
  Radius = 13
  SecondAngle = 0
FEATURE [Part::Cylinder] Cylinder1492110
  Angle = 360
  AttacherType = Attacher::AttachEngine3D
  FirstAngle = 0
  Height = 40
  Placement = pos=(0,24,0) rot=(-1,0,0;1.5708rad)
  Radius = 17
  SecondAngle = 0
FEATURE [Part::Cut] Cut176013009033007019019008010045003002004008006021005004004004004002012033009016002012007022024002  label="Cut"
  Base = -> Cylinder1492110
  Refine = true
  Tool = -> Cylinder1492109
FEATURE [Part::Cylinder] Cylinder1492111
  Angle = 360
  AttacherType = Attacher::AttachEngine3D
  FirstAngle = 0
  Height = 3
  Placement = pos=(8,27.5,8) rot=(0,0,1;0rad)
  Radius = 2.2
  SecondAngle = 0
FEATURE [Part::Cylinder] Cylinder1492112
  Angle = 360
  AttacherType = Attacher::AttachEngine3D
  FirstAngle = 0
  Height = 3
  Placement = pos=(-8,27.5,8) rot=(0,0,1;0rad)
  Radius = 2.2
  SecondAngle = 0
FEATURE [Part::Cylinder] Cylinder1492113
  Angle = 360
  AttacherType = Attacher::AttachEngine3D
  FirstAngle = 0
  Height = 3
  Placement = pos=(8,33,8) rot=(0,0,1;0rad)
  Radius = 2.2
  SecondAngle = 0
FEATURE [Part::Cylinder] Cylinder1492114
  Angle = 360
  AttacherType = Attacher::AttachEngine3D
  FirstAngle = 0
  Height = 3
  Placement = pos=(-8,33,8) rot=(0,0,1;0rad)
  Radius = 2.2
  SecondAngle = 0
FEATURE [Part::Cylinder] Cylinder1492115
  Angle = 360
  AttacherType = Attacher::AttachEngine3D
  FirstAngle = 0
  Height = 3
  Placement = pos=(8,27.5,8) rot=(0,0,1;0rad)
  Radius = 2.2
  SecondAngle = 0
FEATURE [Part::Cylinder] Cylinder1492116
  Angle = 360
  AttacherType = Attacher::AttachEngine3D
  FirstAngle = 0
  Height = 3
  Placement = pos=(8,33,8) rot=(0,0,1;0rad)
  Radius = 2.2
  SecondAngle = 0
FEATURE [Part::Cylinder] Cylinder1492117
  Angle = 360
  AttacherType = Attacher::AttachEngine3D
  FirstAngle = 0
  Height = 3
  Placement = pos=(-8,27.5,8) rot=(0,0,1;0rad)
  Radius = 2.2
  SecondAngle = 0
FEATURE [Part::Cylinder] Cylinder1492118
  Angle = 360
  AttacherType = Attacher::AttachEngine3D
  FirstAngle = 0
  Height = 3
  Placement = pos=(-8,33,8) rot=(0,0,1;0rad)
  Radius = 2.2
  SecondAngle = 0
FEATURE [Part::MultiFuse] Fusion004002009002027014004009002002008002004029002015013017006002012002031033002013006007008014029072011018024002019049062029014012006016002033001057009062  label="Fusion"
  Refine = true
  Shapes = -> [Cylinder1492105,Cylinder1492106,Cylinder1492107,Cylinder1492108]
FEATURE [Part::MultiFuse] Fusion088026007031024007008004081005  label="Fusion"
  Refine = true
  Shapes = -> [Box750,Box749]
FEATURE [Part::Cut] Cut176013009033007019019008010035  label="Cut"
  Base = -> Fusion088026007031024007008004081005
  Refine = true
  Tool = -> Cylinder1492104
FEATURE [Part::Fillet] Fillet125007020022
  Base = -> Cut176013009033007019019008010035
  Edges = 2 edges r=5.999: [Edge22,Edge26]
FEATURE [Part::Fillet] Fillet125007020023
  Base = -> Fillet125007020022
  Edges = 2 edges r=3: [Edge14,Edge28]
FEATURE [Part::Cut] Cut176013009033007019019008010036  label="Cut"
  Base = -> Fillet125007020023
  Refine = true
  Tool = -> Cut176013009033007019019008010045003002004008006021005004004004004002012033009016002012007022024002
FEATURE [Part::MultiFuse] Fusion004002009002027014004009002002008002004029002015013017006002012002031033002013006007008014029072011018024002019049062029014012006016002033001057009063  label="Fusion"
  Refine = true
  Shapes = -> [Cylinder1492111,Cylinder1492113,Cylinder1492112,Cylinder1492114]
FEATURE [Part::MultiFuse] Fusion088026007031024007008004081007  label="Fusion"
  Refine = true
  Shapes = -> [Cut176013009033007019019008010036,Fusion004002009002027014004009002002008002004029002015013017006002012002031033002013006007008014029072011018024002019049062029014012006016002033001057009063]
FEATURE [Part::Cut] Cut176013009033007019019008010037  label="Cut"
  Base = -> Fusion088026007031024007008004081007
  Refine = true
  Tool = -> Fusion004002009002027014004009002002008002004029002015013017006002012002031033002013006007008014029072011018024002019049062029014012006016002033001057009062
FEATURE [Part::MultiFuse] Fusion004002009002027014004009002002008002004029002015013017006002012002031033002013006007008014029072011018024002019049062029014012006016002033001057009064  label="Fusion"
  Placement = pos=(0,0,3) rot=(0,0,1;0rad)
  Refine = true
  Shapes = -> [Cylinder1492115,Cylinder1492116,Cylinder1492117,Cylinder1492118]
FEATURE [Part::Cut] Cut176013009033007019019008010038  label="Cut"
  Base = -> Cut176013009033007019019008010037
  Placement = pos=(75,-92.5,46) rot=(0,0,1;0rad)
  Refine = true
  Tool = -> Fusion004002009002027014004009002002008002004029002015013017006002012002031033002013006007008014029072011018024002019049062029014012006016002033001057009064
FEATURE [Part::Cylinder] Cylinder1492119
  Angle = 360
  AttacherType = Attacher::AttachEngine3D
  FirstAngle = 0
  Height = 8.4
  Placement = pos=(75,-53.5,56.2) rot=(0,0,1;0rad)
  Radius = 3.2
  SecondAngle = 0
FEATURE [Part::Cut] Cut176013009033007019019008010045003002004008006021005004004004004002012033009016002012007022024003  label="rear-axle-steering-knukle-upper-plate-right"
  Base = -> Cut176013009033007019019008010038
  Refine = true
  Tool = -> Cylinder1492119
FEATURE [Part::Box] Box751  label="Cube"
  AttacherType = Attacher::AttachEngine3D
  Height = 4
  Length = 10
  Placement = pos=(70,-68.5,58) rot=(0,0,1;0rad)
  Width = 20
FEATURE [Part::Chamfer] Chamfer039025078004035
  Base = -> Box751
  Edges = 1 edges: [Edge10 r1=3.99 r2=6]
FEATURE [Part::Cylinder] Cylinder1492120
  Angle = 360
  AttacherType = Attacher::AttachEngine3D
  FirstAngle = 0
  Height = 8.4
  Placement = pos=(69.5,-49,53.6) rot=(0,0,1;0rad)
  Radius = 2.2
  SecondAngle = 0
FEATURE [Part::Cylinder] Cylinder1492121
  Angle = 360
  AttacherType = Attacher::AttachEngine3D
  FirstAngle = 0
  Height = 8.4
  Placement = pos=(80.5,-49,53.6) rot=(0,0,1;0rad)
  Radius = 2.2
  SecondAngle = 0
FEATURE [Part::Cylinder] Cylinder1492122
  Angle = 360
  AttacherType = Attacher::AttachEngine3D
  FirstAngle = 0
  Height = 8.4
  Placement = pos=(69.5,-49,53.6) rot=(0,0,1;0rad)
  Radius = 0.9
  SecondAngle = 0
FEATURE [Part::Cylinder] Cylinder1492123
  Angle = 360
  AttacherType = Attacher::AttachEngine3D
  FirstAngle = 0
  Height = 8.4
  Placement = pos=(80.5,-49,53.6) rot=(0,0,1;0rad)
  Radius = 0.9
  SecondAngle = 0
FEATURE [Part::Cylinder] Cylinder1492124
  Angle = 360
  AttacherType = Attacher::AttachEngine3D
  FirstAngle = 0
  Height = 8.4
  Placement = pos=(75,-60,53.6) rot=(0,0,1;0rad)
  Radius = 0.9
  SecondAngle = 0
FEATURE [Part::MultiFuse] Fusion004002009002027014004009002002008002004029002015013017006002012002031033002013006007008014029072011018024002019049062029014012006016002033001057009065  label="Fusion"
  Refine = true
  Shapes = -> [Cylinder1492124,Cylinder1492123,Cylinder1492122]
FEATURE [Part::MultiFuse] Fusion004002009002027014004009002002008002004029002015013017006002012002031033002013006007008014029072011018024002019049062029014012006016002033001057009066  label="Fusion"
  Refine = true
  Shapes = -> [Chamfer039025078004035,Cylinder1492120,Cylinder1492121]
FEATURE [Part::Cut] Cut176013009033007019019008010045003002004008006021005004004004004002012033009016002012007022024004  label="Cut"
  Base = -> Fusion004002009002027014004009002002008002004029002015013017006002012002031033002013006007008014029072011018024002019049062029014012006016002033001057009066
  Refine = true
  Tool = -> Fusion004002009002027014004009002002008002004029002015013017006002012002031033002013006007008014029072011018024002019049062029014012006016002033001057009065
FEATURE [Part::Cut] Cut176013009033007019019008010045003002004008006021005004004004004002012033009016002012007022024005  label="Cut"
  Base = -> Cut176013009033007019019008010045003002004008006021005004004004004002012033009016002012007022024004
  Refine = true
  Tool = -> Cylinder1492119
FEATURE [Part::Feature] Part__Mirroring007002003002018002002002005004004002002  label="rear-axle-steering-knukle-upper-plate-left"
  shape: bbox 21.09 x 21.5 x 4.4 mm, 33 faces (baked)
FEATURE [Part::Feature] Part__Mirroring007002003002018002002002005004004002003001  label="rear-axle-steering-knukle-lower-plate-left"
  Placement = pos=(0,0,92) rot=(0,0,1;0rad)
  shape: bbox 21.09 x 21.5 x 4.4 mm, 33 faces (baked)
FEATURE [Part::Feature] Part__Mirroring007002003002018002002002005004004002003002  label="rear-axle-steering-knukle-lower-plate-right"
  Placement = pos=(0,0,92) rot=(0,0,1;0rad)
  shape: bbox 21.09 x 21.5 x 4.4 mm, 33 faces (baked)
FEATURE [Part::MultiFuse] Fusion004002009002027014004009002002008002004029002015013017006002012002031033002013006007008014029072011018024002019049062029014012006016002033001057009067  label="rear-axle-steering-knukle-upper-plate-right"
  Refine = true
  Shapes = -> [Cut176013009033007019019008010045003002004008006021005004004004004002012033009016002012007022024003,Cut176013009033007019019008010045003002004008006021005004004004004002012033009016002012007022024005]
FEATURE [Part::Feature] Part__Mirroring007002003002018002002002005004004002003003  label="rear-axle-steering-knukle-arm-left-ALU4mm"
  shape: bbox 24.2 x 22.25 x 4 mm, 22 faces (baked)
FEATURE [Part::Chamfer] Chamfer039025078004030
  Base = -> Box734
  Edges = 2 edges: [Edge9 r1=4 r2=3,Edge11 r1=4 r2=3]
FEATURE [Part::Cut] Cut176013009033007019019008010045003002004008006021005004004004004002012033009016002012007022024006  label="Cut"
  Base = -> Box737
  Refine = true
  Tool = -> Chamfer039025078004030
FEATURE [Part::MultiFuse] Fusion004002009002027014004009002002008002004029002015013017006002012002031033002013006007008014029072011018024002019049062029014012006016002033001057009068  label="Fusion"
  Refine = true
  Shapes = -> [Cut176013009033007019019008010045003002004008006021005004004004004002012033009016002012007022024006,Chamfer039025078004029,Chamfer039025078004026]
FEATURE [Part::Box] Box752  label="Cube"
  AttacherType = Attacher::AttachEngine3D
  Height = 15
  Length = 25
  Placement = pos=(62,-27,82) rot=(0,0,1;0rad)
  Width = 6
FEATURE [Part::Box] Box753  label="Cube"
  AttacherType = Attacher::AttachEngine3D
  Height = 15
  Length = 25
  Placement = pos=(62,21,82) rot=(0,0,1;0rad)
  Width = 6
FEATURE [App::DocumentObjectGroup] Group019  label="Hex bars"
  Group = -> [Extrude001,Extrude002,Extrude003,Extrude005]
FEATURE [Part::Cylinder] Cylinder1492125  label="Cylinder"
  Angle = 360
  AttacherType = Attacher::AttachEngine3D
  FirstAngle = 0
  Height = 34
  Placement = pos=(58,24,85) rot=(0,1,0;1.5708rad)
  Radius = 1.5
  SecondAngle = 0
FEATURE [Part::Cylinder] Cylinder1492126  label="Cylinder"
  Angle = 360
  AttacherType = Attacher::AttachEngine3D
  FirstAngle = 0
  Height = 34
  Placement = pos=(58,24,93) rot=(0,1,0;1.5708rad)
  Radius = 1.5
  SecondAngle = 0
FEATURE [Part::Cylinder] Cylinder1492127  label="Cylinder"
  Angle = 360
  AttacherType = Attacher::AttachEngine3D
  FirstAngle = 0
  Height = 34
  Placement = pos=(58,-24,93) rot=(0,1,0;1.5708rad)
  Radius = 1.5
  SecondAngle = 0
FEATURE [Part::Cylinder] Cylinder1492128  label="Cylinder"
  Angle = 360
  AttacherType = Attacher::AttachEngine3D
  FirstAngle = 0
  Height = 34
  Placement = pos=(58,-24,85) rot=(0,1,0;1.5708rad)
  Radius = 1.5
  SecondAngle = 0
FEATURE [Part::MultiFuse] Fusion004002009002027014004009002002008002004029002015013017006002012002031033002013006007008014029072011018024002019049062029014012006016002033001057009070  label="Fusion"
  Refine = true
  Shapes = -> [Cylinder1492125,Cylinder1492126,Cylinder1492127,Cylinder1492128]
FEATURE [Part::Cylinder] Cylinder1492129  label="Cylinder"
  Angle = 360
  AttacherType = Attacher::AttachEngine3D
  FirstAngle = 0
  Height = 34
  Placement = pos=(58,24,85) rot=(0,1,0;1.5708rad)
  Radius = 1.5
  SecondAngle = 0
FEATURE [Part::Cylinder] Cylinder1492130  label="Cylinder"
  Angle = 360
  AttacherType = Attacher::AttachEngine3D
  FirstAngle = 0
  Height = 34
  Placement = pos=(58,24,93) rot=(0,1,0;1.5708rad)
  Radius = 1.5
  SecondAngle = 0
FEATURE [Part::Cylinder] Cylinder1492131  label="Cylinder"
  Angle = 360
  AttacherType = Attacher::AttachEngine3D
  FirstAngle = 0
  Height = 34
  Placement = pos=(58,-24,93) rot=(0,1,0;1.5708rad)
  Radius = 1.5
  SecondAngle = 0
FEATURE [Part::Cylinder] Cylinder1492132  label="Cylinder"
  Angle = 360
  AttacherType = Attacher::AttachEngine3D
  FirstAngle = 0
  Height = 34
  Placement = pos=(58,-24,85) rot=(0,1,0;1.5708rad)
  Radius = 1.5
  SecondAngle = 0
FEATURE [Part::MultiFuse] Fusion004002009002027014004009002002008002004029002015013017006002012002031033002013006007008014029072011018024002019049062029014012006016002033001057009071  label="Fusion"
  Refine = true
  Shapes = -> [Cylinder1492129,Cylinder1492130,Cylinder1492131,Cylinder1492132]
FEATURE [Part::Cut] Cut176013009033007019019008010045003002004008006021005004004004004002012033009016002012007022024009  label="Cut"
  Base = -> Cut176013009033007019019008010045003002004008006021005004004004004002012033009016002012007022014
  Refine = true
  Tool = -> Fusion004002009002027014004009002002008002004029002015013017006002012002031033002013006007008014029072011018024002019049062029014012006016002033001057009070
FEATURE [Part::Cut] Cut176013009033007019019008010045003002004008006021005004004004004002012033009016002012007022024010  label="Cut"
  Base = -> Cut176013009033007019019008010045003002004008006021005004004004004002012033009016002012007022015
  Refine = true
  Tool = -> Fusion004002009002027014004009002002008002004029002015013017006002012002031033002013006007008014029072011018024002019049062029014012006016002033001057009071
FEATURE [Part::Box] Box754  label="Cube"
  AttacherType = Attacher::AttachEngine3D
  Height = 5
  Length = 25
  Placement = pos=(62,-17,64.5) rot=(0,0,1;0rad)
  Width = 34
FEATURE [Part::Cylinder] Cylinder1492133  label="Cylinder"
  Angle = 360
  AttacherType = Attacher::AttachEngine3D
  FirstAngle = 0
  Height = 34
  Placement = pos=(58,6,67) rot=(0,1,0;1.5708rad)
  Radius = 1.1
  SecondAngle = 0
FEATURE [Part::Cylinder] Cylinder1492134  label="Cylinder"
  Angle = 360
  AttacherType = Attacher::AttachEngine3D
  FirstAngle = 0
  Height = 34
  Placement = pos=(58,-6,67) rot=(0,1,0;1.5708rad)
  Radius = 1.1
  SecondAngle = 0
FEATURE [Part::MultiFuse] Fusion004002009002027014004009002002008002004029002015013017006002012002031033002013006007008014029072011018024002019049062029014012006016002033001057009072  label="Fusion"
  Refine = true
  Shapes = -> [Cylinder1492134,Cylinder1492133]
FEATURE [Part::Cut] Cut176013009033007019019008010045003002004008006021005004004004004002012033009016002012007022024011  label="rear-axle-front-holder-ALU5mm"
  Base = -> Cut176013009033007019019008010045003002004008006021005004004004004002012033009016002012007022024009
  Refine = true
  Tool = -> Fusion004002009002027014004009002002008002004029002015013017006002012002031033002013006007008014029072011018024002019049062029014012006016002033001057009072
FEATURE [Part::Cylinder] Cylinder1492135  label="Cylinder"
  Angle = 360
  AttacherType = Attacher::AttachEngine3D
  FirstAngle = 0
  Height = 34
  Placement = pos=(58,6,67) rot=(0,1,0;1.5708rad)
  Radius = 1.1
  SecondAngle = 0
FEATURE [Part::Cylinder] Cylinder1492136  label="Cylinder"
  Angle = 360
  AttacherType = Attacher::AttachEngine3D
  FirstAngle = 0
  Height = 34
  Placement = pos=(58,-6,67) rot=(0,1,0;1.5708rad)
  Radius = 1.1
  SecondAngle = 0
FEATURE [Part::MultiFuse] Fusion004002009002027014004009002002008002004029002015013017006002012002031033002013006007008014029072011018024002019049062029014012006016002033001057009073  label="Fusion"
  Refine = true
  Shapes = -> [Cylinder1492136,Cylinder1492135]
FEATURE [Part::Cut] Cut176013009033007019019008010045003002004008006021005004004004004002012033009016002012007022024012  label="rear-axle-rear-holder-ALU5mm"
  Base = -> Cut176013009033007019019008010045003002004008006021005004004004004002012033009016002012007022024010
  Placement = pos=(-1,0,0) rot=(0,0,1;0rad)
  Refine = true
  Tool = -> Fusion004002009002027014004009002002008002004029002015013017006002012002031033002013006007008014029072011018024002019049062029014012006016002033001057009073
FEATURE [Part::Cylinder] Cylinder1492137  label="Cylinder"
  Angle = 360
  AttacherType = Attacher::AttachEngine3D
  FirstAngle = 0
  Height = 34
  Placement = pos=(58,6,67) rot=(0,1,0;1.5708rad)
  Radius = 0.8
  SecondAngle = 0
FEATURE [Part::Cylinder] Cylinder1492138  label="Cylinder"
  Angle = 360
  AttacherType = Attacher::AttachEngine3D
  FirstAngle = 0
  Height = 34
  Placement = pos=(58,-6,67) rot=(0,1,0;1.5708rad)
  Radius = 0.8
  SecondAngle = 0
FEATURE [Part::MultiFuse] Fusion004002009002027014004009002002008002004029002015013017006002012002031033002013006007008014029072011018024002019049062029014012006016002033001057009074  label="Fusion"
  Refine = true
  Shapes = -> [Cylinder1492138,Cylinder1492137]
FEATURE [Part::Cut] Cut176013009033007019019008010045003002004008006021005004004004004002012033009016002012007022024013  label="Cut"
  Base = -> Box754
  Refine = true
  Tool = -> Fusion004002009002027014004009002002008002004029002015013017006002012002031033002013006007008014029072011018024002019049062029014012006016002033001057009074
FEATURE [Part::Feature] Cut176013009033007019019008010045003002004008006021005004004004004002012033009016002012007022024014  label="BEARING-5x9x3-MR95ZZ"
  Placement = pos=(154,-50,9) rot=(0,0,1;0rad)
  shape: bbox 9 x 3 x 9 mm, 4 faces (baked)
FEATURE [Part::Feature] Cut176013009033007019019008010045003002004008006021005004004004004002012033009016002012007022024016  label="BEARING-5x9x3-MR95ZZ"
  Placement = pos=(154,-47,9) rot=(0,0,1;0rad)
  shape: bbox 9 x 3 x 9 mm, 4 faces (baked)
FEATURE [Part::Feature] Cut176013009033007019019008010045003002004008006021005004004004004002012033009016002012007022024017  label="BEARING-5x9x3-MR95ZZ"
  Placement = pos=(154,-88,9) rot=(0,0,1;0rad)
  shape: bbox 9 x 3 x 9 mm, 4 faces (baked)
FEATURE [Part::Cylinder] Cylinder1492143  label="Cylinder"
  Angle = 360
  AttacherType = Attacher::AttachEngine3D
  FirstAngle = 0
  Height = 124
  Placement = pos=(260,-62.5,62) rot=(-1,0,0;1.5708rad)
  Radius = 3
  SecondAngle = 0
FEATURE [Part::Cylinder] Cylinder1492144  label="Cylinder"
  Angle = 360
  AttacherType = Attacher::AttachEngine3D
  FirstAngle = 0
  Height = 2.5
  Placement = pos=(260,-18.5,62) rot=(-1,0,0;1.5708rad)
  Radius = 4
  SecondAngle = 0
FEATURE [Part::Cylinder] Cylinder1492145  label="Cylinder"
  Angle = 360
  AttacherType = Attacher::AttachEngine3D
  FirstAngle = 0
  Height = 3.2
  Placement = pos=(260,-62.5,62) rot=(-1,0,0;1.5708rad)
  Radius = 4.6
  SecondAngle = 0
FEATURE [Part::Cylinder] Cylinder1492146  label="Cylinder"
  Angle = 360
  AttacherType = Attacher::AttachEngine3D
  FirstAngle = 0
  Height = 2.5
  Placement = pos=(260,16,62) rot=(-1,0,0;1.5708rad)
  Radius = 4
  SecondAngle = 0
FEATURE [Part::Cylinder] Cylinder1492147  label="Cylinder"
  Angle = 360
  AttacherType = Attacher::AttachEngine3D
  FirstAngle = 0
  Height = 3.2
  Placement = pos=(260,58.3,62) rot=(-1,0,0;1.5708rad)
  Radius = 4.6
  SecondAngle = 0
FEATURE [Part::Cylinder] Cylinder1492153  label="Cylinder"
  Angle = 360
  AttacherType = Attacher::AttachEngine3D
  FirstAngle = 0
  Height = 64
  Placement = pos=(260,-32,78) rot=(-1,0,0;1.5708rad)
  Radius = 1.5
  SecondAngle = 0
FEATURE [Part::Box] Box755  label="Cube"
  AttacherType = Attacher::AttachEngine3D
  Height = 15
  Length = 20
  Placement = pos=(250,21,67) rot=(0,0,1;0rad)
  Width = 6
FEATURE [Part::Fillet] Fillet125007020032048
  Base = -> Box755
  Edges = 2 edges r=8: [Edge2,Edge6]
FEATURE [Part::Cylinder] Cylinder1492156  label="Cylinder"
  Angle = 360
  AttacherType = Attacher::AttachEngine3D
  FirstAngle = 0
  Height = 40
  Placement = pos=(264,16,69) rot=(-1,0,0;1.5708rad)
  Radius = 1.3
  SecondAngle = 0
FEATURE [Part::Cylinder] Cylinder1492157  label="Cylinder"
  Angle = 360
  AttacherType = Attacher::AttachEngine3D
  FirstAngle = 0
  Height = 13.2
  Placement = pos=(260,21,62) rot=(-1,0,0;1.5708rad)
  Radius = 4.65
  SecondAngle = 0
FEATURE [Part::Cylinder] Cylinder1492158  label="Cylinder"
  Angle = 360
  AttacherType = Attacher::AttachEngine3D
  FirstAngle = 0
  Height = 13.2
  Placement = pos=(260,-34.2,62) rot=(-1,0,0;1.5708rad)
  Radius = 4.65
  SecondAngle = 0
FEATURE [Part::Cone] Cone
  Angle = 360
  AttacherType = Attacher::AttachEngine3D
  Height = 2.6
  Placement = pos=(264,18.6,69) rot=(1,0,0;1.5708rad)
  Radius1 = 1.5
  Radius2 = 3
FEATURE [Part::MultiFuse] Fusion004002009002027014004009002002008002004029002015013017006002012002031033002013006007008014029072011018024002019049062029014012006016002033001057009078004002002  label="SCREW-V-M3x40"
  Placement = pos=(-0.5,0,0) rot=(0,0,1;0rad)
  Refine = true
  Shapes = -> [Cylinder1492156,Cone]
FEATURE [Part::Cone] Cone001
  Angle = 360
  AttacherType = Attacher::AttachEngine3D
  Height = 2.6
  Placement = pos=(264,18.6,69) rot=(1,0,0;1.5708rad)
  Radius1 = 1.5
  Radius2 = 3
FEATURE [Part::Cylinder] Cylinder1492159  label="Cylinder"
  Angle = 360
  AttacherType = Attacher::AttachEngine3D
  FirstAngle = 0
  Height = 40
  Placement = pos=(264,16,69) rot=(-1,0,0;1.5708rad)
  Radius = 1.3
  SecondAngle = 0
FEATURE [Part::MultiFuse] Fusion004002009002027014004009002002008002004029002015013017006002012002031033002013006007008014029072011018024002019049062029014012006016002033001057009078004002003  label="SCREW-V-M3x40"
  Placement = pos=(-7.5,0,-14) rot=(0,0,1;0rad)
  Refine = true
  Shapes = -> [Cylinder1492159,Cone001]
FEATURE [Part::Cylinder] Cylinder1492160  label="Cylinder"
  Angle = 360
  AttacherType = Attacher::AttachEngine3D
  FirstAngle = 0
  Height = 40
  Placement = pos=(266,16,68) rot=(-1,0,0;1.5708rad)
  Radius = 1.3
  SecondAngle = 0
FEATURE [Part::Cylinder] Cylinder1492161  label="Cylinder"
  Angle = 360
  AttacherType = Attacher::AttachEngine3D
  FirstAngle = 0
  Height = 40
  Placement = pos=(254,16,56) rot=(-1,0,0;1.5708rad)
  Radius = 1.3
  SecondAngle = 0
FEATURE [Part::Cylinder] Cylinder1492162  label="Cylinder"
  Angle = 360
  AttacherType = Attacher::AttachEngine3D
  FirstAngle = 0
  Height = 3.5
  Placement = pos=(276,21,62) rot=(-1,0,0;1.5708rad)
  Radius = 3
  SecondAngle = 0
FEATURE [Part::Cylinder] Cylinder1492163  label="Cylinder"
  Angle = 360
  AttacherType = Attacher::AttachEngine3D
  FirstAngle = 0
  Height = 3.5
  Placement = pos=(244,21,62) rot=(-1,0,0;1.5708rad)
  Radius = 3
  SecondAngle = 0
FEATURE [Part::Cylinder] Cylinder1492164  label="Cylinder"
  Angle = 360
  AttacherType = Attacher::AttachEngine3D
  FirstAngle = 0
  Height = 3.5
  Placement = pos=(260,21,46) rot=(-1,0,0;1.5708rad)
  Radius = 3
  SecondAngle = 0
FEATURE [Part::MultiFuse] Fusion004002009002027014004009002002008002004029002015013017006002012002031033002013006007008014029072011018024002019049062029014012006016002033001057009078004002005  label="Fusion"
  Refine = true
  Shapes = -> [Cylinder1492162,Cylinder1492163,Cylinder1492164]
FEATURE [Part::Cylinder] Cylinder1492165  label="Cylinder"
  Angle = 360
  AttacherType = Attacher::AttachEngine3D
  FirstAngle = 0
  Height = 8.5
  Placement = pos=(276,16,62) rot=(-1,0,0;1.5708rad)
  Radius = 1.5
  SecondAngle = 0
FEATURE [Part::Cylinder] Cylinder1492166  label="Cylinder"
  Angle = 360
  AttacherType = Attacher::AttachEngine3D
  FirstAngle = 0
  Height = 8.5
  Placement = pos=(244,16,62) rot=(-1,0,0;1.5708rad)
  Radius = 1.5
  SecondAngle = 0
FEATURE [Part::Cylinder] Cylinder1492167  label="Cylinder"
  Angle = 360
  AttacherType = Attacher::AttachEngine3D
  FirstAngle = 0
  Height = 8.5
  Placement = pos=(260,16,46) rot=(-1,0,0;1.5708rad)
  Radius = 1.5
  SecondAngle = 0
FEATURE [Part::MultiFuse] Fusion004002009002027014004009002002008002004029002015013017006002012002031033002013006007008014029072011018024002019049062029014012006016002033001057009078004002006  label="Fusion"
  Refine = true
  Shapes = -> [Cylinder1492165,Cylinder1492166,Cylinder1492167]
FEATURE [Part::Cone] Cone002  label="Cone"
  Angle = 360
  AttacherType = Attacher::AttachEngine3D
  Height = 1.25
  Radius1 = 2
  Radius2 = 0.9
FEATURE [Part::Cylinder] Cylinder1492168  label="Cylinder"
  Angle = 360
  AttacherType = Attacher::AttachEngine3D
  FirstAngle = 0
  Height = 16
  Radius = 0.9
  SecondAngle = 0
FEATURE [Part::MultiFuse] Fusion004002009002027014004009002002008002004029002015013017006002012002031033002013006007008014029072011018024002019049062029014012006016002033001057009078004002010  label="SCREW-V-M2x16"
  Placement = pos=(0,0,0) rot=(1,0,0;1.5708rad)
  Refine = true
  Shapes = -> [Cylinder1492168,Cone002]
FEATURE [App::DocumentObjectGroup] Group014  label="Screws"
  Group = -> [Fusion088026007031024007008004100051009001012,Fusion088026007031024007008004100051009001012005,Fusion004002009002027014004009002002008002004029002015013017006002012002031033002013006007008014029072011018024002019049062029014012006016002033001057009078004002003,+2 more]
FEATURE [Part::Feature] Fusion004002009002027014004009002002008002004029002015013017006002012002031033002013006007008014029072011018024002019049062029014012006016002033001057009078004002010001  label="SCREW-V-M2x16"
  Placement = pos=(268,61.5,62) rot=(1,0,0;1.5708rad)
  shape: bbox 4 x 16 x 4 mm, 4 faces (baked)
FEATURE [Part::Feature] Fusion004002009002027014004009002002008002004029002015013017006002012002031033002013006007008014029072011018024002019049062029014012006016002033001057009078004002010002  label="SCREW-V-M2x16"
  Placement = pos=(252,61.5,62) rot=(1,0,0;1.5708rad)
  shape: bbox 4 x 16 x 4 mm, 4 faces (baked)
FEATURE [Part::Feature] Fusion004002009002027014004009002002008002004029002015013017006002012002031033002013006007008014029072011018024002019049062029014012006016002033001057009078004002010003  label="SCREW-V-M2x16"
  Placement = pos=(260,61.5,54) rot=(1,0,0;1.5708rad)
  shape: bbox 4 x 16 x 4 mm, 4 faces (baked)
FEATURE [Part::Feature] Fusion004002009002027014004009002002008002004029002015013017006002012002031033002013006007008014029072011018024002019049062029014012006016002033001057009078004002010004  label="SCREW-V-M2x16"
  Placement = pos=(260,61.5,70) rot=(1,0,0;1.5708rad)
  shape: bbox 4 x 16 x 4 mm, 4 faces (baked)
FEATURE [Part::MultiFuse] Fusion004002009002027014004009002002008002004029002015013017006002012002031033002013006007008014029072011018024002019049062029014012006016002033001057009078004002010005  label="Fusion"
  Refine = true
  Shapes = -> [Fusion004002009002027014004009002002008002004029002015013017006002012002031033002013006007008014029072011018024002019049062029014012006016002033001057009078004002010001,Fusion004002009002027014004009002002008002004029002015013017006002012002031033002013006007008014029072011018024002019049062029014012006016002033001057009078004002010002,+2 more]
FEATURE [Part::Feature] Cut176013009033007019019008010045003002004008006021005004004004004002012033009016002012007022024028  label="BEARING-5x8x2.5-MR85ZZ"
  Placement = pos=(185,-85,16) rot=(0,0,1;0rad)
  shape: bbox 8 x 2.5 x 8 mm, 4 faces (baked)
FEATURE [Part::Feature] Cut176013009033007019019008010045003002004008006021005004004004004002012033009016002012007022024029  label="BEARING-5x8x2.5-MR85ZZ"
  Placement = pos=(185,-50.5,16) rot=(0,0,1;0rad)
  shape: bbox 8 x 2.5 x 8 mm, 4 faces (baked)
FEATURE [Part::Cylinder] Cylinder1492169  label="Cylinder"
  Angle = 360
  AttacherType = Attacher::AttachEngine3D
  FirstAngle = 0
  Height = 42
  Placement = pos=(277,-21,82) rot=(-1,0,0;1.5708rad)
  Radius = 1.5
  SecondAngle = 0
FEATURE [Part::Cylinder] Cylinder1492170  label="Cylinder"
  Angle = 360
  AttacherType = Attacher::AttachEngine3D
  FirstAngle = 0
  Height = 42
  Placement = pos=(243,-21,82) rot=(-1,0,0;1.5708rad)
  Radius = 1.5
  SecondAngle = 0
FEATURE [Part::Cylinder] Cylinder1492171  label="Cylinder"
  Angle = 360
  AttacherType = Attacher::AttachEngine3D
  FirstAngle = 0
  Height = 42
  Placement = pos=(240,-21,39) rot=(-1,0,0;1.5708rad)
  Radius = 1.5
  SecondAngle = 0
FEATURE [Part::Cylinder] Cylinder1492172  label="Cylinder"
  Angle = 360
  AttacherType = Attacher::AttachEngine3D
  FirstAngle = 0
  Height = 42
  Placement = pos=(277,-21,39) rot=(-1,0,0;1.5708rad)
  Radius = 1.5
  SecondAngle = 0
FEATURE [Part::Feature] Cut176013009033007019019008010045003002004008006021005004004004004002012033009016002012007022024034  label="BUSH-5x11x4"
  Placement = pos=(185,-132,16) rot=(0,0,1;0rad)
  shape: bbox 11 x 4 x 11 mm, 4 faces (baked)
FEATURE [Part::Cylinder] Cylinder1492179  label="Cylinder"
  Angle = 360
  AttacherType = Attacher::AttachEngine3D
  FirstAngle = 0
  Height = 42
  Placement = pos=(263.5,-21,69) rot=(-1,0,0;1.5708rad)
  Radius = 1.5
  SecondAngle = 0
FEATURE [Part::Cylinder] Cylinder1492180  label="Cylinder"
  Angle = 360
  AttacherType = Attacher::AttachEngine3D
  FirstAngle = 0
  Height = 42
  Placement = pos=(256.5,-21,55) rot=(-1,0,0;1.5708rad)
  Radius = 1.5
  SecondAngle = 0
FEATURE [Part::Cylinder] Cylinder1492181  label="Cylinder"
  Angle = 360
  AttacherType = Attacher::AttachEngine3D
  FirstAngle = 0
  Height = 42
  Placement = pos=(274,-21,62) rot=(-1,0,0;1.5708rad)
  Radius = 1.3
  SecondAngle = 0
FEATURE [Part::Cylinder] Cylinder1492182  label="Cylinder"
  Angle = 360
  AttacherType = Attacher::AttachEngine3D
  FirstAngle = 0
  Height = 42
  Placement = pos=(246,-21,62) rot=(-1,0,0;1.5708rad)
  Radius = 1.3
  SecondAngle = 0
FEATURE [Part::Cylinder] Cylinder1492183  label="Cylinder"
  Angle = 360
  AttacherType = Attacher::AttachEngine3D
  FirstAngle = 0
  Height = 42
  Placement = pos=(260,-21,48) rot=(-1,0,0;1.5708rad)
  Radius = 1.3
  SecondAngle = 0
FEATURE [Part::MultiFuse] Fusion004002009002027014004009002002008002004029002015013017006002012002031033002013006007008014029072011018024002019049062029014012006016002033001057009078004002010019  label="Fusion"
  Refine = true
  Shapes = -> [Cylinder1492179,Cylinder1492180]
FEATURE [Part::MultiFuse] Fusion004002009002027014004009002002008002004029002015013017006002012002031033002013006007008014029072011018024002019049062029014012006016002033001057009078004002010020  label="Fusion"
  Refine = true
  Shapes = -> [Cylinder1492181,Cylinder1492182,Cylinder1492183]
FEATURE [Part::MultiFuse] Fusion004002009002027014004009002002008002004029002015013017006002012002031033002013006007008014029072011018024002019049062029014012006016002033001057009078004002010021  label="Fusion"
  Refine = true
  Shapes = -> [Fusion004002009002027014004009002002008002004029002015013017006002012002031033002013006007008014029072011018024002019049062029014012006016002033001057009078004002010019,Fusion004002009002027014004009002002008002004029002015013017006002012002031033002013006007008014029072011018024002019049062029014012006016002033001057009078004002010020]
FEATURE [Part::Cylinder] Cylinder1492206  label="Cylinder"
  Angle = 360
  AttacherType = Attacher::AttachEngine3D
  FirstAngle = 0
  Height = 3
  Placement = pos=(229,21,55) rot=(-1,0,0;1.5708rad)
  Radius = 11
  SecondAngle = 0
FEATURE [Part::Cylinder] Cylinder1492207  label="Cylinder"
  Angle = 360
  AttacherType = Attacher::AttachEngine3D
  FirstAngle = 0
  Height = 9
  Placement = pos=(221.5,16,55) rot=(-1,0,0;1.5708rad)
  Radius = 1.25
  SecondAngle = 0
FEATURE [Part::Cylinder] Cylinder1492208  label="Cylinder"
  Angle = 360
  AttacherType = Attacher::AttachEngine3D
  FirstAngle = 0
  Height = 9
  Placement = pos=(235.5,16,55) rot=(-1,0,0;1.5708rad)
  Radius = 1.25
  SecondAngle = 0
FEATURE [Part::Cylinder] Cylinder1492209  label="Cylinder"
  Angle = 360
  AttacherType = Attacher::AttachEngine3D
  FirstAngle = 0
  Height = 9
  Placement = pos=(228.5,16,61.5) rot=(-1,0,0;1.5708rad)
  Radius = 1.25
  SecondAngle = 0
FEATURE [Part::Cylinder] Cylinder1492210  label="Cylinder"
  Angle = 360
  AttacherType = Attacher::AttachEngine3D
  FirstAngle = 0
  Height = 9
  Placement = pos=(228.5,16,48.5) rot=(-1,0,0;1.5708rad)
  Radius = 1.25
  SecondAngle = 0
FEATURE [Part::MultiFuse] Fusion004002009002027014004009002002008002004029002015013017006002012002031033002013006007008014029072011018024002019049062029014012006016002033001057009078004002010026  label="Fusion"
  Placement = pos=(0.5,0,0) rot=(0,0,1;0rad)
  Refine = true
  Shapes = -> [Cylinder1492210,Cylinder1492207,Cylinder1492208,Cylinder1492209]
FEATURE [Part::Fillet] Fillet125007020032049
  Base = -> Cylinder1492206
  Edges = 1 edges r=1: [Edge3]
FEATURE [Part::Cylinder] Cylinder1492211  label="Cylinder"
  Angle = 360
  AttacherType = Attacher::AttachEngine3D
  FirstAngle = 0
  Height = 9
  Placement = pos=(221.5,16,55) rot=(-1,0,0;1.5708rad)
  Radius = 1.5
  SecondAngle = 0
FEATURE [Part::Cylinder] Cylinder1492212  label="Cylinder"
  Angle = 360
  AttacherType = Attacher::AttachEngine3D
  FirstAngle = 0
  Height = 9
  Placement = pos=(235.5,16,55) rot=(-1,0,0;1.5708rad)
  Radius = 1.5
  SecondAngle = 0
FEATURE [Part::Cylinder] Cylinder1492213  label="Cylinder"
  Angle = 360
  AttacherType = Attacher::AttachEngine3D
  FirstAngle = 0
  Height = 9
  Placement = pos=(228.5,16,61.5) rot=(-1,0,0;1.5708rad)
  Radius = 1.5
  SecondAngle = 0
FEATURE [Part::Cylinder] Cylinder1492214  label="Cylinder"
  Angle = 360
  AttacherType = Attacher::AttachEngine3D
  FirstAngle = 0
  Height = 9
  Placement = pos=(228.5,16,48.5) rot=(-1,0,0;1.5708rad)
  Radius = 1.5
  SecondAngle = 0
FEATURE [Part::MultiFuse] Fusion004002009002027014004009002002008002004029002015013017006002012002031033002013006007008014029072011018024002019049062029014012006016002033001057009078004002010027  label="Fusion"
  Placement = pos=(0.5,0,0) rot=(0,0,1;0rad)
  Refine = true
  Shapes = -> [Cylinder1492214,Cylinder1492211,Cylinder1492212,Cylinder1492213]
FEATURE [Part::Box] Box756  label="Cube"
  AttacherType = Attacher::AttachEngine3D
  Height = 12
  Length = 20
  Placement = pos=(250,26.5,62) rot=(0,0,1;0rad)
  Width = 6
FEATURE [Part::Cylinder] Cylinder1492215  label="Cylinder"
  Angle = 360
  AttacherType = Attacher::AttachEngine3D
  FirstAngle = 0
  Height = 75
  Placement = pos=(208,-3,77.5) rot=(0,1,0;1.5708rad)
  Radius = 1.5
  SecondAngle = 0
FEATURE [App::DocumentObjectGroup] Group011  label="Working"
  Group = -> [Cylinder1492215]
FEATURE [Part::Part2DObjectPython] Line022  label="front-axle-diff-path"  # Draft 2D object (typed FeaturePython)
  Closed = true
  End = (350,0,55)
  FilletRadius = 0
  MapMode = 5
  Placement = pos=(0,0,55) rot=(0,0,1;0rad)
  Points = (2) [(160,0,0),(350,0,0)]
  Start = (160,0,55)
FEATURE [App::DocumentObjectGroup] Group004  label="Joints"
  Group = -> [Line016,Line015,Line013,Line017,Line010,Line011,Line008,Line009,Line019,Line020,Line021,Line022]
FEATURE [Part::MultiFuse] Fusion004002009002027014004009002002008002004029002015013017006002012002031033002013006007008014029072011018024002019049062029014012006016002033001057009078004002010030  label="Fusion"
  Refine = true
  Shapes = -> [Cylinder1016,Fillet125007020032034,Fillet125007020032036,Fillet125007020032040,Fillet125007020032048,Box756,Fusion004002009002027014004009002002008002004029002015013017006002012002031033002013006007008014029072011018024002019049062029014012006016002033001057009078004002005]
FEATURE [Part::Cylinder] Cylinder1492216  label="Cylinder"
  Angle = 360
  AttacherType = Attacher::AttachEngine3D
  FirstAngle = 0
  Height = 40
  Placement = pos=(266,16,56) rot=(-1,0,0;1.5708rad)
  Radius = 1.3
  SecondAngle = 0
FEATURE [Part::Cylinder] Cylinder1492217  label="Cylinder"
  Angle = 360
  AttacherType = Attacher::AttachEngine3D
  FirstAngle = 0
  Height = 40
  Placement = pos=(254,16,68) rot=(-1,0,0;1.5708rad)
  Radius = 1.3
  SecondAngle = 0
FEATURE [Part::MultiFuse] Fusion004002009002027014004009002002008002004029002015013017006002012002031033002013006007008014029072011018024002019049062029014012006016002033001057009078004002004  label="Fusion"
  Refine = true
  Shapes = -> [Cylinder1492160,Cylinder1492161,Cylinder1492216,Cylinder1492217]
FEATURE [Part::MultiFuse] Fusion004002009002027014004009002002008002004029002015013017006002012002031033002013006007008014029072011018024002019049062029014012006016002033001057009078004002008  label="Fusion"
  Refine = true
  Shapes = -> [Fusion004002009002027014004009002002008002004029002015013017006002012002031033002013006007008014029072011018024002019049062029014012006016002033001057009078004002004,Fusion004002009002027014004009002002008002004029002015013017006002012002031033002013006007008014029072011018024002019049062029014012006016002033001057009078004002006]
FEATURE [Part::Chamfer] Chamfer039025078004036
  Base = -> Cylinder1492157
  Edges = 1 edges r=1.5: [Edge3]
FEATURE [Part::Chamfer] Chamfer039025078004037
  Base = -> Cylinder1492158
  Edges = 1 edges r=1.5: [Edge2]
FEATURE [Part::MultiFuse] Fusion004002009002027014004009002002008002004029002015013017006002012002031033002013006007008014029072011018024002019049062029014012006016002033001057009078004002010031  label="front-axle-carving"
  Refine = true
  Shapes = -> [Cylinder1492143,Cylinder1492144,Cylinder1492145,Cylinder1492146,Cylinder1492147,Chamfer039025078004036,Chamfer039025078004037]
FEATURE [Part::Feature] Fusion004002009002027014004009002002008002004029002015013017006002012002031033002013006007008014029072011018024002019049062029014012006016002033001057009078004002010031001  label="front-axle-carving"
  shape: bbox 9.3 x 124 x 9.3 mm, 25 faces (baked)
FEATURE [Part::MultiFuse] Fusion004002009002027014004009002002008002004029002015013017006002012002031033002013006007008014029072011018024002019049062029014012006016002033001057009078004002010031002  label="Fusion"
  Refine = true
  Shapes = -> [Cylinder1492153,Fusion004002009002027014004009002002008002004029002015013017006002012002031033002013006007008014029072011018024002019049062029014012006016002033001057009078004002010031001,Fusion004002009002027014004009002002008002004029002015013017006002012002031033002013006007008014029072011018024002019049062029014012006016002033001057009078004002008,+1 more]
FEATURE [Part::Cut] Cut  label="front-axle-left"
  Base = -> Fusion004002009002027014004009002002008002004029002015013017006002012002031033002013006007008014029072011018024002019049062029014012006016002033001057009078004002010030
  Refine = true
  Tool = -> Fusion004002009002027014004009002002008002004029002015013017006002012002031033002013006007008014029072011018024002019049062029014012006016002033001057009078004002010031002
FEATURE [Part::Feature] Cut176013009033007019019008010045003002004008006021005004004004004002012033009016002012007022024046  label="BEARING-5x9x3-MR95ZZ"
  Placement = pos=(185,-7.5,16) rot=(0,0,1;0rad)
  shape: bbox 9 x 3 x 9 mm, 4 faces (baked)
FEATURE [Part::Feature] Cut176013009033007019019008010045003002004008006021005004004004004002012033009016002012007022024015  label="BEARING-5x9x3-MR95ZZ"
  Placement = pos=(154,-85,9) rot=(0,0,1;0rad)
  shape: bbox 9 x 3 x 9 mm, 4 faces (baked)
FEATURE [Part::Feature] Cut176013009033007019019008010045003002004008006021005004004004004002012033009016002012007022024047  label="BEARING-5x9x3-MR95ZZ"
  Placement = pos=(185,-127.5,16) rot=(0,0,1;0rad)
  shape: bbox 9 x 3 x 9 mm, 4 faces (baked)
FEATURE [App::DocumentObjectGroup] Group010  label="BEARINGS"
  Group = -> [Cut176013009033007019019008010045003002004008006021005004004004004002012019,Cut176013009033007019019008010045003002004008006021005004004004004002012020,Cut176013009033007019019008010045003002004008006021005004004004004002012033009016002012014,Cut176013009033007019019008010045003002004008006021005004004004004002012033009016002012015,+12 more]
FEATURE [Part::Feature] Part__Mirroring007002003002018002002002005004004002003004004  label="front-hub-external-right"
  shape: bbox 30 x 10 x 30 mm, 32 faces (baked)
FEATURE [Part::Feature] Part__Mirroring007002003002018002002002005004004002003004003001  label="front-hub-internal-right"
  shape: bbox 30 x 4 x 30 mm, 22 faces (baked)
FEATURE [Part::Box] Box757  label="Cube"
  AttacherType = Attacher::AttachEngine3D
  Height = 10.5
  Length = 10.5
  Placement = pos=(254.75,8,56.75) rot=(0,0,1;0rad)
  Width = 6
FEATURE [Part::Cylinder] Cylinder1492218  label="Cylinder"
  Angle = 360
  AttacherType = Attacher::AttachEngine3D
  FirstAngle = 0
  Height = 8
  Placement = pos=(260,8,62) rot=(-1,0,0;1.5708rad)
  Radius = 4
  SecondAngle = 0
FEATURE [Part::Cylinder] Cylinder1492219  label="Cylinder"
  Angle = 360
  AttacherType = Attacher::AttachEngine3D
  FirstAngle = 0
  Height = 20
  Placement = pos=(260,11,52) rot=(0,0,1;1.5708rad)
  Radius = 1
  SecondAngle = 0
FEATURE [Part::Box] Box758  label="Cube"
  AttacherType = Attacher::AttachEngine3D
  Height = 20
  Length = 16
  Placement = pos=(252,8,52) rot=(0,0,1;0rad)
  Width = 8
FEATURE [Part::MultiFuse] Fusion004002009002027014004009002002008002004029002015013017006002012002031033002013006007008014029072011018024002019049062029014012006016002033001057009078004002010031003  label="Fusion"
  Refine = true
  Shapes = -> [Cylinder1492219,Box757,Cylinder1492218]
FEATURE [Part::Cut] Cut176013009033007019019008010045003002004008006021005004004004004002012033009016002012007022024048  label="diff-front-gear-lock-TOOL"
  Base = -> Box758
  Refine = true
  Tool = -> Fusion004002009002027014004009002002008002004029002015013017006002012002031033002013006007008014029072011018024002019049062029014012006016002033001057009078004002010031003
FEATURE [Part::Box] Box759  label="Cube"
  AttacherType = Attacher::AttachEngine3D
  Height = 10.5
  Length = 10.5
  Placement = pos=(254.75,8,56.75) rot=(0,0,1;0rad)
  Width = 4.5
FEATURE [Part::Box] Box760  label="Cube"
  AttacherType = Attacher::AttachEngine3D
  Height = 20
  Length = 16
  Placement = pos=(220.5,10,45) rot=(0,0,1;0rad)
  Width = 6
FEATURE [Part::Cylinder] Cylinder1492220  label="Cylinder"
  Angle = 360
  AttacherType = Attacher::AttachEngine3D
  FirstAngle = 0
  Height = 11
  Placement = pos=(260,4,62) rot=(-1,0,0;1.5708rad)
  Radius = 4
  SecondAngle = 0
FEATURE [Part::Cylinder] Cylinder1492221  label="Cylinder"
  Angle = 360
  AttacherType = Attacher::AttachEngine3D
  FirstAngle = 0
  Height = 20
  Placement = pos=(260,10.25,52) rot=(0,0,1;1.5708rad)
  Radius = 1
  SecondAngle = 0
FEATURE [Part::MultiFuse] Fusion004002009002027014004009002002008002004029002015013017006002012002031033002013006007008014029072011018024002019049062029014012006016002033001057009078004002010031004  label="Fusion"
  Placement = pos=(-31.5,3.5,-7) rot=(0,0,1;0rad)
  Refine = true
  Shapes = -> [Cylinder1492221,Box759,Cylinder1492220]
FEATURE [Part::Cut] Cut176013009033007019019008010045003002004008006021005004004004004002012033009016002012007022024049  label="diff-rear-gear-lock-TOOL"
  Base = -> Box760
  Refine = true
  Tool = -> Fusion004002009002027014004009002002008002004029002015013017006002012002031033002013006007008014029072011018024002019049062029014012006016002033001057009078004002010031004
FEATURE [Part::Cylinder] Cylinder1492222  label="Cylinder"
  Angle = 360
  AttacherType = Attacher::AttachEngine3D
  FirstAngle = 0
  Height = 64
  Placement = pos=(260,-32,78) rot=(-1,0,0;1.5708rad)
  Radius = 1.25
  SecondAngle = 0
FEATURE [Part::Cylinder] Cylinder1492223  label="Cylinder"
  Angle = 360
  AttacherType = Attacher::AttachEngine3D
  FirstAngle = 0
  Height = 40
  Placement = pos=(266,16,68) rot=(-1,0,0;1.5708rad)
  Radius = 1.5
  SecondAngle = 0
FEATURE [Part::Cylinder] Cylinder1492224  label="Cylinder"
  Angle = 360
  AttacherType = Attacher::AttachEngine3D
  FirstAngle = 0
  Height = 40
  Placement = pos=(254,16,56) rot=(-1,0,0;1.5708rad)
  Radius = 1.5
  SecondAngle = 0
FEATURE [Part::Cylinder] Cylinder1492225  label="Cylinder"
  Angle = 360
  AttacherType = Attacher::AttachEngine3D
  FirstAngle = 0
  Height = 8.5
  Placement = pos=(276,16,62) rot=(-1,0,0;1.5708rad)
  Radius = 1.25
  SecondAngle = 0
FEATURE [Part::Cylinder] Cylinder1492226  label="Cylinder"
  Angle = 360
  AttacherType = Attacher::AttachEngine3D
  FirstAngle = 0
  Height = 8.5
  Placement = pos=(244,16,62) rot=(-1,0,0;1.5708rad)
  Radius = 1.25
  SecondAngle = 0
FEATURE [Part::Cylinder] Cylinder1492227  label="Cylinder"
  Angle = 360
  AttacherType = Attacher::AttachEngine3D
  FirstAngle = 0
  Height = 8.5
  Placement = pos=(260,16,46) rot=(-1,0,0;1.5708rad)
  Radius = 1.25
  SecondAngle = 0
FEATURE [Part::Cylinder] Cylinder1492228  label="Cylinder"
  Angle = 360
  AttacherType = Attacher::AttachEngine3D
  FirstAngle = 0
  Height = 40
  Placement = pos=(266,16,56) rot=(-1,0,0;1.5708rad)
  Radius = 1.5
  SecondAngle = 0
FEATURE [Part::Cylinder] Cylinder1492229  label="Cylinder"
  Angle = 360
  AttacherType = Attacher::AttachEngine3D
  FirstAngle = 0
  Height = 40
  Placement = pos=(254,16,68) rot=(-1,0,0;1.5708rad)
  Radius = 1.5
  SecondAngle = 0
FEATURE [Part::MultiFuse] Fusion004002009002027014004009002002008002004029002015013017006002012002031033002013006007008014029072011018024002019049062029014012006016002033001057009078004002010031005  label="Fusion"
  Refine = true
  Shapes = -> [Cylinder1492223,Cylinder1492224,Cylinder1492228,Cylinder1492229]
FEATURE [Part::MultiFuse] Fusion004002009002027014004009002002008002004029002015013017006002012002031033002013006007008014029072011018024002019049062029014012006016002033001057009078004002010031006  label="Fusion"
  Refine = true
  Shapes = -> [Cylinder1492225,Cylinder1492226,Cylinder1492227]
FEATURE [Part::MultiFuse] Fusion004002009002027014004009002002008002004029002015013017006002012002031033002013006007008014029072011018024002019049062029014012006016002033001057009078004002010031007  label="Fusion"
  Refine = true
  Shapes = -> [Fusion004002009002027014004009002002008002004029002015013017006002012002031033002013006007008014029072011018024002019049062029014012006016002033001057009078004002010031005,Fusion004002009002027014004009002002008002004029002015013017006002012002031033002013006007008014029072011018024002019049062029014012006016002033001057009078004002010031006]
FEATURE [Part::MultiFuse] Fusion004002009002027014004009002002008002004029002015013017006002012002031033002013006007008014029072011018024002019049062029014012006016002033001057009078004002010031008  label="front-axle-left-screws"
  Refine = true
  Shapes = -> [Fusion004002009002027014004009002002008002004029002015013017006002012002031033002013006007008014029072011018024002019049062029014012006016002033001057009078004002010031007,Cylinder1492222]
FEATURE [Part::Feature] Part__Mirroring007002003002018002002002005004004002003004003004  label="diff_front_gear_right"
  shape: bbox 38.98 x 8 x 39.03 mm, 448 faces (baked)
FEATURE [Part::Cylinder] Cylinder1492230  label="Cylinder"
  Angle = 360
  AttacherType = Attacher::AttachEngine3D
  FirstAngle = 0
  Height = 64
  Placement = pos=(260,-32,78) rot=(-1,0,0;1.5708rad)
  Radius = 1.25
  SecondAngle = 0
FEATURE [Part::Feature] Part__Mirroring007002003002018002002002005004004002003004003003002  label="front-axle-right"
  shape: bbox 38 x 40.5 x 39 mm, 75 faces (baked)
FEATURE [Part::Cylinder] Cylinder1492231  label="Cylinder"
  Angle = 360
  AttacherType = Attacher::AttachEngine3D
  FirstAngle = 0
  Height = 42
  Placement = pos=(211,-21,82) rot=(-1,0,0;1.5708rad)
  Radius = 1.5
  SecondAngle = 0
FEATURE [Part::Cylinder] Cylinder1492232  label="Cylinder"
  Angle = 360
  AttacherType = Attacher::AttachEngine3D
  FirstAngle = 0
  Height = 42
  Placement = pos=(211,-21,43) rot=(-1,0,0;1.5708rad)
  Radius = 1.5
  SecondAngle = 0
FEATURE [Part::Cylinder] Cylinder1492233  label="Cylinder"
  Angle = 360
  AttacherType = Attacher::AttachEngine3D
  FirstAngle = 0
  Height = 42
  Placement = pos=(211,-21,66) rot=(-1,0,0;1.5708rad)
  Radius = 1.5
  SecondAngle = 0
FEATURE [Part::MultiFuse] Fusion004002009002027014004009002002008002004029002015013017006002012002031033002013006007008014029072011018024002019049062029014012006016002033001057009078004002010031011  label="Fusion"
  Refine = true
  Shapes = -> [Cylinder1492231,Cylinder1492232,Cylinder1492172,Cylinder1492171,Cylinder1492170,Cylinder1492169,Cylinder1492233]
FEATURE [Part::Cylinder] Cylinder1492240  label="Cylinder"
  Angle = 360
  AttacherType = Attacher::AttachEngine3D
  FirstAngle = 0
  Height = 64
  Placement = pos=(226,-32,78) rot=(-1,0,0;1.5708rad)
  Radius = 1.25
  SecondAngle = 0
FEATURE [Part::Box] Box763  label="Cube"
  AttacherType = Attacher::AttachEngine3D
  Height = 12
  Length = 20
  Placement = pos=(250,21,70) rot=(0,0,1;0rad)
  Width = 6
FEATURE [Part::Fillet] Fillet125007020032050
  Base = -> Box763
  Edges = 2 edges r=8: [Edge2,Edge6]
  Placement = pos=(-34,0,0) rot=(0,0,1;0rad)
FEATURE [Part::Box] Box764  label="Cube"
  AttacherType = Attacher::AttachEngine3D
  Height = 8
  Length = 32
  Placement = pos=(210,21,70) rot=(0,0,1;0rad)
  Width = 3.5
FEATURE [Part::Fillet] Fillet125007020032051
  Base = -> Box764
  Edges = 4 edges r=3: [Edge2,Edge4,Edge6,Edge8]
FEATURE [Part::Cylinder] Cylinder1492241  label="Cylinder"
  Angle = 360
  AttacherType = Attacher::AttachEngine3D
  FirstAngle = 0
  Height = 64
  Placement = pos=(213,-32,74) rot=(-1,0,0;1.5708rad)
  Radius = 1.25
  SecondAngle = 0
FEATURE [Part::Cylinder] Cylinder1492242  label="Cylinder"
  Angle = 360
  AttacherType = Attacher::AttachEngine3D
  FirstAngle = 0
  Height = 64
  Placement = pos=(239,-32,74) rot=(-1,0,0;1.5708rad)
  Radius = 1.25
  SecondAngle = 0
FEATURE [Part::MultiFuse] Fusion004002009002027014004009002002008002004029002015013017006002012002031033002013006007008014029072011018024002019049062029014012006016002033001057009078004002010031013  label="Fusion"
  Refine = true
  Shapes = -> [Cylinder1492240,Cylinder1492241,Cylinder1492242,Cylinder1492230]
FEATURE [Part::Cylinder] Cylinder1492243  label="Cylinder"
  Angle = 360
  AttacherType = Attacher::AttachEngine3D
  FirstAngle = 0
  Height = 64
  Placement = pos=(226,-32,78) rot=(-1,0,0;1.5708rad)
  Radius = 1.5
  SecondAngle = 0
FEATURE [Part::Cylinder] Cylinder1492244  label="Cylinder"
  Angle = 360
  AttacherType = Attacher::AttachEngine3D
  FirstAngle = 0
  Height = 64
  Placement = pos=(213,-32,74) rot=(-1,0,0;1.5708rad)
  Radius = 1.5
  SecondAngle = 0
FEATURE [Part::Cylinder] Cylinder1492245  label="Cylinder"
  Angle = 360
  AttacherType = Attacher::AttachEngine3D
  FirstAngle = 0
  Height = 64
  Placement = pos=(239,-32,74) rot=(-1,0,0;1.5708rad)
  Radius = 1.5
  SecondAngle = 0
FEATURE [Part::MultiFuse] Fusion004002009002027014004009002002008002004029002015013017006002012002031033002013006007008014029072011018024002019049062029014012006016002033001057009078004002010031014  label="Fusion"
  Refine = true
  Shapes = -> [Cylinder1492243,Cylinder1492244,Cylinder1492245]
FEATURE [Part::MultiFuse] Fusion004002009002027014004009002002008002004029002015013017006002012002031033002013006007008014029072011018024002019049062029014012006016002033001057009078004002010031015  label="Fusion"
  Refine = true
  Shapes = -> [Fillet125007020032050,Fillet125007020032051]
FEATURE [Part::Cut] Cut176013009033007019019008010045003002004008006021005004004004004002012033009016002012007022024053  label="diff-front-side-spacer-left"
  Base = -> Fusion004002009002027014004009002002008002004029002015013017006002012002031033002013006007008014029072011018024002019049062029014012006016002033001057009078004002010031015
  Refine = true
  Tool = -> Fusion004002009002027014004009002002008002004029002015013017006002012002031033002013006007008014029072011018024002019049062029014012006016002033001057009078004002010031014
FEATURE [Part::Cylinder] Cylinder1492246  label="Cylinder"
  Angle = 360
  AttacherType = Attacher::AttachEngine3D
  FirstAngle = 0
  Height = 46
  Placement = pos=(229,-23,55) rot=(-1,0,0;1.5708rad)
  Radius = 3
  SecondAngle = 0
FEATURE [Part::Cylinder] Cylinder1492247  label="Cylinder"
  Angle = 360
  AttacherType = Attacher::AttachEngine3D
  FirstAngle = 0
  Height = 3.4
  Placement = pos=(229,-19.2,55) rot=(-1,0,0;1.5708rad)
  Radius = 4.5
  SecondAngle = 0
FEATURE [Part::Cylinder] Cylinder1492248  label="Cylinder"
  Angle = 360
  AttacherType = Attacher::AttachEngine3D
  FirstAngle = 0
  Height = 3.2
  Placement = pos=(229,-22.2,55) rot=(-1,0,0;1.5708rad)
  Radius = 4.5
  SecondAngle = 0
FEATURE [Part::Cylinder] Cylinder1492249  label="Cylinder"
  Angle = 360
  AttacherType = Attacher::AttachEngine3D
  FirstAngle = 0
  Height = 3.4
  Placement = pos=(229,15.8,55) rot=(-1,0,0;1.5708rad)
  Radius = 4.5
  SecondAngle = 0
FEATURE [Part::Cylinder] Cylinder1492250  label="Cylinder"
  Angle = 360
  AttacherType = Attacher::AttachEngine3D
  FirstAngle = 0
  Height = 3.2
  Placement = pos=(229,19,55) rot=(-1,0,0;1.5708rad)
  Radius = 4.5
  SecondAngle = 0
FEATURE [Part::MultiFuse] Fusion004002009002027014004009002002008002004029002015013017006002012002031033002013006007008014029072011018024002019049062029014012006016002033001057009078004002010031016  label="front-axle-diff-carving"
  Refine = true
  Shapes = -> [Cylinder1492246,Cylinder1492247,Cylinder1492248,Cylinder1492249,Cylinder1492250]
FEATURE [Part::MultiFuse] Fusion004002009002027014004009002002008002004029002015013017006002012002031033002013006007008014029072011018024002019049062029014012006016002033001057009078004002010031017  label="Fusion"
  Refine = true
  Shapes = -> [Fusion004002009002027014004009002002008002004029002015013017006002012002031033002013006007008014029072011018024002019049062029014012006016002033001057009078004002010026,Fusion004002009002027014004009002002008002004029002015013017006002012002031033002013006007008014029072011018024002019049062029014012006016002033001057009078004002010031,+4 more]
FEATURE [Part::Cut] Cut176013009033007019019008010045003002004008006021005004004004004002012033009016002012007022024058  label="diff-front-side-left-ALU5mm"
  Base = -> Box328
  Refine = true
  Tool = -> Fusion004002009002027014004009002002008002004029002015013017006002012002031033002013006007008014029072011018024002019049062029014012006016002033001057009078004002010031017
FEATURE [Part::Feature] Part__Mirroring007002003002018002002002005004004002003004003003005  label="diff-front-side-spacer-right"
  shape: bbox 32 x 6 x 12 mm, 21 faces (baked)
FEATURE [Part::Cylinder] Cylinder742  label="Cylinder741"
  Angle = 360
  AttacherType = Attacher::AttachEngine3D
  FirstAngle = 0
  Height = 0.2
  Placement = pos=(75,53.5,53.4) rot=(0,0,1;0rad)
  Radius = 8
  SecondAngle = 0
FEATURE [Part::Cut] Cut176013009033007019019008010045003002004008006021005004004004004002012033009016002012007022024061  label="Cut"
  Base = -> Fillet125007020032046
  Refine = true
  Tool = -> Cylinder742
FEATURE [Part::MultiFuse] Fusion004002009002027014004009002002008002004029002015013017006002012002031033002013006007008014029072011018024002019049062029014012006016002033001057009078004002010031016002  label="Fusion"
  Refine = true
  Shapes = -> [Cylinder1492088,Cut176013009033007019019008010045003002004008006021005004004004004002012033009016002012007022024061]
FEATURE [Part::Cut] Cut176013009033007019019008010045003002004008006021005004004004004002012033009016002012007022024062  label="Cut"
  Base = -> Fusion004002009002027014004009002002008002004029002015013017006002012002031033002013006007008014029072011018024002019049062029014012006016002033001057009078004002010031016002
  Refine = true
  Tool = -> Cylinder1492089
FEATURE [Part::Cut] Cut176013009033007019019008010045003002004008006021005004004004004002012033009016002012007022024063  label="rear-axle-knukle-holder-upper-left-ALU5mm"
  Base = -> Cut176013009033007019019008010045003002004008006021005004004004004002012033009016002012007022024062
  Refine = true
  Tool = -> Fusion004002009002027014004009002002008002004029002015013017006002012002031033002013006007008014029072011018024002019049062029014012006016002033001057009060
FEATURE [App::DocumentObjectGroup] Group006  label="Knukles"
  Group = -> [Cut176013009033007019019008010045003002004002,Part__Mirroring007002003002002,Cut176013009033007019019008010045003002004008006021005004004004008,Cut176013009033007019019008010045003002004008006021005004004004004002012033009016002012007022011,Cut176013009033007019019008010045003002004008006021005004004004004002012033009016002012007022025,Part__Mirroring007002003002018002002002005004004003,+7 more]
FEATURE [Part::Cylinder] Cylinder1492252  label="Cylinder"
  Angle = 360
  AttacherType = Attacher::AttachEngine3D
  FirstAngle = 0
  Height = 10
  Placement = pos=(198,0,55) rot=(0,1,0;1.5708rad)
  Radius = 5
  SecondAngle = 0
FEATURE [Part::Cylinder] Cylinder1492253  label="Cylinder"
  Angle = 360
  AttacherType = Attacher::AttachEngine3D
  FirstAngle = 0
  Height = 50
  Placement = pos=(152,0,55) rot=(0,1,0;1.5708rad)
  Radius = 2.5
  SecondAngle = 0
FEATURE [Part::Feature] Transmission_Gear_24T_pitch214001_solid  label="Transmission_Gear_24T_pitch214001 (Solid)"
  Placement = pos=(199,0,55) rot=(0,0,1;0rad)
  shape: bbox 8 x 30.9 x 30.9 mm, 1340 faces (baked)
FEATURE [Part::Feature] Compound002005019  label="MAGOM-3WAY-DISTRIBUTOR"
  Placement = pos=(195,8,131) rot=(0,0,1;0rad)
  shape: bbox 50.16 x 44.01 x 32.87 mm, 2242 faces, 46 solids (baked)
FEATURE [Part::Box] Box003  label="battery"
  AttacherType = Attacher::AttachEngine3D
  Height = 29
  Length = 133
  Placement = pos=(24,-21.5,105) rot=(0,-1,0;0.122173rad)
  Width = 43
FEATURE [Part::Feature] _03012_302001  label="MAGOM-PUMP"
  Placement = pos=(153,78.5,50) rot=(0.57735,-0.57735,-0.57735;2.0944rad)
  shape: bbox 115.6 x 41.21 x 42.72 mm, 1315 faces, 39 solids (baked)
FEATURE [Part::Cylinder] Cylinder1492255  label="Cylinder"
  Angle = 360
  AttacherType = Attacher::AttachEngine3D
  FirstAngle = 0
  Height = 20
  Placement = pos=(77,13,50) rot=(0,0,1;0rad)
  Radius = 2
  SecondAngle = 0
FEATURE [Part::Cylinder] Cylinder1492256  label="Cylinder"
  Angle = 360
  AttacherType = Attacher::AttachEngine3D
  FirstAngle = 0
  Height = 20
  Placement = pos=(77,-13,50) rot=(0,0,1;0rad)
  Radius = 2
  SecondAngle = 0
FEATURE [Part::MultiFuse] Fusion004002009002027014004009002002008002004029002015013017006002012002031033002013006007008014029072011018024002019049062029014012006016002033001057009078004002010031016003  label="Fusion"
  Refine = true
  Shapes = -> [Cylinder1492256,Cylinder1492255]
FEATURE [Part::Cut] Cut176013009033007019019008010045003002004008006021005004004004004002012033009016002012007022024068  label="rear-axle-pump-holder-ALU5mm"
  Base = -> Cut176013009033007019019008010045003002004008006021005004004004004002012033009016002012007022024013
  Placement = pos=(148.844,-9e-15,0) rot=(0,0,1;3.14159rad)
  Refine = true
  Tool = -> Fusion004002009002027014004009002002008002004029002015013017006002012002031033002013006007008014029072011018024002019049062029014012006016002033001057009078004002010031016003
FEATURE [Part::Feature] Extrude007013  label="HEX-BAR-25mm"
  Placement = pos=(87,25,77) rot=(0,0,1;1.5708rad)
  shape: bbox 25 x 6 x 5.196 mm, 8 faces (baked)
FEATURE [Part::Feature] Extrude007014  label="HEX-BAR-25mm"
  Placement = pos=(87,-25,77) rot=(0,0,1;1.5708rad)
  shape: bbox 25 x 6 x 5.196 mm, 8 faces (baked)
FEATURE [Part::Feature] Extrude007015  label="HEX-BAR-25mm"
  Placement = pos=(87,21.5,64) rot=(0,0,1;1.5708rad)
  shape: bbox 25 x 6 x 5.196 mm, 8 faces (baked)
FEATURE [Part::Feature] Extrude007016  label="HEX-BAR-25mm"
  Placement = pos=(87,-21.5,64) rot=(0,0,1;1.5708rad)
  shape: bbox 25 x 6 x 5.196 mm, 8 faces (baked)
FEATURE [Part::MultiFuse] Fusion004002009002027014004009002002008002004029002015013017006002012002031033002013006007008014029072011018024002019049062029014012006016002033001057009078004002010031016004  label="Fusion"
  Refine = true
  Shapes = -> [Extrude007013,Extrude007014,Extrude007015,Extrude007016]
FEATURE [Part::Feature] Extrude007017  label="HEX-BAR-25mm"
  Placement = pos=(87,25,77) rot=(0,0,1;1.5708rad)
  shape: bbox 25 x 6 x 5.196 mm, 8 faces (baked)
FEATURE [Part::Feature] Extrude007018  label="HEX-BAR-25mm"
  Placement = pos=(87,-25,77) rot=(0,0,1;1.5708rad)
  shape: bbox 25 x 6 x 5.196 mm, 8 faces (baked)
FEATURE [Part::Feature] Extrude007019  label="HEX-BAR-25mm"
  Placement = pos=(87,21.5,64) rot=(0,0,1;1.5708rad)
  shape: bbox 25 x 6 x 5.196 mm, 8 faces (baked)
FEATURE [Part::Feature] Extrude007020  label="HEX-BAR-25mm"
  Placement = pos=(87,-21.5,64) rot=(0,0,1;1.5708rad)
  shape: bbox 25 x 6 x 5.196 mm, 8 faces (baked)
FEATURE [Part::Cut] Cut176013009033007019019008010045003002004008006021005004004004004002012033009016002012007022024069  label="Cut"
  Base = -> Fusion004002009002027014004009002002008002004029002015013017006002012002031033002013006007008014029072011018024002019049062029014012006016002033001057009068
  Refine = true
  Tool = -> Fusion004002009002027014004009002002008002004029002015013017006002012002031033002013006007008014029072011018024002019049062029014012006016002033001057009078004002010031016004
FEATURE [Part::Cylinder] Cylinder1492257  label="Cylinder"
  Angle = 360
  AttacherType = Attacher::AttachEngine3D
  FirstAngle = 0
  Height = 2
  Placement = pos=(62,0,46) rot=(0,1,0;1.5708rad)
  Radius = 10
  SecondAngle = 0
FEATURE [Part::MultiFuse] Fusion088026007031024007008004100051009001012006005044  label="Fusion-0001"
  Refine = true
  Shapes = -> [Cylinder942,Fillet125007020032027,Cylinder1492257]
FEATURE [Part::MultiFuse] Fusion088026007031024007008004100051009001012006005045  label="Fusion-0002"
  Refine = true
  Shapes = -> [Fusion088026007031024007008004100051009001012006005044,Cylinder943]
FEATURE [Part::Cut] Cut176013009033007019019008010045003002004008006021005004004004004002012031  label="rear-axle-base-01"
  Base = -> Fusion088026007031024007008004100051009001012006005045
  Refine = true
  Tool = -> Fusion088026007031024007008004100051009001012006005046
FEATURE [Part::Cut] Cut176013009033007019019008010045003002004008006021005004004004004002012033009  label="rear-axle-base-carved"
  Base = -> Cut176013009033007019019008010045003002004008006021005004004004004002012031
  Refine = true
  Tool = -> Fusion088026007031024007008004100051009001012006005067
FEATURE [Part::Feature] Part__Mirroring007002003002018002002002005004004002003004003003004002  label="Fusion"
  shape: bbox 25 x 60.93 x 33.12 mm, 11 faces (baked)
FEATURE [Part::MultiFuse] Fusion004002009002027014004009002002008002004029002015013017006002012002031033002013006007008014029072011018024002019049062029014012006016002033001057009078004002010031016005  label="Fusion"
  Refine = true
  Shapes = -> [Fusion004002009002027014004009002002008002004029002015013017006002012002031033002013006007008014029072011018024002019049062029014012006016002033001057009021,Part__Mirroring007002003002018002002002005004004002003004003003004002]
FEATURE [Part::Cut] Cut176013009033007019019008010045003002004008006021005004004004004002012033009016002012007022024074  label="rear-axle-oscillation-limiter-8deg"
  Base = -> Cut176013009033007019019008010045003002004008006021005004004004004002012033009016002012007022024069
  Refine = true
  Tool = -> Fusion004002009002027014004009002002008002004029002015013017006002012002031033002013006007008014029072011018024002019049062029014012006016002033001057009078004002010031016005
FEATURE [Part::Feature] Cut176013009033007019019008010045003002004008006021005004004004004002012033009016002012007022024075  label="rear-axle-base-carved"
  shape: bbox 40 x 96 x 28 mm, 143 faces (baked)
FEATURE [Part::Cut] Cut176013009033007019019008010045003002004008006021005004004004004002012033009016002012007022024076  label="Cut"
  Base = -> Cut176013009033007019019008010045003002004008006021005004004004004002012033009016002012007022024075
  Refine = true
  Tool = -> Box348
FEATURE [Part::Cut] Cut176013009033007019019008010045003002004008006021005004004004004002012033009016002012007022024077  label="rear-axle-back-side"
  Base = -> Cut176013009033007019019008010045003002004008006021005004004004004002012033009016002012007022024076
  Refine = true
  Tool = -> Fusion004002009002027014004009002002008002004029002015013017006002012002031033002013006007008014029072011018024002019049062029014012006016002033001057009004
FEATURE [Part::Box] Box767  label="Cube"
  AttacherType = Attacher::AttachEngine3D
  Height = 22
  Length = 25
  Placement = pos=(62,-32,60) rot=(0,0,1;0rad)
  Width = 7
FEATURE [Part::Box] Box768  label="Cube"
  AttacherType = Attacher::AttachEngine3D
  Height = 33
  Length = 25
  Placement = pos=(62,-20,64.5) rot=(0,0,1;0rad)
  Width = 40
FEATURE [Part::Box] Box769  label="Cube"
  AttacherType = Attacher::AttachEngine3D
  Height = 22
  Length = 25
  Placement = pos=(62,-35,60) rot=(0,0,1;0rad)
  Width = 7
FEATURE [Part::Box] Box770  label="Cube"
  AttacherType = Attacher::AttachEngine3D
  Height = 25
  Length = 25
  Placement = pos=(62,-25,57) rot=(0,0,1;0rad)
  Width = 50
FEATURE [Part::Box] Box771  label="Cube"
  AttacherType = Attacher::AttachEngine3D
  Height = 31.5
  Length = 25
  Placement = pos=(63,0,30) rot=(1,0,0;0rad)
  Width = 36
FEATURE [Part::Chamfer] Chamfer039025078004038
  Base = -> Box767
  Edges = 1 edges: [Edge9 r1=21.99 r2=6.99]
FEATURE [Part::Chamfer] Chamfer039025078004039
  Base = -> Box769
  Edges = 1 edges: [Edge11 r1=21.99 r2=6.99]
  Placement = pos=(0,60,0) rot=(0,0,1;0rad)
FEATURE [Part::Chamfer] Chamfer039025078004040
  Base = -> Box768
  Edges = 2 edges: [Edge9 r1=4 r2=3,Edge11 r1=4 r2=3]
FEATURE [Part::Cut] Cut176013009033007019019008010045003002004008006021005004004004004002012033009016002012007022024078  label="Cut"
  Base = -> Box770
  Refine = true
  Tool = -> Chamfer039025078004040
FEATURE [Part::Cylinder] Cylinder1492258  label="Cylinder"
  Angle = 360
  AttacherType = Attacher::AttachEngine3D
  FirstAngle = 0
  Height = 59
  Placement = pos=(75,0,46) rot=(-1,0,0;1.39626rad)
  Radius = 9
  SecondAngle = 0
FEATURE [Part::Feature] Extrude007021  label="HEX-BAR-25mm"
  Placement = pos=(87,25,77) rot=(0,0,1;1.5708rad)
  shape: bbox 25 x 6 x 5.196 mm, 8 faces (baked)
FEATURE [Part::Feature] Extrude007022  label="HEX-BAR-25mm"
  Placement = pos=(87,-25,77) rot=(0,0,1;1.5708rad)
  shape: bbox 25 x 6 x 5.196 mm, 8 faces (baked)
FEATURE [Part::Feature] Extrude007023  label="HEX-BAR-25mm"
  Placement = pos=(87,21.5,64) rot=(0,0,1;1.5708rad)
  shape: bbox 25 x 6 x 5.196 mm, 8 faces (baked)
FEATURE [Part::Feature] Extrude007024  label="HEX-BAR-25mm"
  Placement = pos=(87,-21.5,64) rot=(0,0,1;1.5708rad)
  shape: bbox 25 x 6 x 5.196 mm, 8 faces (baked)
FEATURE [Part::Fillet] Fillet125007020032052
  Base = -> Box771
  Edges = 2 edges r=7: [Edge10,Edge12]
  Placement = pos=(-1,-18,0) rot=(0,0,1;0rad)
FEATURE [Part::MultiFuse] Fusion004002009002027014004009002002008002004029002015013017006002012002031033002013006007008014029072011018024002019049062029014012006016002033001057009078004002010031016007  label="Fusion"
  Refine = true
  Shapes = -> [Cut176013009033007019019008010045003002004008006021005004004004004002012033009016002012007022024078,Chamfer039025078004039,Chamfer039025078004038]
FEATURE [Part::MultiFuse] Fusion004002009002027014004009002002008002004029002015013017006002012002031033002013006007008014029072011018024002019049062029014012006016002033001057009078004002010031016008  label="Fusion"
  Refine = true
  Shapes = -> [Extrude007021,Extrude007022,Extrude007023,Extrude007024]
FEATURE [Part::Cut] Cut176013009033007019019008010045003002004008006021005004004004004002012033009016002012007022024079  label="Cut"
  Base = -> Fusion004002009002027014004009002002008002004029002015013017006002012002031033002013006007008014029072011018024002019049062029014012006016002033001057009078004002010031016007
  Refine = true
  Tool = -> Fusion004002009002027014004009002002008002004029002015013017006002012002031033002013006007008014029072011018024002019049062029014012006016002033001057009078004002010031016008
FEATURE [Part::Cylinder] Cylinder1492259  label="Cylinder"
  Angle = 360
  AttacherType = Attacher::AttachEngine3D
  FirstAngle = 0
  Height = 59
  Placement = pos=(75,0,46) rot=(-1,0,0;-1.39626rad)
  Radius = 9
  SecondAngle = 0
FEATURE [Part::MultiFuse] Fusion004002009002027014004009002002008002004029002015013017006002012002031033002013006007008014029072011018024002019049062029014012006016002033001057009078004002010031016009  label="Fusion"
  Refine = true
  Shapes = -> [Cylinder1492258,Cylinder1492259,Fillet125007020032052]
FEATURE [Part::Cut] Cut176013009033007019019008010045003002004008006021005004004004004002012033009016002012007022024080  label="Cut"
  Base = -> Cut176013009033007019019008010045003002004008006021005004004004004002012033009016002012007022024079
  Refine = true
  Tool = -> Fusion004002009002027014004009002002008002004029002015013017006002012002031033002013006007008014029072011018024002019049062029014012006016002033001057009078004002010031016009
FEATURE [Part::Cylinder] Cylinder1492260  label="Cylinder"
  Angle = 360
  AttacherType = Attacher::AttachEngine3D
  FirstAngle = 0
  Height = 4
  Placement = pos=(75,-35,65) rot=(0,0,1;0rad)
  Radius = 1.5
  SecondAngle = 0
FEATURE [Part::Feature] Cut176013009033007019019008010045003002004008006021005004004004004002012033009016002012007022011001  label="rear-axle-steering-knukle-lever-ALU3mm"
  shape: bbox 15.4 x 30.5 x 3 mm, 24 faces (baked)
FEATURE [Part::MultiFuse] Fusion004002009002027014004009002002008002004029002015013017006002012002031033002013006007008014029072011018024002019049062029014012006016002033001057009078004002010031016010  label="rear-axle-steering-knukle-lever-ROTATED"
  Placement = pos=(0,-7.98782,0.698843) rot=(-1,0,0;0.174533rad)
  Refine = true
  Shapes = -> [Cut176013009033007019019008010045003002004008006021005004004004004002012033009016002012007022011001,Cylinder1492260]
FEATURE [Part::Cylinder] Cylinder1492261  label="Cylinder"
  Angle = 360
  AttacherType = Attacher::AttachEngine3D
  FirstAngle = 0
  Height = 4.5
  Placement = pos=(75,-60,65) rot=(0,0,1;0rad)
  Radius = 26.5
  SecondAngle = 0
FEATURE [Part::Cylinder] Cylinder1492262  label="Cylinder"
  Angle = 360
  AttacherType = Attacher::AttachEngine3D
  FirstAngle = 0
  Height = 3.5
  Placement = pos=(75,-60,62) rot=(0,0,1;0rad)
  Radius = 28.5
  SecondAngle = 0
FEATURE [Part::MultiFuse] Fusion004002009002027014004009002002008002004029002015013017006002012002031033002013006007008014029072011018024002019049062029014012006016002033001057009078004002010031016011  label="Fusion"
  Placement = pos=(0,-7.98782,0.698843) rot=(-1,0,0;0.174533rad)
  Refine = true
  Shapes = -> [Cylinder1492262,Cylinder1492261]
FEATURE [Part::Cut] Cut176013009033007019019008010045003002004008006021005004004004004002012033009016002012007022024081  label="rear-axle-oscillation-limiter-10deg"
  Base = -> Cut176013009033007019019008010045003002004008006021005004004004004002012033009016002012007022024080
  Refine = true
  Tool = -> Fusion004002009002027014004009002002008002004029002015013017006002012002031033002013006007008014029072011018024002019049062029014012006016002033001057009078004002010031016011
FEATURE [Part::Cylinder] Cylinder1492263  label="Cylinder"
  Angle = 360
  AttacherType = Attacher::AttachEngine3D
  FirstAngle = 0
  Height = 4.5
  Placement = pos=(229,18.5,55) rot=(-1,0,0;1.5708rad)
  Radius = 5
  SecondAngle = 0
FEATURE [Part::Cut] Cut176013009033007019019008010045003002004008006021005004004004004002012033009016002012007022024082  label="Cut"
  Base = -> Fillet125007020032049
  Refine = true
  Tool = -> Cylinder1492263
FEATURE [Part::Cut] Cut176013009033007019019008010045003002004008006021005004004004004002012033009016002012007022024083  label="diff-front-side-cap-left"
  Base = -> Cut176013009033007019019008010045003002004008006021005004004004004002012033009016002012007022024082
  Refine = true
  Tool = -> Fusion004002009002027014004009002002008002004029002015013017006002012002031033002013006007008014029072011018024002019049062029014012006016002033001057009078004002010027
FEATURE [Part::Feature] Fusion004002009002027014004009002002008002004029002015013017006002012002031033002013006007008014029072011018024002019049062029014012006016002033001057009078004002010031016012001  label="Fusion"
  shape: bbox 21.5 x 64 x 2.5 mm, 6 faces, 2 solids (baked)
FEATURE [Part::Feature] Fusion004002009002027014004009002002008002004029002015013017006002012002031033002013006007008014029072011018024002019049062029014012006016002033001057009078004002010031016012002  label="Fusion"
  shape: bbox 21.5 x 64 x 2.5 mm, 6 faces, 2 solids (baked)
FEATURE [Part::Cylinder] Cylinder1492266  label="Cylinder"
  Angle = 360
  AttacherType = Attacher::AttachEngine3D
  FirstAngle = 0
  Height = 35
  Placement = pos=(57,-24,93) rot=(0,1,0;1.5708rad)
  Radius = 1.25
  SecondAngle = 0
FEATURE [Part::Cylinder] Cylinder1492267  label="Cylinder"
  Angle = 360
  AttacherType = Attacher::AttachEngine3D
  FirstAngle = 0
  Height = 35
  Placement = pos=(57,-24,85) rot=(0,1,0;1.5708rad)
  Radius = 1.25
  SecondAngle = 0
FEATURE [Part::MultiFuse] Fusion004002009002027014004009002002008002004029002015013017006002012002031033002013006007008014029072011018024002019049062029014012006016002033001057009078004002010031016012003  label="Fusion"
  Refine = true
  Shapes = -> [Cylinder1492267,Cylinder1492266]
FEATURE [Part::Feature] Fusion004002009002027014004009002002008002004029002015013017006002012002031033002013006007008014029072011018024002019049062029014012006016002033001057009078004002010031016012003001  label="Fusion"
  Placement = pos=(0,48,0) rot=(0,0,1;0rad)
  shape: bbox 35 x 2.5 x 10.5 mm, 6 faces, 2 solids (baked)
FEATURE [Part::MultiFuse] Fusion004002009002027014004009002002008002004029002015013017006002012002031033002013006007008014029072011018024002019049062029014012006016002033001057009078004002010031016012003002  label="Fusion"
  Refine = true
  Shapes = -> [Fusion004002009002027014004009002002008002004029002015013017006002012002031033002013006007008014029072011018024002019049062029014012006016002033001057009078004002010031016012001,Fusion004002009002027014004009002002008002004029002015013017006002012002031033002013006007008014029072011018024002019049062029014012006016002033001057009078004002010031016012003]
FEATURE [Part::MultiFuse] Fusion004002009002027014004009002002008002004029002015013017006002012002031033002013006007008014029072011018024002019049062029014012006016002033001057009078004002010031016012003003  label="Fusion"
  Refine = true
  Shapes = -> [Fusion004002009002027014004009002002008002004029002015013017006002012002031033002013006007008014029072011018024002019049062029014012006016002033001057009078004002010031016012003001,Fusion004002009002027014004009002002008002004029002015013017006002012002031033002013006007008014029072011018024002019049062029014012006016002033001057009078004002010031016012002]
FEATURE [Part::Cut] Cut176013009033007019019008010045003002004008006021005004004004004002012033009016002012007022024084  label="rear-axle-attach-left-ALU6mm"
  Base = -> Box753
  Refine = true
  Tool = -> Fusion004002009002027014004009002002008002004029002015013017006002012002031033002013006007008014029072011018024002019049062029014012006016002033001057009078004002010031016012003003
FEATURE [Part::Cut] Cut176013009033007019019008010045003002004008006021005004004004004002012033009016002012007022024085  label="rear-axle-attach-right-ALU6mm"
  Base = -> Box752
  Refine = true
  Tool = -> Fusion004002009002027014004009002002008002004029002015013017006002012002031033002013006007008014029072011018024002019049062029014012006016002033001057009078004002010031016012003002
FEATURE [Part::Cylinder] Cylinder1492268  label="motor"
  Angle = 360
  AttacherType = Attacher::AttachEngine3D
  FirstAngle = 0
  Height = 60
  Placement = pos=(131.5,14,77) rot=(0,1,0;1.5708rad)
  Radius = 12.5
  SecondAngle = 0
FEATURE [Part::Cylinder] Cylinder1492269  label="motor-axle"
  Angle = 360
  AttacherType = Attacher::AttachEngine3D
  FirstAngle = 0
  Height = 53
  Placement = pos=(154.5,14,77) rot=(0,1,0;1.5708rad)
  Radius = 2
  SecondAngle = 0
FEATURE [Part::Feature] Transmission_Gear_12T_pitch214001_solid  label="Transmission_Gear_12T_pitch214"
  Placement = pos=(205,14,77) rot=(0,0,1;0rad)
  shape: bbox 10 x 16.64 x 16.64 mm, 740 faces (baked)
FEATURE [Part::MultiFuse] Fusion004002009002027014004009002002008002004029002015013017006002012002031033002013006007008014029072011018024002019049062029014012006016002033001057009078004002010031016012003004  label="GEARMOTOR"
  Placement = pos=(-0.5,-1,-5.5) rot=(0,0,1;0rad)
  Refine = true
  Shapes = -> [Cylinder1492268,Cylinder1492269,Transmission_Gear_12T_pitch214001_solid]
FEATURE [Part::Feature] Cut176013009033007019019008010045003002004008006021005004004004004002012033009016002012007022024086  label="BEARING-5x8x2.5-MR85ZZ"
  Placement = pos=(273.5,-62,25.5) rot=(0,0,1;1.5708rad)
  shape: bbox 2.5 x 8 x 8 mm, 4 faces (baked)
FEATURE [Part::Feature] Fusion004002009002027014004009002002008002004029002015013017006002012002031033002013006007008014029072011018024002019049062029014012006016002033001057009078004002010031016012003005  label="servo-EMAX_ES08MA_II"
  Placement = pos=(184,-15,86) rot=(0.57735,-0.57735,-0.57735;4.18879rad)
  shape: bbox 32 x 12 x 27.75 mm, 30 faces (baked)
FEATURE [Part::Feature] Cut176013009033007019019008010045003002004008006010017027003005053020098001031003007007002011005005004026009003002  label="BEARING-17x23x4-6703"
  Placement = pos=(264,-75,9) rot=(0,0,1;1.5708rad)
  shape: bbox 4 x 23 x 23 mm, 4 faces (baked)
FEATURE [Part::Cylinder] Cylinder1492275  label="Cylinder"
  Angle = 360
  AttacherType = Attacher::AttachEngine3D
  FirstAngle = 0
  Height = 0.2
  Placement = pos=(210,0,55) rot=(0,1,0;1.5708rad)
  Radius = 4
  SecondAngle = 0
FEATURE [Part::Cylinder] Cylinder1492276  label="Cylinder"
  Angle = 360
  AttacherType = Attacher::AttachEngine3D
  FirstAngle = 0
  Height = 2
  Placement = pos=(205,0,55) rot=(0,1,0;1.5708rad)
  Radius = 15.5
  SecondAngle = 0
FEATURE [Part::Cylinder] Cylinder1492278  label="Cylinder"
  Angle = 360
  AttacherType = Attacher::AttachEngine3D
  FirstAngle = 0
  Height = 2
  Placement = pos=(199,0,55) rot=(0,1,0;1.5708rad)
  Radius = 11
  SecondAngle = 0
FEATURE [Part::Cylinder] Cylinder1492279  label="Cylinder"
  Angle = 360
  AttacherType = Attacher::AttachEngine3D
  FirstAngle = 0
  Height = 8
  Placement = pos=(199,0,62) rot=(0,1,0;1.5708rad)
  Radius = 1
  SecondAngle = 0
FEATURE [Part::MultiFuse] Fusion004002009002027014004009002002008002004029002015013017006002012002031033002013006007008014029072011018024002019049062029014012006016002033001057009078004002010031016012003007  label="Fusion"
  Refine = true
  Shapes = -> [Cylinder1492276,Transmission_Gear_24T_pitch214001_solid]
FEATURE [Part::Cut] Cut176013009033007019019008010045003002004008006010017027003005053020098001031003007007002011005005004026009003004  label="Cut"
  Base = -> Fusion004002009002027014004009002002008002004029002015013017006002012002031033002013006007008014029072011018024002019049062029014012006016002033001057009078004002010031016012003007
  Refine = true
  Tool = -> Cylinder1492278
FEATURE [Part::Cut] Cut176013009033007019019008010045003002004008006010017027003005053020098001031003007007002011005005004026009003005  label="Cut"
  Base = -> Cut176013009033007019019008010045003002004008006010017027003005053020098001031003007007002011005005004026009003004
  Refine = true
  Tool = -> Cylinder1492252
FEATURE [Part::Cylinder] Cylinder1492280  label="Cylinder"
  Angle = 360
  AttacherType = Attacher::AttachEngine3D
  FirstAngle = 0
  Height = 8
  Placement = pos=(199,0,48) rot=(0,1,0;1.5708rad)
  Radius = 1
  SecondAngle = 0
FEATURE [Part::Cylinder] Cylinder1492281  label="Cylinder"
  Angle = 360
  AttacherType = Attacher::AttachEngine3D
  FirstAngle = 0
  Height = 8
  Placement = pos=(199,7,55) rot=(0,1,0;1.5708rad)
  Radius = 1
  SecondAngle = 0
FEATURE [Part::Cylinder] Cylinder1492282  label="Cylinder"
  Angle = 360
  AttacherType = Attacher::AttachEngine3D
  FirstAngle = 0
  Height = 8
  Placement = pos=(199,-7,55) rot=(0,1,0;1.5708rad)
  Radius = 1
  SecondAngle = 0
FEATURE [Part::Cylinder] Cylinder1492283  label="Cylinder"
  Angle = 360
  AttacherType = Attacher::AttachEngine3D
  FirstAngle = 0
  Height = 8
  Placement = pos=(199,0,55) rot=(0,1,0;1.5708rad)
  Radius = 5
  SecondAngle = 0
FEATURE [Part::Cylinder] Cylinder1492284  label="Cylinder"
  Angle = 360
  AttacherType = Attacher::AttachEngine3D
  FirstAngle = 0
  Height = 2
  Placement = pos=(199,0,55) rot=(0,1,0;1.5708rad)
  Radius = 11
  SecondAngle = 0
FEATURE [Part::Cylinder] Cylinder1492285  label="Cylinder"
  Angle = 360
  AttacherType = Attacher::AttachEngine3D
  FirstAngle = 0
  Height = 8
  Placement = pos=(191,0,55) rot=(0,1,0;1.5708rad)
  Radius = 8.5
  SecondAngle = 0
FEATURE [Part::MultiFuse] Fusion004002009002027014004009002002008002004029002015013017006002012002031033002013006007008014029072011018024002019049062029014012006016002033001057009078004002010031016012003009  label="Fusion"
  Refine = true
  Shapes = -> [Cylinder1492285,Cylinder1492283,Cylinder1492284]
FEATURE [Part::Cylinder] Cylinder1492286  label="Cylinder"
  Angle = 360
  AttacherType = Attacher::AttachEngine3D
  FirstAngle = 0
  Height = 16
  Placement = pos=(191,0,55) rot=(0,1,0;1.5708rad)
  Radius = 2.5
  SecondAngle = 0
FEATURE [Part::Cut] Cut176013009033007019019008010045003002004008006010017027003005053020098001031003007007002011005005004026009003007  label="Cut"
  Base = -> Fusion004002009002027014004009002002008002004029002015013017006002012002031033002013006007008014029072011018024002019049062029014012006016002033001057009078004002010031016012003009
  Refine = true
  Tool = -> Cylinder1492286
FEATURE [Part::Cylinder] Cylinder1492287  label="Cylinder"
  Angle = 360
  AttacherType = Attacher::AttachEngine3D
  FirstAngle = 0
  Height = 12
  Placement = pos=(204.5,0,55) rot=(0,1,0;0rad)
  Radius = 2
  SecondAngle = 0
FEATURE [Part::Cut] Cut176013009033007019019008010045003002004008006010017027003005053020098001031003007007002011005005004026009003008  label="Cut"
  Base = -> Cut176013009033007019019008010045003002004008006010017027003005053020098001031003007007002011005005004026009003007
  Refine = true
  Tool = -> Cylinder1492287
FEATURE [Part::Cylinder] Cylinder1492288  label="Cylinder"
  Angle = 360
  AttacherType = Attacher::AttachEngine3D
  FirstAngle = 0
  Height = 12
  Placement = pos=(198,0,62) rot=(0,1,0;1.5708rad)
  Radius = 0.9
  SecondAngle = 0
FEATURE [Part::Cylinder] Cylinder1492289  label="Cylinder"
  Angle = 360
  AttacherType = Attacher::AttachEngine3D
  FirstAngle = 0
  Height = 12
  Placement = pos=(198,0,48) rot=(0,1,0;1.5708rad)
  Radius = 0.9
  SecondAngle = 0
FEATURE [Part::Cylinder] Cylinder1492290  label="Cylinder"
  Angle = 360
  AttacherType = Attacher::AttachEngine3D
  FirstAngle = 0
  Height = 12
  Placement = pos=(198,7,55) rot=(0,1,0;1.5708rad)
  Radius = 0.9
  SecondAngle = 0
FEATURE [Part::Cylinder] Cylinder1492291  label="Cylinder"
  Angle = 360
  AttacherType = Attacher::AttachEngine3D
  FirstAngle = 0
  Height = 12
  Placement = pos=(198,-7,55) rot=(0,1,0;1.5708rad)
  Radius = 0.9
  SecondAngle = 0
FEATURE [Part::MultiFuse] Fusion004002009002027014004009002002008002004029002015013017006002012002031033002013006007008014029072011018024002019049062029014012006016002033001057009078004002010031016012003010  label="Fusion"
  Placement = pos=(-3,0,0) rot=(0,0,1;0rad)
  Refine = true
  Shapes = -> [Cylinder1492288,Cylinder1492289,Cylinder1492290,Cylinder1492291]
FEATURE [Part::Cone] Cone003  label="Cone"
  Angle = 360
  AttacherType = Attacher::AttachEngine3D
  Height = 1.5
  Placement = pos=(205.5,0,48) rot=(0,1,0;1.5708rad)
  Radius1 = 1
  Radius2 = 1.9
FEATURE [Part::Cone] Cone004  label="Cone"
  Angle = 360
  AttacherType = Attacher::AttachEngine3D
  Height = 1.5
  Placement = pos=(205.5,0,62) rot=(0,1,0;1.5708rad)
  Radius1 = 1
  Radius2 = 1.9
FEATURE [Part::Cone] Cone005  label="Cone"
  Angle = 360
  AttacherType = Attacher::AttachEngine3D
  Height = 1.5
  Placement = pos=(205.5,7,55) rot=(0,1,0;1.5708rad)
  Radius1 = 1
  Radius2 = 1.9
FEATURE [Part::Cone] Cone006  label="Cone"
  Angle = 360
  AttacherType = Attacher::AttachEngine3D
  Height = 1.5
  Placement = pos=(205.5,-7,55) rot=(0,1,0;1.5708rad)
  Radius1 = 1
  Radius2 = 1.9
FEATURE [Part::MultiFuse] Fusion004002009002027014004009002002008002004029002015013017006002012002031033002013006007008014029072011018024002019049062029014012006016002033001057009078004002010031016012003011  label="Fusion"
  Refine = true
  Shapes = -> [Cylinder1492279,Cylinder1492280,Cylinder1492281,Cylinder1492282,Cone003,Cone004,Cone005,Cone006]
FEATURE [Part::Cut] Cut176013009033007019019008010045003002004008006010017027003005053020098001031003007007002011005005004026009003009  label="gearbox-gear"
  Base = -> Cut176013009033007019019008010045003002004008006010017027003005053020098001031003007007002011005005004026009003005
  Refine = true
  Tool = -> Fusion004002009002027014004009002002008002004029002015013017006002012002031033002013006007008014029072011018024002019049062029014012006016002033001057009078004002010031016012003011
FEATURE [Part::Cut] Cut176013009033007019019008010045003002004008006010017027003005053020098001031003007007002011005005004026009003010  label="Cut"
  Base = -> Cut176013009033007019019008010045003002004008006010017027003005053020098001031003007007002011005005004026009003008
  Refine = true
  Tool = -> Fusion004002009002027014004009002002008002004029002015013017006002012002031033002013006007008014029072011018024002019049062029014012006016002033001057009078004002010031016012003010
FEATURE [Part::RegularPolygon] RegularPolygon002  label="Regular polygon"
  AttacherType = Attacher::AttachEngine3D
  Circumradius = 5.75
  Polygon = 6
FEATURE [Part::Cylinder] Cylinder1492292  label="Cylinder"
  Angle = 360
  AttacherType = Attacher::AttachEngine3D
  FirstAngle = 0
  Height = 3
  Radius = 5.75
  SecondAngle = 0
FEATURE [Part::Cylinder] Cylinder1492293  label="Cylinder"
  Angle = 30
  AttacherType = Attacher::AttachEngine3D
  FirstAngle = 0
  Height = 3
  Placement = pos=(0,0,0) rot=(0,0,1;0.523599rad)
  Radius = 5.75
  SecondAngle = 0
FEATURE [Part::Cylinder] Cylinder1492294  label="Cylinder"
  Angle = 30
  AttacherType = Attacher::AttachEngine3D
  FirstAngle = 0
  Height = 3
  Placement = pos=(0,0,0) rot=(0,0,1;3.66519rad)
  Radius = 5.75
  SecondAngle = 0
FEATURE [Part::MultiFuse] Fusion004002009002027014004009002002008002004029002015013017006002012002031033002013006007008014029072011018024002019049062029014012006016002033001057009078004002010031016012003012  label="Fusion"
  Refine = true
  Shapes = -> [Cylinder1492293,Cylinder1492294]
FEATURE [Part::Cut] Cut176013009033007019019008010045003002004008006010017027003005053020098001031003007007002011005005004026009003011  label="Cut"
  Base = -> Cylinder1492292
  Placement = pos=(191,0,55) rot=(0,1,0;1.5708rad)
  Refine = true
  Tool = -> Fusion004002009002027014004009002002008002004029002015013017006002012002031033002013006007008014029072011018024002019049062029014012006016002033001057009078004002010031016012003012
FEATURE [Part::Cylinder] Cylinder1492295  label="Cylinder"
  Angle = 360
  AttacherType = Attacher::AttachEngine3D
  FirstAngle = 0
  Height = 3
  Radius = 5.75
  SecondAngle = 0
FEATURE [Part::Cylinder] Cylinder1492296  label="Cylinder"
  Angle = 40
  AttacherType = Attacher::AttachEngine3D
  FirstAngle = 0
  Height = 3
  Placement = pos=(0,0,0) rot=(0,0,1;0.523599rad)
  Radius = 5.75
  SecondAngle = 0
FEATURE [Part::Cylinder] Cylinder1492297  label="Cylinder"
  Angle = 40
  AttacherType = Attacher::AttachEngine3D
  FirstAngle = 0
  Height = 3
  Placement = pos=(0,0,0) rot=(0,0,1;3.66519rad)
  Radius = 5.75
  SecondAngle = 0
FEATURE [Part::MultiFuse] Fusion004002009002027014004009002002008002004029002015013017006002012002031033002013006007008014029072011018024002019049062029014012006016002033001057009078004002010031016012003013  label="Fusion"
  Refine = true
  Shapes = -> [Cylinder1492296,Cylinder1492297]
FEATURE [Part::Cut] Cut176013009033007019019008010045003002004008006010017027003005053020098001031003007007002011005005004026009003013  label="Cut"
  Base = -> Cylinder1492295
  Placement = pos=(0,0,0) rot=(0,0,1;0.174533rad)
  Refine = true
  Tool = -> Fusion004002009002027014004009002002008002004029002015013017006002012002031033002013006007008014029072011018024002019049062029014012006016002033001057009078004002010031016012003013
FEATURE [Part::Extrusion] Extrude007025
  Base = -> RegularPolygon002
  Dir = (0,0,1)
  DirMode = 2
  FaceMakerClass = Part::FaceMakerBullseye
  LengthFwd = 11
  LengthRev = 0
  Solid = true
  Symmetric = false
FEATURE [Part::Cut] Cut176013009033007019019008010045003002004008006010017027003005053020098001031003007007002011005005004026009003014  label="Cut"
  Base = -> Extrude007025
  Refine = true
  Tool = -> Cut176013009033007019019008010045003002004008006010017027003005053020098001031003007007002011005005004026009003013
FEATURE [Part::Cylinder] Cylinder1492298  label="Cylinder"
  Angle = 360
  AttacherType = Attacher::AttachEngine3D
  FirstAngle = 0
  Height = 11
  Radius = 2.5
  SecondAngle = 0
FEATURE [Part::Cut] Cut176013009033007019019008010045003002004008006010017027003005053020098001031003007007002011005005004026009003015  label="Cut"
  Base = -> Cut176013009033007019019008010045003002004008006010017027003005053020098001031003007007002011005005004026009003014
  Placement = pos=(194,0,55) rot=(0,-1,0;1.5708rad)
  Refine = true
  Tool = -> Cylinder1492298
FEATURE [Part::Cut] Cut176013009033007019019008010045003002004008006010017027003005053020098001031003007007002011005005004026009003016  label="Cut"
  Base = -> Cut176013009033007019019008010045003002004008006010017027003005053020098001031003007007002011005005004026009003010
  Refine = true
  Tool = -> Cut176013009033007019019008010045003002004008006010017027003005053020098001031003007007002011005005004026009003011
FEATURE [Part::Cylinder] Cylinder1492299  label="Cylinder"
  Angle = 360
  AttacherType = Attacher::AttachEngine3D
  FirstAngle = 0
  Height = 3
  Placement = pos=(191,0,55) rot=(0,1,0;1.5708rad)
  Radius = 3
  SecondAngle = 0
FEATURE [Part::Cut] Cut176013009033007019019008010045003002004008006010017027003005053020098001031003007007002011005005004026009003017  label="Cut"
  Base = -> Cut176013009033007019019008010045003002004008006010017027003005053020098001031003007007002011005005004026009003016
  Refine = true
  Tool = -> Cylinder1492299
FEATURE [Part::Cylinder] Cylinder1492300  label="Cylinder"
  Angle = 360
  AttacherType = Attacher::AttachEngine3D
  FirstAngle = 0
  Height = 10
  Placement = pos=(75,-35,59) rot=(0,1,0;1.5708rad)
  Radius = 1.5
  SecondAngle = 0
FEATURE [Part::Cylinder] Cylinder1492301  label="Cylinder"
  Angle = 360
  AttacherType = Attacher::AttachEngine3D
  FirstAngle = 0
  Height = 44
  Placement = pos=(176,-17,71.5) rot=(0,-1,0;1.85878rad)
  Radius = 1.5
  SecondAngle = 0
FEATURE [Part::Cylinder] Cylinder1492302  label="Cylinder"
  Angle = 360
  AttacherType = Attacher::AttachEngine3D
  FirstAngle = 0
  Height = 53
  Placement = pos=(134,-17,59) rot=(0.171295,-0.970211,0.171313;1.60316rad)
  Radius = 1.5
  SecondAngle = 0
FEATURE [Part::MultiFuse] Fusion004002009002027014004009002002008002004029002015013017006002012002031033002013006007008014029072011018024002019049062029014012006016002033001057009078004002010031016012003014  label="steering-link-STEEL"
  Refine = true
  Shapes = -> [Cylinder1492300,Cylinder1492301,Cylinder1492302]
FEATURE [Part::Feature] Cut176013009033007019019008010045003002004008006021005004004004008001  label="rear-axle-steering-knukle-arm-right-ALU4mm"
  Placement = pos=(75,-92.5,46) rot=(0,0,1;0rad)
  shape: bbox 24.2 x 22.25 x 4 mm, 22 faces (baked)
FEATURE [Part::Feature] Cut176013009033007019019008010045003002004008006021005004004004004002012033009016002012007022011002  label="rear-axle-steering-knukle-lever-ALU3mm"
  shape: bbox 15.4 x 30.5 x 3 mm, 24 faces (baked)
FEATURE [Part::MultiFuse] Fusion004002009002027014004009002002008002004029002015013017006002012002031033002013006007008014029072011018024002019049062029014012006016002033001057009078004002010031016012003015  label="Fusion"
  Placement = pos=(-16.5343,-63.9265,0) rot=(0,0,1;0.733038rad)
  Refine = true
  Shapes = -> [Cut176013009033007019019008010045003002004008006021005004004004008001,Cut176013009033007019019008010045003002004008006021005004004004004002012033009016002012007022011002]
FEATURE [Part::Feature] Fusion004002009002027014004009002002008002004029002015013017006002012002031033002013006007008014029072011018024002019049062029014012006016002033001057009078004002010031016012003014001  label="Fusion"
  Placement = pos=(-13.5813,-8.61919,0) rot=(0,0,1;0.047997rad)
  shape: bbox 102.2 x 24.92 x 3 mm, 10 faces (baked)
FEATURE [Part::Part2DObjectPython] Line023  label="rear-axle-steering-point-right"  # Draft 2D object (typed FeaturePython)
  Closed = true
  End = (62.6,-39.75,26)
  FilletRadius = 0
  MapMode = 5
  Placement = pos=(62.6,-72.25,42) rot=(0,0,1;0rad)
  Points = (2) [(0,32.5,24),(0,32.5,-16)]
  Start = (62.6,-39.75,66)
FEATURE [Part::Feature] Fusion004002009002027014004009002002008002004029002015013017006002012002031033002013006007008014029072011018024002019049062029014012006016002033001057009078004002010031016012003015001  label="Fusion"
  Placement = pos=(48.8371,34.8332,0) rot=(0,0,-1;0.663225rad)
  shape: bbox 35.17 x 37.41 x 21 mm, 46 faces, 2 solids (baked)
FEATURE [Part::Part2DObjectPython] Line024  label="rear-axle-steering-point-right"  # Draft 2D object (typed FeaturePython)
  Closed = true
  End = (86.4,-39,26)
  FilletRadius = 0
  MapMode = 5
  Placement = pos=(86.4,-71.5,42) rot=(0,0,1;0rad)
  Points = (2) [(0,32.5,24),(0,32.5,-16)]
  Start = (86.4,-39,66)
FEATURE [Part::Feature] Fusion004002009002027014004009002002008002004029002015013017006002012002031033002013006007008014029072011018024002019049062029014012006016002033001057009078004002010031016012003015002  label="Fusion"
  Placement = pos=(10.2116,-6.90104,7e-15) rot=(0,0,1;0.038397rad)
  shape: bbox 102.4 x 23.94 x 3 mm, 10 faces (baked)
FEATURE [App::DocumentObjectGroup] Group023  label="Steering Link"
  Group = -> [Fusion004002009002027014004009002002008002004029002015013017006002012002031033002013006007008014029072011018024002019049062029014012006016002033001057009078004002010031016012003015,Fusion004002009002027014004009002002008002004029002015013017006002012002031033002013006007008014029072011018024002019049062029014012006016002033001057009078004002010031016012003014001,Line023,+3 more]
FEATURE [Part::Box] Box  label="Cube"
  AttacherType = Attacher::AttachEngine3D
  Height = 15
  Length = 39
  Placement = pos=(55,-32,82) rot=(0,0,1;0rad)
  Width = 6
FEATURE [Part::Box] Box772  label="Cube"
  AttacherType = Attacher::AttachEngine3D
  Height = 15
  Length = 35.4
  Placement = pos=(56.8,-27,82) rot=(0,0,1;0rad)
  Width = 5
FEATURE [Part::Cylinder] Cylinder1492303  label="Cylinder"
  Angle = 360
  AttacherType = Attacher::AttachEngine3D
  FirstAngle = 0
  Height = 39
  Placement = pos=(55,-24,85) rot=(0,1,0;1.5708rad)
  Radius = 3.2
  SecondAngle = 0
FEATURE [Part::Cylinder] Cylinder1492304  label="Cylinder"
  Angle = 360
  AttacherType = Attacher::AttachEngine3D
  FirstAngle = 0
  Height = 39
  Placement = pos=(55,-24,93) rot=(0,1,0;1.5708rad)
  Radius = 3.2
  SecondAngle = 0
FEATURE [Part::Cylinder] Cylinder1492265  label="Cylinder"
  Angle = 360
  AttacherType = Attacher::AttachEngine3D
  FirstAngle = 0
  Height = 66
  Placement = pos=(84,-32,89) rot=(-1,0,0;1.5708rad)
  Radius = 1.5
  SecondAngle = 0
FEATURE [Part::Cylinder] Cylinder1492264  label="Cylinder"
  Angle = 360
  AttacherType = Attacher::AttachEngine3D
  FirstAngle = 0
  Height = 66
  Placement = pos=(65,-32,89) rot=(-1,0,0;1.5708rad)
  Radius = 1.5
  SecondAngle = 0
FEATURE [Part::MultiFuse] Fusion004002009002027014004009002002008002004029002015013017006002012002031033002013006007008014029072011018024002019049062029014012006016002033001057009078004002010031016012003015003  label="Fusion"
  Refine = true
  Shapes = -> [Cylinder1492303,Cylinder1492304,Cylinder1492265,Cylinder1492264]
FEATURE [Part::Cut] Cut176013009033007019019008010045003002004008006010017027003005053020098001031003007007002011005005004026009004013003  label="Cut"
  Base = -> Box
  Refine = true
  Tool = -> Box772
FEATURE [Part::Cut] Cut176013009033007019019008010045003002004008006010017027003005053020098001031003007007002011005005004026009004013004  label="rear-axle-attach-TOOL"
  Base = -> Cut176013009033007019019008010045003002004008006010017027003005053020098001031003007007002011005005004026009004013003
  Refine = true
  Tool = -> Fusion004002009002027014004009002002008002004029002015013017006002012002031033002013006007008014029072011018024002019049062029014012006016002033001057009078004002010031016012003015003
FEATURE [Part::Feature] Part__Mirroring007002003002018002002002005004004002003004003003004004  label="diff-front-side-cap-right"
  shape: bbox 23.81 x 3 x 23.81 mm, 10 faces (baked)
FEATURE [Part::Feature] Part__Mirroring007002003002018002002002005004004002003004003003004005  label="diff_rear_gear_right"
  shape: bbox 29.48 x 8 x 29.55 mm, 336 faces (baked)
FEATURE [Part::Feature] Compound003003  label="servo-DS_3218MG"
  Placement = pos=(176,-26,96) rot=(0.707107,0,-0.707107;3.14159rad)
  shape: bbox 55.85 x 47.54 x 38.43 mm, 2500 faces, 12 solids (baked)
FEATURE [Part::Feature] Part__Mirroring007002003002018002002002005004004002003004003003004003002  label="diff-front-side-right-ALU5mm"
  shape: bbox 75 x 5 x 51 mm, 32 faces (baked)
FEATURE [Part::Box] Box377  label="Cube"
  AttacherType = Attacher::AttachEngine3D
  Height = 51
  Length = 8
  Placement = pos=(207,-16,35) rot=(0,0,1;0rad)
  Width = 32
FEATURE [Part::Box] Box761  label="Cube"
  AttacherType = Attacher::AttachEngine3D
  Height = 16
  Length = 1.5
  Placement = pos=(213,-16.25,47) rot=(0,0,1;0rad)
  Width = 10
FEATURE [Part::Box] Box762  label="Cube"
  AttacherType = Attacher::AttachEngine3D
  Height = 16
  Length = 1.5
  Placement = pos=(213,6.25,47) rot=(0,0,1;0rad)
  Width = 10
FEATURE [Part::Cylinder] Cylinder1492202  label="Cylinder"
  Angle = 360
  AttacherType = Attacher::AttachEngine3D
  FirstAngle = 0
  Height = 15.5
  Placement = pos=(199,0,55) rot=(0,1,0;1.5708rad)
  Radius = 3
  SecondAngle = 0
FEATURE [Part::Cylinder] Cylinder1492203  label="Cylinder"
  Angle = 360
  AttacherType = Attacher::AttachEngine3D
  FirstAngle = 0
  Height = 3.1
  Placement = pos=(211.4,0,55) rot=(0,1,0;1.5708rad)
  Radius = 4.6
  SecondAngle = 0
FEATURE [Part::Cylinder] Cylinder1492204  label="Cylinder"
  Angle = 360
  AttacherType = Attacher::AttachEngine3D
  FirstAngle = 0
  Height = 3.1
  Placement = pos=(206.4,0,55) rot=(0,1,0;1.5708rad)
  Radius = 4.6
  SecondAngle = 0
FEATURE [Part::Cylinder] Cylinder1492234  label="Cylinder"
  Angle = 360
  AttacherType = Attacher::AttachEngine3D
  FirstAngle = 0
  Height = 16
  Placement = pos=(211,-21,66) rot=(-1,0,0;1.5708rad)
  Radius = 1.25
  SecondAngle = 0
FEATURE [Part::Cylinder] Cylinder1492235  label="Cylinder"
  Angle = 360
  AttacherType = Attacher::AttachEngine3D
  FirstAngle = 0
  Height = 16
  Placement = pos=(211,-21,43) rot=(-1,0,0;1.5708rad)
  Radius = 1.25
  SecondAngle = 0
FEATURE [Part::Cylinder] Cylinder1492236  label="Cylinder"
  Angle = 360
  AttacherType = Attacher::AttachEngine3D
  FirstAngle = 0
  Height = 16
  Placement = pos=(211,-21,82) rot=(-1,0,0;1.5708rad)
  Radius = 1.25
  SecondAngle = 0
FEATURE [Part::Cylinder] Cylinder1492237  label="Cylinder"
  Angle = 360
  AttacherType = Attacher::AttachEngine3D
  FirstAngle = 0
  Height = 16
  Placement = pos=(211,5,66) rot=(-1,0,0;1.5708rad)
  Radius = 1.25
  SecondAngle = 0
FEATURE [Part::Cylinder] Cylinder1492238  label="Cylinder"
  Angle = 360
  AttacherType = Attacher::AttachEngine3D
  FirstAngle = 0
  Height = 16
  Placement = pos=(211,5,43) rot=(-1,0,0;1.5708rad)
  Radius = 1.25
  SecondAngle = 0
FEATURE [Part::Cylinder] Cylinder1492239  label="Cylinder"
  Angle = 360
  AttacherType = Attacher::AttachEngine3D
  FirstAngle = 0
  Height = 16
  Placement = pos=(211,5,82) rot=(-1,0,0;1.5708rad)
  Radius = 1.25
  SecondAngle = 0
FEATURE [Part::Cylinder] Cylinder1492270  label="Cylinder"
  Angle = 360
  AttacherType = Attacher::AttachEngine3D
  FirstAngle = 0
  Height = 10
  Placement = pos=(206,11.5,40) rot=(0,1,0;1.5708rad)
  Radius = 1.25
  SecondAngle = 0
FEATURE [Part::Cylinder] Cylinder1492272  label="Cylinder"
  Angle = 360
  AttacherType = Attacher::AttachEngine3D
  FirstAngle = 0
  Height = 10
  Placement = pos=(206,-11.5,40) rot=(0,1,0;1.5708rad)
  Radius = 1.25
  SecondAngle = 0
FEATURE [Part::Cylinder] Cylinder1492273  label="Cylinder"
  Angle = 360
  AttacherType = Attacher::AttachEngine3D
  FirstAngle = 0
  Height = 10
  Placement = pos=(206,-3,76) rot=(0,1,0;1.5708rad)
  Radius = 1.25
  SecondAngle = 0
FEATURE [Part::MultiFuse] Fusion004002009002027014004009002002008002004029002015013017006002012002031033002013006007008014029072011018024002019049062029014012006016002033001057009078004002010025  label="Fusion"
  Placement = pos=(0.5,0,0) rot=(0,0,1;0rad)
  Refine = true
  Shapes = -> [Cylinder1492202,Cylinder1492203,Cylinder1492204]
FEATURE [Part::Cut] Cut176013009033007019019008010045003002004008006021005004004004004002012033009016002012007022024055  label="Cut"
  Base = -> Box377
  Refine = true
  Tool = -> Fusion004002009002027014004009002002008002004029002015013017006002012002031033002013006007008014029072011018024002019049062029014012006016002033001057009078004002010025
FEATURE [Part::MultiFuse] Fusion004002009002027014004009002002008002004029002015013017006002012002031033002013006007008014029072011018024002019049062029014012006016002033001057009078004002010031010  label="Fusion"
  Placement = pos=(0.5,0,0) rot=(0,0,1;0rad)
  Refine = true
  Shapes = -> [Box762,Box761]
FEATURE [Part::Cut] Cut176013009033007019019008010045003002004008006021005004004004004002012033009016002012007022024056  label="Cut"
  Base = -> Cut176013009033007019019008010045003002004008006021005004004004004002012033009016002012007022024055
  Refine = true
  Tool = -> Fusion004002009002027014004009002002008002004029002015013017006002012002031033002013006007008014029072011018024002019049062029014012006016002033001057009078004002010031010
FEATURE [Part::MultiFuse] Fusion004002009002027014004009002002008002004029002015013017006002012002031033002013006007008014029072011018024002019049062029014012006016002033001057009078004002010031012  label="Fusion"
  Refine = true
  Shapes = -> [Cylinder1492234,Cylinder1492235,Cylinder1492236,Cylinder1492237,Cylinder1492238,Cylinder1492239]
FEATURE [Part::Cut] Cut176013009033007019019008010045003002004008006021005004004004004002012033009016002012007022024057  label="Cut"
  Base = -> Cut176013009033007019019008010045003002004008006021005004004004004002012033009016002012007022024056
  Refine = true
  Tool = -> Fusion004002009002027014004009002002008002004029002015013017006002012002031033002013006007008014029072011018024002019049062029014012006016002033001057009078004002010031012
FEATURE [Part::MultiFuse] Fusion004002009002027014004009002002008002004029002015013017006002012002031033002013006007008014029072011018024002019049062029014012006016002033001057009078004002010031016012003006  label="Fusion"
  Refine = true
  Shapes = -> [Cylinder1492270,Cylinder1492272,Cylinder1492273]
FEATURE [Part::Cut] Cut176013009033007019019008010045003002004008006010017027003005053020098001031003007007002011005005004026009003003  label="Cut"
  Base = -> Cut176013009033007019019008010045003002004008006021005004004004004002012033009016002012007022024057
  Refine = true
  Tool = -> Fusion004002009002027014004009002002008002004029002015013017006002012002031033002013006007008014029072011018024002019049062029014012006016002033001057009078004002010031016012003006
FEATURE [Part::RegularPolygon] RegularPolygon004  label="Regular polygon"
  AttacherType = Attacher::AttachEngine3D
  Circumradius = 3.2
  Placement = pos=(0,0,0) rot=(0,1,0;1.5708rad)
  Polygon = 6
FEATURE [Part::Extrusion] Extrude008020
  Base = -> RegularPolygon004
  Dir = (1,0,2e-16)
  DirMode = 2
  FaceMakerClass = Part::FaceMakerBullseye
  LengthFwd = 2.5
  LengthRev = 0
  Placement = pos=(212.5,-11.5,40) rot=(0,0,1;0rad)
  Solid = true
  Symmetric = false
FEATURE [Part::RegularPolygon] RegularPolygon005  label="Regular polygon"
  AttacherType = Attacher::AttachEngine3D
  Circumradius = 3.2
  Placement = pos=(0,0,0) rot=(0,1,0;1.5708rad)
  Polygon = 6
FEATURE [Part::Extrusion] Extrude007020002
  Base = -> RegularPolygon005
  Dir = (1,0,2e-16)
  DirMode = 2
  FaceMakerClass = Part::FaceMakerBullseye
  LengthFwd = 2.5
  LengthRev = 0
  Placement = pos=(212.5,-3,76) rot=(0,0,1;0rad)
  Solid = true
  Symmetric = false
FEATURE [Part::RegularPolygon] RegularPolygon006  label="Regular polygon"
  AttacherType = Attacher::AttachEngine3D
  Circumradius = 3.2
  Placement = pos=(0,0,0) rot=(0,1,0;1.5708rad)
  Polygon = 6
FEATURE [Part::Extrusion] Extrude007020003
  Base = -> RegularPolygon006
  Dir = (1,0,2e-16)
  DirMode = 2
  FaceMakerClass = Part::FaceMakerBullseye
  LengthFwd = 2.5
  LengthRev = 0
  Placement = pos=(212.5,11.5,40) rot=(0,0,1;0rad)
  Solid = true
  Symmetric = false
FEATURE [Part::MultiFuse] Fusion004002009002027014004009002002008002004029002015013017006002012002031033002013006007008014029072011018024002019049062029014012006016002033001057009078004002010031016012003004006002003003002005024  label="Fusion"
  Refine = true
  Shapes = -> [Extrude007020003,Extrude008020,Extrude007020002]
FEATURE [Part::Cut] Cut176013009033007019019008010045003002004008006010017027003005053020098001031003007007002011005005004026009004013005002003006005  label="diff-back-side"
  Base = -> Cut176013009033007019019008010045003002004008006010017027003005053020098001031003007007002011005005004026009003003
  Refine = true
  Tool = -> Fusion004002009002027014004009002002008002004029002015013017006002012002031033002013006007008014029072011018024002019049062029014012006016002033001057009078004002010031016012003004006002003003002005024
FEATURE [Part::Cylinder] Cylinder1492305  label="Cylinder"
  Angle = 360
  AttacherType = Attacher::AttachEngine3D
  FirstAngle = 0
  Height = 3.5
  Radius = 2.5
  SecondAngle = 0
FEATURE [Part::Cylinder] Cylinder1492306  label="Cylinder"
  Angle = 360
  AttacherType = Attacher::AttachEngine3D
  FirstAngle = 0
  Height = 3.5
  Radius = 4.75
  SecondAngle = 0
FEATURE [Part::Cut] Cut176013009033007019019008010045003002004008006010017027003005053020098001031003007007002011005005004026009004013005002003006006  label="Cut"
  Base = -> Cylinder1492306
  Refine = true
  Tool = -> Cylinder1492305
FEATURE [Part::Cylinder] Cylinder1492307  label="Cylinder"
  Angle = 360
  AttacherType = Attacher::AttachEngine3D
  FirstAngle = 0
  Height = 11.75
  Placement = pos=(3,0,1.75) rot=(0,1,0;1.5708rad)
  Radius = 3.2
  SecondAngle = 0
FEATURE [Part::Chamfer] Chamfer039025078004041
  Base = -> Cylinder1492307
  Edges = 1 edges r=1: [Edge2]
FEATURE [Part::MultiFuse] Fusion004002009002027014004009002002008002004029002015013017006002012002031033002013006007008014029072011018024002019049062029014012006016002033001057009078004002010031016012003004006002003003002005025  label="BALL-JOINT"
  Refine = true
  Shapes = -> [Chamfer039025078004041,Cut176013009033007019019008010045003002004008006010017027003005053020098001031003007007002011005005004026009004013005002003006006]
FEATURE [Part::Feature] Fusion004002009002027014004009002002008002004029002015013017006002012002031033002013006007008014029072011018024002019049062029014012006016002033001057009078004002010031016012003004006002003003002005025001  label="BALL-JOINT"
  Placement = pos=(75,-35,57) rot=(0,0,1;0rad)
  shape: bbox 19.5 x 9.5 x 6.4 mm, 9 faces (baked)
FEATURE [App::DocumentObjectGroup] Group005  label="Bearings&Hex bars"
  Group = -> [Cut176013009033007019019008010045003002004008006021005004004004004002012033009016002012007009,Cut176013009033007019019008010045003002004008006021005004003,Cut176013009033007019019008010045003002004008006021005004004004004002004,Cut176013009033007019019008010045003002004008006021005004004004004002005,Cut176013009033007019019008010045003002004008006021005004004004004002006,+12 more]
FEATURE [Part::Feature] Cut176013009033007019019008010045003002004008006010017027003005053020098001031003007007002011005005004026009004013005002003006024016  label="frame-right_ALU5mm"
  shape: bbox 293 x 5 x 130 mm, 37 faces (baked)
FEATURE [Part::Feature] Cut176013009033007019019008010045003002004008006010017027003005053020098001031003007007002011005005004026009004013005002003006024015001  label="frame-left_ALU5mm"
  Placement = pos=(0,59,0) rot=(0,0,1;0rad)
  shape: bbox 293 x 5 x 130 mm, 37 faces (baked)
FEATURE [App::DocumentObjectGroup] Group008  label="Frame"
  Group = -> [_03012_302001,Compound002005019,Box003,Fusion004002009002027014004009002002008002004029002015013017006002012002031033002013006007008014029072011018024002019049062029014012006016002033001057009078004002010031016012003005,Compound003003,Cut176013009033007019019008010045003002004008006010017027003005053020098001031003007007002011005005004026009004013005002003006024016,+1 more]
FEATURE [Part::Box] Box773  label="Cube"
  AttacherType = Attacher::AttachEngine3D
  Height = 22
  Length = 25
  Placement = pos=(62,-32,60) rot=(0,0,1;0rad)
  Width = 7
FEATURE [Part::Box] Box774  label="Cube"
  AttacherType = Attacher::AttachEngine3D
  Height = 33
  Length = 25
  Placement = pos=(62,-20,64.5) rot=(0,0,1;0rad)
  Width = 40
FEATURE [Part::Box] Box775  label="Cube"
  AttacherType = Attacher::AttachEngine3D
  Height = 22
  Length = 25
  Placement = pos=(62,-35,60) rot=(0,0,1;0rad)
  Width = 7
FEATURE [Part::Box] Box776  label="Cube"
  AttacherType = Attacher::AttachEngine3D
  Height = 25
  Length = 25
  Placement = pos=(62,-25,57) rot=(0,0,1;0rad)
  Width = 50
FEATURE [Part::Box] Box777  label="Cube"
  AttacherType = Attacher::AttachEngine3D
  Height = 31.5
  Length = 25
  Placement = pos=(63,0,30) rot=(1,0,0;0rad)
  Width = 36
FEATURE [Part::Chamfer] Chamfer039025078004042
  Base = -> Box773
  Edges = 1 edges: [Edge9 r1=21.99 r2=6.99]
FEATURE [Part::Chamfer] Chamfer039025078004043
  Base = -> Box775
  Edges = 1 edges: [Edge11 r1=21.99 r2=6.99]
  Placement = pos=(0,60,0) rot=(0,0,1;0rad)
FEATURE [Part::Chamfer] Chamfer039025078004044
  Base = -> Box774
  Edges = 2 edges: [Edge9 r1=4 r2=3,Edge11 r1=4 r2=3]
FEATURE [Part::Cut] Cut176013009033007019019008010045003002004008006010017027003005053020098001031003007007002011005005004026009004013005002003006024015002  label="Cut"
  Base = -> Box776
  Refine = true
  Tool = -> Chamfer039025078004044
FEATURE [Part::Cylinder] Cylinder1492308  label="Cylinder"
  Angle = 360
  AttacherType = Attacher::AttachEngine3D
  FirstAngle = 0
  Height = 59
  Placement = pos=(75,0,46) rot=(-1,0,0;1.39626rad)
  Radius = 9
  SecondAngle = 0
FEATURE [Part::Cylinder] Cylinder1492309  label="Cylinder"
  Angle = 360
  AttacherType = Attacher::AttachEngine3D
  FirstAngle = 0
  Height = 59
  Placement = pos=(75,0,46) rot=(-1,0,0;-1.39626rad)
  Radius = 9
  SecondAngle = 0
FEATURE [Part::Feature] Extrude007020004  label="HEX-BAR-25mm"
  Placement = pos=(87,25,77) rot=(0,0,1;1.5708rad)
  shape: bbox 25 x 6 x 5.196 mm, 8 faces (baked)
FEATURE [Part::Feature] Extrude007020005  label="HEX-BAR-25mm"
  Placement = pos=(87,-25,77) rot=(0,0,1;1.5708rad)
  shape: bbox 25 x 6 x 5.196 mm, 8 faces (baked)
FEATURE [Part::Feature] Extrude007020006  label="HEX-BAR-25mm"
  Placement = pos=(87,21.5,64) rot=(0,0,1;1.5708rad)
  shape: bbox 25 x 6 x 5.196 mm, 8 faces (baked)
FEATURE [Part::Feature] Extrude007020007  label="HEX-BAR-25mm"
  Placement = pos=(87,-21.5,64) rot=(0,0,1;1.5708rad)
  shape: bbox 25 x 6 x 5.196 mm, 8 faces (baked)
FEATURE [Part::Fillet] Fillet125007020032053
  Base = -> Box777
  Edges = 2 edges r=7: [Edge10,Edge12]
  Placement = pos=(-1,-18,0) rot=(0,0,1;0rad)
FEATURE [Part::MultiFuse] Fusion004002009002027014004009002002008002004029002015013017006002012002031033002013006007008014029072011018024002019049062029014012006016002033001057009078004002010031016012003004006002003003002005025002  label="Fusion"
  Refine = true
  Shapes = -> [Cut176013009033007019019008010045003002004008006010017027003005053020098001031003007007002011005005004026009004013005002003006024015002,Chamfer039025078004043,Chamfer039025078004042]
FEATURE [Part::MultiFuse] Fusion004002009002027014004009002002008002004029002015013017006002012002031033002013006007008014029072011018024002019049062029014012006016002033001057009078004002010031016012003004006002003003002005025003  label="Fusion"
  Refine = true
  Shapes = -> [Extrude007020004,Extrude007020005,Extrude007020006,Extrude007020007]
FEATURE [Part::Cut] Cut176013009033007019019008010045003002004008006010017027003005053020098001031003007007002011005005004026009004013005002003006024015003  label="Cut"
  Base = -> Fusion004002009002027014004009002002008002004029002015013017006002012002031033002013006007008014029072011018024002019049062029014012006016002033001057009078004002010031016012003004006002003003002005025002
  Refine = true
  Tool = -> Fusion004002009002027014004009002002008002004029002015013017006002012002031033002013006007008014029072011018024002019049062029014012006016002033001057009078004002010031016012003004006002003003002005025003
FEATURE [Part::MultiFuse] Fusion004002009002027014004009002002008002004029002015013017006002012002031033002013006007008014029072011018024002019049062029014012006016002033001057009078004002010031016012003004006002003003002005025004  label="Fusion"
  Refine = true
  Shapes = -> [Cylinder1492308,Cylinder1492309,Fillet125007020032053]
FEATURE [Part::Cut] Cut176013009033007019019008010045003002004008006010017027003005053020098001031003007007002011005005004026009004013005002003006024015004  label="Cut"
  Base = -> Cut176013009033007019019008010045003002004008006010017027003005053020098001031003007007002011005005004026009004013005002003006024015003
  Refine = true
  Tool = -> Fusion004002009002027014004009002002008002004029002015013017006002012002031033002013006007008014029072011018024002019049062029014012006016002033001057009078004002010031016012003004006002003003002005025004
FEATURE [Part::Box] Box778  label="Cube"
  AttacherType = Attacher::AttachEngine3D
  Height = 23
  Length = 12
  Placement = pos=(62,-26.2544,60.653) rot=(1,0,0;0.305433rad)
  Width = 2
FEATURE [Part::Box] Box779  label="Cube"
  AttacherType = Attacher::AttachEngine3D
  Height = 23
  Length = 12
  Placement = pos=(75,-26.2537,60.6493) rot=(1,0,0;0.305433rad)
  Width = 2
FEATURE [Part::MultiFuse] Fusion004002009002027014004009002002008002004029002015013017006002012002031033002013006007008014029072011018024002019049062029014012006016002033001057009078004002010031016012003004006002003003002005025005  label="Fusion"
  Refine = true
  Shapes = -> [Box779,Box778]
FEATURE [Part::Feature] Part__Mirroring007002003002018002002002005004004002003004003003004003006  label="Fusion"
  shape: bbox 25 x 8.824 x 22.54 mm, 12 faces, 2 solids (baked)
FEATURE [Part::MultiFuse] Fusion004002009002027014004009002002008002004029002015013017006002012002031033002013006007008014029072011018024002019049062029014012006016002033001057009078004002010031016012003004006002003003002005025010  label="Fusion"
  Refine = true
  Shapes = -> [Fusion004002009002027014004009002002008002004029002015013017006002012002031033002013006007008014029072011018024002019049062029014012006016002033001057009078004002010031016012003004006002003003002005025005,Part__Mirroring007002003002018002002002005004004002003004003003004003006]
FEATURE [Part::Cut] Cut176013009033007019019008010045003002004008006010017027003005053020098001031003007007002011005005004026009004013005002003006024015005  label="rear-axle-oscillation-limiter-10deg"
  Base = -> Cut176013009033007019019008010045003002004008006010017027003005053020098001031003007007002011005005004026009004013005002003006024015004
  Refine = true
  Tool = -> Fusion004002009002027014004009002002008002004029002015013017006002012002031033002013006007008014029072011018024002019049062029014012006016002033001057009078004002010031016012003004006002003003002005025010
FEATURE [App::DocumentObjectGroup] Group003  label="Rear Axle"
  Group = -> [Group005,Group006,Group007,Cut176013009033007019019008010045003002004008006021005004004004004002012033009003,Cut176013009033007019019008010045003002004008006021005004004004004002012033009016002012007022024011,Cut176013009033007019019008010045003002004008006021005004004004004002012033009016002012007022024012,+6 more]
FEATURE [Part::Feature] Cut176013009033007019019008010045003002004008006010017027003005053020098001031003007007002011005005004026009004013005002003006024015007001  label="gearbox-lock-servo-mount"
  shape: bbox 36 x 64 x 30.5 mm, 81 faces (baked)
FEATURE [App::DocumentObjectGroup] Group022  label="Gearbox"
  Group = -> [Cylinder1492253,Cut176013009033007019019008010045003002004008006021005004004004004002012033009016002012007022024086,Fusion088026007031024007008004100051055007010008005020006,Fusion004002009002027014004009002002008002004029002015013017006002012002031033002013006007008014029072011018024002019049062029014012006016002033001057009078004002010031016012003004,+5 more]
FEATURE [Part::Box] Box780  label="Cube"
  AttacherType = Attacher::AttachEngine3D
  Height = 31
  Length = 28
  Placement = pos=(246,-4,45) rot=(0,0,1;0rad)
  Width = 4
FEATURE [Part::Feature] Cut176013009033007019019008010045003002004008006010017027003005053020098001031003007007002011005005004026009004013005002003006020  label="servo-EMAX_ES08MA_II_arm"
  Placement = pos=(0,-1,0) rot=(0,1,0;3.14159rad)
  shape: bbox 6 x 5 x 18 mm, 15 faces (baked)
FEATURE [Part::Feature] Fusion004002009002027014004009002002008002004029002015013017006002012002031033002013006007008014029072011018024002019049062029014012006016002033001057009078004002010031016012003004006002003003002005041  label="servo-EMAX_ES08MA_II"
  Placement = pos=(-5.5,-21,6) rot=(0.707107,0.707107,0;3.14159rad)
  shape: bbox 32 x 27.75 x 12 mm, 30 faces (baked)
FEATURE [Part::Compound] Compound003002002  label="servo-EMAX_ES08MA_II"
  Links = -> [Fusion004002009002027014004009002002008002004029002015013017006002012002031033002013006007008014029072011018024002019049062029014012006016002033001057009078004002010031016012003004006002003003002005041,Cut176013009033007019019008010045003002004008006010017027003005053020098001031003007007002011005005004026009004013005002003006020]
  Placement = pos=(275.1,-2.5,92) rot=(0.707107,-0.707107,0;3.14159rad)
FEATURE [Part::Box] Box781  label="Cube"
  AttacherType = Attacher::AttachEngine3D
  Height = 24
  Length = 22
  Placement = pos=(249,-4,50) rot=(0,0,1;0rad)
  Width = 4
FEATURE [Part::Fillet] Fillet125007020032054
  Base = -> Box781
  Edges = 4 edges r=8: [Edge2,Edge4,Edge6,Edge8]
FEATURE [Part::Cut] Cut176013009033007019019008010045003002004008006010017027003005053020098001031003007007002011005005004026009004013005002003006024015007002  label="Cut"
  Base = -> Box780
  Refine = true
  Tool = -> Fillet125007020032054
FEATURE [Part::Box] Box782  label="Cube"
  AttacherType = Attacher::AttachEngine3D
  Height = 13
  Length = 10
  Placement = pos=(255,-4,37) rot=(0,0,1;0rad)
  Width = 4
FEATURE [Part::Box] Box783  label="Cube"
  AttacherType = Attacher::AttachEngine3D
  Height = 9
  Length = 21.5
  Placement = pos=(252.5,-4,75) rot=(0,0,1;0rad)
  Width = 4
FEATURE [Part::MultiFuse] Fusion004002009002027014004009002002008002004029002015013017006002012002031033002013006007008014029072011018024002019049062029014012006016002033001057009078004002010031016012003004006002003003002005025011  label="Fusion"
  Refine = true
  Shapes = -> [Cut176013009033007019019008010045003002004008006010017027003005053020098001031003007007002011005005004026009004013005002003006024015007002,Box782,Box783]
FEATURE [Part::Chamfer] Chamfer039025078004045
  Base = -> Fusion004002009002027014004009002002008002004029002015013017006002012002031033002013006007008014029072011018024002019049062029014012006016002033001057009078004002010031016012003004006002003003002005025011
  Edges = 1 edges r=12: [Edge27]
FEATURE [Part::Chamfer] Chamfer039025078004046
  Base = -> Chamfer039025078004045
  Edges = 2 edges r=6: [Edge43,Edge46]
FEATURE [Part::Chamfer] Chamfer039025078004047
  Base = -> Chamfer039025078004046
  Edges = 2 edges r=1: [Edge29,Edge42]
FEATURE [Part::Cylinder] Cylinder1492310  label="Cylinder"
  Angle = 360
  AttacherType = Attacher::AttachEngine3D
  FirstAngle = 0
  Height = 28
  Placement = pos=(246,-2,39.5) rot=(0,1,0;1.5708rad)
  Radius = 1
  SecondAngle = 0
FEATURE [Part::Cylinder] Cylinder1492311  label="Cylinder"
  Angle = 360
  AttacherType = Attacher::AttachEngine3D
  FirstAngle = 0
  Height = 28
  Placement = pos=(246,-2,62) rot=(0,1,0;1.5708rad)
  Radius = 0.8
  SecondAngle = 0
FEATURE [Part::Cylinder] Cylinder1492312  label="Cylinder"
  Angle = 360
  AttacherType = Attacher::AttachEngine3D
  FirstAngle = 0
  Height = 17
  Placement = pos=(246,-2,80.5) rot=(0,1,0;1.5708rad)
  Radius = 0.8
  SecondAngle = 0
FEATURE [Part::MultiFuse] Fusion004002009002027014004009002002008002004029002015013017006002012002031033002013006007008014029072011018024002019049062029014012006016002033001057009078004002010031016012003004006002003003002005025012  label="Fusion"
  Refine = true
  Shapes = -> [Cylinder1492310,Cylinder1492311,Cylinder1492312]
FEATURE [Part::Cut] Cut176013009033007019019008010045003002004008006010017027003005053020098001031003007007002011005005004026009004013005002003006024015007003  label="diff-front-lock-lever-ALU4mm"
  Base = -> Chamfer039025078004047
  Placement = pos=(520,-5,0) rot=(0,0,1;3.14159rad)
  Refine = true
  Tool = -> Fusion004002009002027014004009002002008002004029002015013017006002012002031033002013006007008014029072011018024002019049062029014012006016002033001057009078004002010031016012003004006002003003002005025012
FEATURE [Part::Box] Box784  label="Cube"
  AttacherType = Attacher::AttachEngine3D
  Height = 8
  Length = 67
  Placement = pos=(215,-16,35) rot=(0,0,1;0rad)
  Width = 32
FEATURE [Part::Cylinder] Cylinder1492313  label="Cylinder"
  Angle = 360
  AttacherType = Attacher::AttachEngine3D
  FirstAngle = 0
  Height = 67
  Placement = pos=(215,-3,39.5) rot=(0,1,0;1.5708rad)
  Radius = 1
  SecondAngle = 0
FEATURE [Part::Cylinder] Cylinder1492314  label="Cylinder"
  Angle = 360
  AttacherType = Attacher::AttachEngine3D
  FirstAngle = 0
  Height = 32
  Placement = pos=(229,-16,55) rot=(-1,0,0;1.5708rad)
  Radius = 15.5
  SecondAngle = 0
FEATURE [Part::Cylinder] Cylinder1492315  label="Cylinder"
  Angle = 360
  AttacherType = Attacher::AttachEngine3D
  FirstAngle = 0
  Height = 32
  Placement = pos=(260,-16,62) rot=(-1,0,0;1.5708rad)
  Radius = 20
  SecondAngle = 0
FEATURE [Part::Feature] Extrude007020008  label="HEX-BAR-32mm"
  Placement = pos=(277,-16,39) rot=(0,0,1;0rad)
  shape: bbox 6 x 32 x 5.196 mm, 8 faces (baked)
FEATURE [Part::Feature] Extrude007020009  label="HEX-BAR-32mm"
  Placement = pos=(240,-16,39) rot=(0,0,1;0rad)
  shape: bbox 6 x 32 x 5.196 mm, 8 faces (baked)
FEATURE [Part::MultiFuse] Fusion004002009002027014004009002002008002004029002015013017006002012002031033002013006007008014029072011018024002019049062029014012006016002033001057009078004002010031016012003004006002003003002005025014  label="Fusion"
  Refine = true
  Shapes = -> [Extrude007020008,Extrude007020009]
FEATURE [Part::Cut] Cut176013009033007019019008010045003002004008006010017027003005053020098001031003007007002011005005004026009004013005002003006024015007004  label="Cut"
  Base = -> Box784
  Refine = true
  Tool = -> Fusion004002009002027014004009002002008002004029002015013017006002012002031033002013006007008014029072011018024002019049062029014012006016002033001057009078004002010031016012003004006002003003002005025014
FEATURE [Part::Box] Box785  label="Cube"
  AttacherType = Attacher::AttachEngine3D
  Height = 8
  Length = 10.5
  Placement = pos=(254.75,-16,35.75) rot=(0,0,1;0rad)
  Width = 18
FEATURE [Part::MultiFuse] Fusion004002009002027014004009002002008002004029002015013017006002012002031033002013006007008014029072011018024002019049062029014012006016002033001057009078004002010031016012003004006002003003002005025015  label="Fusion"
  Refine = true
  Shapes = -> [Cylinder1492314,Cylinder1492315]
FEATURE [Part::Cut] Cut176013009033007019019008010045003002004008006010017027003005053020098001031003007007002011005005004026009004013005002003006024015007005  label="Cut"
  Base = -> Cut176013009033007019019008010045003002004008006010017027003005053020098001031003007007002011005005004026009004013005002003006024015007004
  Refine = true
  Tool = -> Fusion004002009002027014004009002002008002004029002015013017006002012002031033002013006007008014029072011018024002019049062029014012006016002033001057009078004002010031016012003004006002003003002005025015
FEATURE [Part::Cut] Cut176013009033007019019008010045003002004008006010017027003005053020098001031003007007002011005005004026009004013005002003006024015007006  label="Cut"
  Base = -> Cut176013009033007019019008010045003002004008006010017027003005053020098001031003007007002011005005004026009004013005002003006024015007005
  Refine = true
  Tool = -> Box785
FEATURE [Part::Cylinder] Cylinder1492316  label="Cylinder"
  Angle = 360
  AttacherType = Attacher::AttachEngine3D
  FirstAngle = 0
  Height = 5
  Placement = pos=(277,-14,37) rot=(0,1,0;1.5708rad)
  Radius = 0.9
  SecondAngle = 0
FEATURE [Part::Cylinder] Cylinder1492317  label="Cylinder"
  Angle = 360
  AttacherType = Attacher::AttachEngine3D
  FirstAngle = 0
  Height = 5
  Placement = pos=(277,14,37) rot=(0,1,0;1.5708rad)
  Radius = 0.9
  SecondAngle = 0
FEATURE [Part::MultiFuse] Fusion004002009002027014004009002002008002004029002015013017006002012002031033002013006007008014029072011018024002019049062029014012006016002033001057009078004002010031016012003004006002003003002005025016  label="Fusion"
  Refine = true
  Shapes = -> [Cylinder1492313,Cylinder1492316,Cylinder1492317]
FEATURE [Part::Cut] Cut176013009033007019019008010045003002004008006010017027003005053020098001031003007007002011005005004026009004013005002003006024015007007  label="diff-front-bottom"
  Base = -> Cut176013009033007019019008010045003002004008006010017027003005053020098001031003007007002011005005004026009004013005002003006024015007006
  Refine = true
  Tool = -> Fusion004002009002027014004009002002008002004029002015013017006002012002031033002013006007008014029072011018024002019049062029014012006016002033001057009078004002010031016012003004006002003003002005025016
FEATURE [Part::Box] Box786  label="Cube"
  AttacherType = Attacher::AttachEngine3D
  Height = 51
  Length = 34
  Placement = pos=(243,-5,35) rot=(0,0,1;0rad)
  Width = 5
FEATURE [Part::Box] Box787  label="Cube"
  AttacherType = Attacher::AttachEngine3D
  Height = 47.4
  Length = 28.4
  Placement = pos=(245.8,-5,36.8) rot=(0,0,1;0rad)
  Width = 4
FEATURE [Part::Box] Box788  label="Cube"
  AttacherType = Attacher::AttachEngine3D
  Height = 8.4
  Length = 6.4
  Placement = pos=(245.8,-5,76.3) rot=(0,0,1;0rad)
  Width = 5
FEATURE [Part::Cut] Cut176013009033007019019008010045003002004008006010017027003005053020098001031003007007002011005005004026009004013005002003006024015007008  label="Cut"
  Base = -> Box786
  Refine = true
  Tool = -> Box787
FEATURE [Part::Cylinder] Cylinder1492318  label="Cylinder"
  Angle = 360
  AttacherType = Attacher::AttachEngine3D
  FirstAngle = 0
  Height = 34
  Placement = pos=(243,-3,62) rot=(0,1,0;1.5708rad)
  Radius = 0.8
  SecondAngle = 0
FEATURE [Part::Cylinder] Cylinder1492319  label="Cylinder"
  Angle = 360
  AttacherType = Attacher::AttachEngine3D
  FirstAngle = 0
  Height = 34
  Placement = pos=(243,-3,39.5) rot=(0,1,0;1.5708rad)
  Radius = 1
  SecondAngle = 0
FEATURE [Part::Cylinder] Cylinder1492320  label="Cylinder"
  Angle = 360
  AttacherType = Attacher::AttachEngine3D
  FirstAngle = 0
  Height = 17
  Placement = pos=(243,-3,80.5) rot=(0,1,0;1.5708rad)
  Radius = 0.8
  SecondAngle = 0
FEATURE [Part::MultiFuse] Fusion004002009002027014004009002002008002004029002015013017006002012002031033002013006007008014029072011018024002019049062029014012006016002033001057009078004002010031016012003004006002003003002005025018  label="Fusion"
  Refine = true
  Shapes = -> [Cylinder1492318,Cylinder1492319,Cylinder1492320]
FEATURE [Part::Box] Box789  label="Cube"
  AttacherType = Attacher::AttachEngine3D
  Height = 7
  Length = 9
  Placement = pos=(245.8,-5,36) rot=(0,0,1;0rad)
  Width = 5
FEATURE [Part::Box] Box790  label="Cube"
  AttacherType = Attacher::AttachEngine3D
  Height = 7
  Length = 9
  Placement = pos=(265.2,-5,36) rot=(0,0,1;0rad)
  Width = 5
FEATURE [Part::MultiFuse] Fusion004002009002027014004009002002008002004029002015013017006002012002031033002013006007008014029072011018024002019049062029014012006016002033001057009078004002010031016012003004006002003003002005025019  label="Fusion"
  Refine = true
  Shapes = -> [Box788,Box789,Box790,Cut176013009033007019019008010045003002004008006010017027003005053020098001031003007007002011005005004026009004013005002003006024015007008]
FEATURE [Part::Cut] Cut176013009033007019019008010045003002004008006010017027003005053020098001031003007007002011005005004026009004013005002003006024015007009  label="diff-front-lock-lever-TOOL"
  Base = -> Fusion004002009002027014004009002002008002004029002015013017006002012002031033002013006007008014029072011018024002019049062029014012006016002033001057009078004002010031016012003004006002003003002005025019
  Refine = true
  Tool = -> Fusion004002009002027014004009002002008002004029002015013017006002012002031033002013006007008014029072011018024002019049062029014012006016002033001057009078004002010031016012003004006002003003002005025018
FEATURE [App::DocumentObjectGroup] Group020  label="Tools"
  Group = -> [Cut176013009033007019019008010045003002004008006021005004004004004002012033009016002012007022024048,Cut176013009033007019019008010045003002004008006021005004004004004002012033009016002012007022024049,Cut176013009033007019019008010045003002004008006010017027003005053020098001031003007007002011005005004026009004013004,+1 more]
FEATURE [Part::Box] Box791  label="Cube"
  AttacherType = Attacher::AttachEngine3D
  Height = 10.8
  Length = 10.8
  Placement = pos=(254.6,-7,56.6) rot=(0,0,1;0rad)
  Width = 20
FEATURE [Part::Cylinder] Cylinder1492321  label="Cylinder"
  Angle = 360
  AttacherType = Attacher::AttachEngine3D
  FirstAngle = 0
  Height = 4
  Placement = pos=(260,4,62) rot=(-1,0,0;1.5708rad)
  Radius = 15
  SecondAngle = 0
FEATURE [Part::Cylinder] Cylinder1492322  label="Cylinder"
  Angle = 360
  AttacherType = Attacher::AttachEngine3D
  FirstAngle = 0
  Height = 8
  Placement = pos=(260,-4,62) rot=(-1,0,0;1.5708rad)
  Radius = 10.5
  SecondAngle = 0
FEATURE [Part::Cylinder] Cylinder1492323  label="Cylinder"
  Angle = 360
  AttacherType = Attacher::AttachEngine3D
  FirstAngle = 0
  Height = 2.1
  Placement = pos=(260,-1,62) rot=(-1,0,0;1.5708rad)
  Radius = 10.5
  SecondAngle = 0
FEATURE [Part::Cylinder] Cylinder1492324  label="Cylinder"
  Angle = 360
  AttacherType = Attacher::AttachEngine3D
  FirstAngle = 0
  Height = 2.1
  Placement = pos=(260,-1,62) rot=(-1,0,0;1.5708rad)
  Radius = 9
  SecondAngle = 0
FEATURE [Part::Cut] Cut176013009033007019019008010045003002004008006010017027003005053020098001031003007007002011005005004026009004013005002003006024015007013  label="Cut"
  Base = -> Cylinder1492323
  Refine = true
  Tool = -> Cylinder1492324
FEATURE [Part::Cylinder] Cylinder1492325  label="Cylinder"
  Angle = 360
  AttacherType = Attacher::AttachEngine3D
  FirstAngle = 0
  Height = 25
  Placement = pos=(254.75,46,56.75) rot=(1,0,0;1.5708rad)
  Radius = 0.5
  SecondAngle = 0
FEATURE [Part::Cylinder] Cylinder1492326  label="Cylinder"
  Angle = 360
  AttacherType = Attacher::AttachEngine3D
  FirstAngle = 0
  Height = 25
  Placement = pos=(265.25,46,56.75) rot=(1,0,0;1.5708rad)
  Radius = 0.5
  SecondAngle = 0
FEATURE [Part::Cylinder] Cylinder1492327  label="Cylinder"
  Angle = 360
  AttacherType = Attacher::AttachEngine3D
  FirstAngle = 0
  Height = 25
  Placement = pos=(254.75,46,67.25) rot=(1,0,0;1.5708rad)
  Radius = 0.5
  SecondAngle = 0
FEATURE [Part::Cylinder] Cylinder1492328  label="Cylinder"
  Angle = 360
  AttacherType = Attacher::AttachEngine3D
  FirstAngle = 0
  Height = 25
  Placement = pos=(265.25,46,67.25) rot=(1,0,0;1.5708rad)
  Radius = 0.5
  SecondAngle = 0
FEATURE [Part::Cylinder] Cylinder1492329
  Angle = 100
  AttacherType = Attacher::AttachEngine3D
  FirstAngle = 0
  Height = 2.5
  Radius = 8.3
  SecondAngle = 0
FEATURE [Part::Cylinder] Cylinder1492330
  Angle = 100
  AttacherType = Attacher::AttachEngine3D
  FirstAngle = 0
  Height = 2.5
  Radius = 12.7
  SecondAngle = 0
FEATURE [Part::Cut] Cut176013009033007019019008010045003002004008006010017027003005053020098001031003007007002011005005004026009004013005002003006024015007010  label="Cut"
  Base = -> Cylinder1492330
  Placement = pos=(0,0,-2.5) rot=(0,0,1;0.244346rad)
  Refine = true
  Tool = -> Cylinder1492329
FEATURE [Part::Cylinder] Cylinder1492331
  Angle = 100
  AttacherType = Attacher::AttachEngine3D
  FirstAngle = 0
  Height = 2.5
  Radius = 8.3
  SecondAngle = 0
FEATURE [Part::Cylinder] Cylinder1492332
  Angle = 100
  AttacherType = Attacher::AttachEngine3D
  FirstAngle = 0
  Height = 2.5
  Radius = 12.7
  SecondAngle = 0
FEATURE [Part::Cut] Cut176013009033007019019008010045003002004008006010017027003005053020098001031003007007002011005005004026009004013005002003006024015007011  label="Cut"
  Base = -> Cylinder1492332
  Placement = pos=(0,0,-2.5) rot=(0,0,1;0.244346rad)
  Refine = true
  Tool = -> Cylinder1492331
FEATURE [Part::Cylinder] Cylinder1492333
  Angle = 100
  AttacherType = Attacher::AttachEngine3D
  FirstAngle = 0
  Height = 2.5
  Radius = 8.3
  SecondAngle = 0
FEATURE [Part::Cylinder] Cylinder1492334
  Angle = 100
  AttacherType = Attacher::AttachEngine3D
  FirstAngle = 0
  Height = 2.5
  Radius = 12.7
  SecondAngle = 0
FEATURE [Part::Cut] Cut176013009033007019019008010045003002004008006010017027003005053020098001031003007007002011005005004026009004013005002003006024015007012  label="Cut"
  Base = -> Cylinder1492334
  Placement = pos=(0,0,-2.5) rot=(0,0,1;0.244346rad)
  Refine = true
  Tool = -> Cylinder1492333
FEATURE [Part::Fillet] Fillet125007020032055
  Base = -> Cut176013009033007019019008010045003002004008006010017027003005053020098001031003007007002011005005004026009004013005002003006024015007010
  Edges = 4 edges: [Edge1 r=1,Edge2 r=1.2,Edge7 r=1,Edge9 r=1.2]
  Placement = pos=(0,0,8.5) rot=(0,0,1;0rad)
FEATURE [Part::Fillet] Fillet125007020032056
  Base = -> Cut176013009033007019019008010045003002004008006010017027003005053020098001031003007007002011005005004026009004013005002003006024015007011
  Edges = 4 edges: [Edge1 r=1,Edge2 r=1.2,Edge7 r=1,Edge9 r=1.2]
  Placement = pos=(0,0,8.5) rot=(0,0,1;2.0944rad)
FEATURE [Part::Fillet] Fillet125007020032057
  Base = -> Cut176013009033007019019008010045003002004008006010017027003005053020098001031003007007002011005005004026009004013005002003006024015007012
  Edges = 4 edges: [Edge1 r=1,Edge2 r=1.2,Edge7 r=1,Edge9 r=1.2]
  Placement = pos=(0,0,8.5) rot=(0,0,1;4.18879rad)
FEATURE [Part::MultiFuse] Fusion004002009002027014004009002002008002004029002015013017006002012002031033002013006007008014029072011018024002019049062029014012006016002033001057009078004002010031016012003004006002003003002005025020  label="Fusion"
  Refine = true
  Shapes = -> [Cylinder1492322,Cylinder1492321]
FEATURE [Part::Cut] Cut176013009033007019019008010045003002004008006010017027003005053020098001031003007007002011005005004026009004013005002003006024015007014  label="Cut"
  Base = -> Fusion004002009002027014004009002002008002004029002015013017006002012002031033002013006007008014029072011018024002019049062029014012006016002033001057009078004002010031016012003004006002003003002005025020
  Refine = true
  Tool = -> Cut176013009033007019019008010045003002004008006010017027003005053020098001031003007007002011005005004026009004013005002003006024015007013
FEATURE [Part::MultiFuse] Fusion004002009002027014004009002002008002004029002015013017006002012002031033002013006007008014029072011018024002019049062029014012006016002033001057009078004002010031016012003004006002003003002005025021  label="Fusion"
  Placement = pos=(0,-36,0) rot=(0,0,1;0rad)
  Refine = true
  Shapes = -> [Cylinder1492325,Cylinder1492326,Cylinder1492327,Cylinder1492328]
FEATURE [Part::MultiFuse] Fusion004002009002027014004009002002008002004029002015013017006002012002031033002013006007008014029072011018024002019049062029014012006016002033001057009078004002010031016012003004006002003003002005025022  label="Fusion"
  Placement = pos=(260,-0.5,62) rot=(0.57735,-0.57735,-0.57735;4.18879rad)
  Refine = true
  Shapes = -> [Fillet125007020032057,Fillet125007020032055,Fillet125007020032056]
FEATURE [Part::Cut] Cut176013009033007019019008010045003002004008006010017027003005053020098001031003007007002011005005004026009004013005002003006024015007015  label="Cut"
  Base = -> Cut176013009033007019019008010045003002004008006010017027003005053020098001031003007007002011005005004026009004013005002003006024015007014
  Refine = true
  Tool = -> Fusion004002009002027014004009002002008002004029002015013017006002012002031033002013006007008014029072011018024002019049062029014012006016002033001057009078004002010031016012003004006002003003002005025022
FEATURE [Part::Cut] Cut176013009033007019019008010045003002004008006010017027003005053020098001031003007007002011005005004026009004013005002003006024015007016  label="Cut"
  Base = -> Cut176013009033007019019008010045003002004008006010017027003005053020098001031003007007002011005005004026009004013005002003006024015007015
  Placement = pos=(0,-3,0) rot=(0,0,1;0rad)
  Refine = true
  Tool = -> Box791
FEATURE [Part::Cut] Cut176013009033007019019008010045003002004008006010017027003005053020098001031003007007002011005005004026009004013005002003006024015007017  label="diff_front_lock"
  Base = -> Cut176013009033007019019008010045003002004008006010017027003005053020098001031003007007002011005005004026009004013005002003006024015007016
  Placement = pos=(0,-1,0) rot=(0,0,1;0rad)
  Refine = true
  Tool = -> Fusion004002009002027014004009002002008002004029002015013017006002012002031033002013006007008014029072011018024002019049062029014012006016002033001057009078004002010031016012003004006002003003002005025021
FEATURE [App::DocumentObjectGroup] Group021  label="Gears"
  Group = -> [Cut176013009033007019019008010045003002004008006021005004004004004002012033009016002002,Fusion088026007031024007008004100051055007010008005020019001,Cut176013009033007019019008010045003002004008006021005004004004004002012033009016002012007022016,Cut176013009033007019019008010045003002004008006021005004004004004002012033009016002012007022017,+9 more]
FEATURE [Part::Box] Box792  label="Cube"
  AttacherType = Attacher::AttachEngine3D
  Height = 8
  Length = 67
  Placement = pos=(215,-16,78) rot=(0,0,1;0rad)
  Width = 32
FEATURE [Part::Feature] Extrude007020010  label="HEX-BAR-32mm"
  Placement = pos=(277,-16,82) rot=(0,0,1;0rad)
  shape: bbox 6 x 32 x 5.196 mm, 8 faces (baked)
FEATURE [Part::Feature] Extrude007020011  label="HEX-BAR-32mm"
  Placement = pos=(243,-16,82) rot=(0,0,1;0rad)
  shape: bbox 6 x 32 x 5.196 mm, 8 faces (baked)
FEATURE [Part::MultiFuse] Fusion004002009002027014004009002002008002004029002015013017006002012002031033002013006007008014029072011018024002019049062029014012006016002033001057009078004002010031016012003004006002003003002005025023  label="Fusion"
  Refine = true
  Shapes = -> [Extrude007020010,Extrude007020011]
FEATURE [Part::Cut] Cut176013009033007019019008010045003002004008006010017027003005053020098001031003007007002011005005004026009004013005002003006024015007018  label="Cut"
  Base = -> Box792
  Refine = true
  Tool = -> Fusion004002009002027014004009002002008002004029002015013017006002012002031033002013006007008014029072011018024002019049062029014012006016002033001057009078004002010031016012003004006002003003002005025023
FEATURE [Part::Cylinder] Cylinder1492335  label="Cylinder"
  Angle = 360
  AttacherType = Attacher::AttachEngine3D
  FirstAngle = 0
  Height = 32
  Placement = pos=(260,-16,62) rot=(-1,0,0;1.5708rad)
  Radius = 20
  SecondAngle = 0
FEATURE [Part::Cylinder] Cylinder1492336  label="Cylinder"
  Angle = 360
  AttacherType = Attacher::AttachEngine3D
  FirstAngle = 0
  Height = 5
  Placement = pos=(277,14,84) rot=(0,1,0;1.5708rad)
  Radius = 0.9
  SecondAngle = 0
FEATURE [Part::Cylinder] Cylinder1492337  label="Cylinder"
  Angle = 360
  AttacherType = Attacher::AttachEngine3D
  FirstAngle = 0
  Height = 5
  Placement = pos=(277,-14,84) rot=(0,1,0;1.5708rad)
  Radius = 0.9
  SecondAngle = 0
FEATURE [Part::MultiFuse] Fusion004002009002027014004009002002008002004029002015013017006002012002031033002013006007008014029072011018024002019049062029014012006016002033001057009078004002010031016012003004006002003003002005025024  label="Fusion"
  Refine = true
  Shapes = -> [Cylinder1492337,Cylinder1492336]
FEATURE [Part::Cut] Cut176013009033007019019008010045003002004008006010017027003005053020098001031003007007002011005005004026009004013005002003006024015007019  label="Cut"
  Base = -> Cut176013009033007019019008010045003002004008006010017027003005053020098001031003007007002011005005004026009004013005002003006024015007018
  Refine = true
  Tool = -> Fusion004002009002027014004009002002008002004029002015013017006002012002031033002013006007008014029072011018024002019049062029014012006016002033001057009078004002010031016012003004006002003003002005025024
FEATURE [Part::Cut] Cut176013009033007019019008010045003002004008006010017027003005053020098001031003007007002011005005004026009004013005002003006024015007020  label="Cut"
  Base = -> Cut176013009033007019019008010045003002004008006010017027003005053020098001031003007007002011005005004026009004013005002003006024015007019
  Refine = true
  Tool = -> Cylinder1492335
FEATURE [Part::Box] Box793  label="Cube"
  AttacherType = Attacher::AttachEngine3D
  Height = 8
  Length = 22
  Placement = pos=(217,-16,76) rot=(0,0,1;0rad)
  Width = 32
FEATURE [Part::Fillet] Fillet125007020032058
  Base = -> Box793
  Edges = 2 edges r=5: [Edge2,Edge6]
FEATURE [Part::Cut] Cut176013009033007019019008010045003002004008006010017027003005053020098001031003007007002011005005004026009004013005002003006024015007021  label="Cut"
  Base = -> Cut176013009033007019019008010045003002004008006010017027003005053020098001031003007007002011005005004026009004013005002003006024015007020
  Refine = true
  Tool = -> Fillet125007020032058
FEATURE [Part::Box] Box794  label="Cube"
  AttacherType = Attacher::AttachEngine3D
  Height = 8
  Length = 9
  Placement = pos=(248,-9,78) rot=(0,0,1;0rad)
  Width = 13
FEATURE [Part::Cut] Cut176013009033007019019008010045003002004008006010017027003005053020098001031003007007002011005005004026009004013005002003006024015007022  label="Cut"
  Base = -> Cut176013009033007019019008010045003002004008006010017027003005053020098001031003007007002011005005004026009004013005002003006024015007021
  Refine = true
  Tool = -> Box794
FEATURE [Part::Box] Box796  label="Cube"
  AttacherType = Attacher::AttachEngine3D
  Height = 12
  Length = 14.5
  Placement = pos=(247,3.2,86) rot=(0,0,1;0rad)
  Width = 3.8
FEATURE [Part::Box] Box797  label="Cube"
  AttacherType = Attacher::AttachEngine3D
  Height = 12
  Length = 14.5
  Placement = pos=(247,-25,86) rot=(0,0,1;0rad)
  Width = 3.8
FEATURE [Part::Box] Box798  label="Cube"
  AttacherType = Attacher::AttachEngine3D
  Height = 6
  Length = 8
  Placement = pos=(247,-25,86) rot=(0,0,1;0rad)
  Width = 10
FEATURE [Part::Box] Box799  label="Cube"
  AttacherType = Attacher::AttachEngine3D
  Height = 6
  Length = 6
  Placement = pos=(247,-25,86) rot=(0,0,1;0rad)
  Width = 16
FEATURE [Part::Box] Box800  label="Cube"
  AttacherType = Attacher::AttachEngine3D
  Height = 6
  Length = 1
  Placement = pos=(247,-25,86) rot=(0,0,1;0rad)
  Width = 32
FEATURE [Part::Chamfer] Chamfer039025078004048
  Base = -> Box796
  Edges = 1 edges r=6: [Edge2]
FEATURE [Part::Chamfer] Chamfer039025078004049
  Base = -> Box797
  Edges = 1 edges r=6: [Edge2]
FEATURE [Part::Chamfer] Chamfer039025078004050
  Base = -> Box798
  Edges = 1 edges: [Edge7 r1=4 r2=2]
FEATURE [Part::Box] Box801  label="Cube"
  AttacherType = Attacher::AttachEngine3D
  Height = 3
  Length = 14.5
  Placement = pos=(247,4,86) rot=(0,0,1;0rad)
  Width = 9
FEATURE [Part::MultiFuse] Fusion004002009002027014004009002002008002004029002015013017006002012002031033002013006007008014029072011018024002019049062029014012006016002033001057009078004002010031016012003004006002003003002005025025  label="Fusion"
  Refine = true
  Shapes = -> [Box799,Box800,Chamfer039025078004048,Chamfer039025078004049,Chamfer039025078004050,Box801]
FEATURE [Part::Fillet] Fillet125007020032059
  Base = -> Fusion004002009002027014004009002002008002004029002015013017006002012002031033002013006007008014029072011018024002019049062029014012006016002033001057009078004002010031016012003004006002003003002005025025
  Edges = 2 edges r=3: [Edge3,Edge9]
FEATURE [Part::Cylinder] Cylinder1492338  label="Cylinder"
  Angle = 360
  AttacherType = Attacher::AttachEngine3D
  FirstAngle = 0
  Height = 15
  Placement = pos=(254,10,82) rot=(0,0,1;0rad)
  Radius = 1.6
  SecondAngle = 0
FEATURE [Part::Cylinder] Cylinder1492339  label="Cylinder"
  Angle = 360
  AttacherType = Attacher::AttachEngine3D
  FirstAngle = 0
  Height = 15
  Placement = pos=(250,-12.5,82) rot=(0,0,1;0rad)
  Radius = 1.6
  SecondAngle = 0
FEATURE [Part::MultiFuse] Fusion004002009002027014004009002002008002004029002015013017006002012002031033002013006007008014029072011018024002019049062029014012006016002033001057009078004002010031016012003004006002003003002005025026  label="Fusion"
  Refine = true
  Shapes = -> [Cylinder1492339,Cylinder1492338]
FEATURE [Part::Cylinder] Cylinder1492340  label="Cylinder"
  Angle = 360
  AttacherType = Attacher::AttachEngine3D
  FirstAngle = 0
  Height = 15
  Placement = pos=(254,10,82) rot=(0,0,1;0rad)
  Radius = 1.25
  SecondAngle = 0
FEATURE [Part::Cylinder] Cylinder1492341  label="Cylinder"
  Angle = 360
  AttacherType = Attacher::AttachEngine3D
  FirstAngle = 0
  Height = 15
  Placement = pos=(250,-12.5,82) rot=(0,0,1;0rad)
  Radius = 1.25
  SecondAngle = 0
FEATURE [Part::MultiFuse] Fusion004002009002027014004009002002008002004029002015013017006002012002031033002013006007008014029072011018024002019049062029014012006016002033001057009078004002010031016012003004006002003003002005025027  label="Fusion"
  Placement = pos=(0,0,-6) rot=(0,0,1;0rad)
  Refine = true
  Shapes = -> [Cylinder1492341,Cylinder1492340]
FEATURE [Part::Cut] Cut176013009033007019019008010045003002004008006010017027003005053020098001031003007007002011005005004026009004013005002003006024015007023  label="Cut"
  Base = -> Fillet125007020032059
  Refine = true
  Tool = -> Fusion004002009002027014004009002002008002004029002015013017006002012002031033002013006007008014029072011018024002019049062029014012006016002033001057009078004002010031016012003004006002003003002005025026
FEATURE [Part::Cylinder] Cylinder1492342  label="Cylinder"
  Angle = 360
  AttacherType = Attacher::AttachEngine3D
  FirstAngle = 0
  Height = 8
  Placement = pos=(261.5,-22.85,92) rot=(0,-1,0;1.5708rad)
  Radius = 0.9
  SecondAngle = 0
FEATURE [Part::Cylinder] Cylinder1492343  label="Cylinder"
  Angle = 360
  AttacherType = Attacher::AttachEngine3D
  FirstAngle = 0
  Height = 8
  Placement = pos=(261.5,4.75,92) rot=(0,-1,0;1.5708rad)
  Radius = 0.9
  SecondAngle = 0
FEATURE [Part::MultiFuse] Fusion004002009002027014004009002002008002004029002015013017006002012002031033002013006007008014029072011018024002019049062029014012006016002033001057009078004002010031016012003004006002003003002005025028  label="Fusion"
  Refine = true
  Shapes = -> [Cylinder1492343,Cylinder1492342]
FEATURE [Part::Cut] Cut176013009033007019019008010045003002004008006010017027003005053020098001031003007007002011005005004026009004013005002003006024015007024  label="Cut"
  Base = -> Cut176013009033007019019008010045003002004008006010017027003005053020098001031003007007002011005005004026009004013005002003006024015007023
  Refine = true
  Tool = -> Fusion004002009002027014004009002002008002004029002015013017006002012002031033002013006007008014029072011018024002019049062029014012006016002033001057009078004002010031016012003004006002003003002005025028
FEATURE [Part::Fillet] Fillet125007020032060  label="diff-front-lock-servo-mount"
  Base = -> Cut176013009033007019019008010045003002004008006010017027003005053020098001031003007007002011005005004026009004013005002003006024015007024
  Edges = 2 edges r=6: [Edge41,Edge45]
FEATURE [Part::Cut] Cut176013009033007019019008010045003002004008006010017027003005053020098001031003007007002011005005004026009004013005002003006024015007026  label="diff-front-top"
  Base = -> Cut176013009033007019019008010045003002004008006010017027003005053020098001031003007007002011005005004026009004013005002003006024015007022
  Refine = true
  Tool = -> Fusion004002009002027014004009002002008002004029002015013017006002012002031033002013006007008014029072011018024002019049062029014012006016002033001057009078004002010031016012003004006002003003002005025027
FEATURE [App::DocumentObjectGroup] Group012  label="Backups"
  Group = -> [Line018,Cut176013009033007019019008010045003002004008006021005004004004004002012033009009,Cut176013009033007019019008010045003002004008006021005004004004004002012033009016002006,Cut176013009033007019019008010045003002004008006021005004004004004002012033009016002012,Cut176013009033007019019008010045003002004008006021005004004004004002012033009016002005,+12 more]
FEATURE [Part::Box] Box803  label="Cube"
  AttacherType = Attacher::AttachEngine3D
  Height = 8
  Length = 67
  Placement = pos=(215,-16,78) rot=(0,0,1;0rad)
  Width = 32
FEATURE [Part::Box] Box804  label="Cube"
  AttacherType = Attacher::AttachEngine3D
  Height = 8
  Length = 22
  Placement = pos=(217,-16,76) rot=(0,0,1;0rad)
  Width = 32
FEATURE [Part::Box] Box805  label="Cube"
  AttacherType = Attacher::AttachEngine3D
  Height = 7
  Length = 21.5
  Placement = pos=(252,-9,78) rot=(0,0,1;0rad)
  Width = 15
FEATURE [Part::Box] Box806  label="Cube"
  AttacherType = Attacher::AttachEngine3D
  Height = 12
  Length = 14.5
  Placement = pos=(247,3.2,86) rot=(0,0,1;0rad)
  Width = 3.8
FEATURE [Part::Box] Box807  label="Cube"
  AttacherType = Attacher::AttachEngine3D
  Height = 12
  Length = 14.5
  Placement = pos=(247,-25,86) rot=(0,0,1;0rad)
  Width = 3.8
FEATURE [Part::Box] Box808  label="Cube"
  AttacherType = Attacher::AttachEngine3D
  Height = 6
  Length = 8
  Placement = pos=(247,-25,86) rot=(0,0,1;0rad)
  Width = 10
FEATURE [Part::Box] Box809  label="Cube"
  AttacherType = Attacher::AttachEngine3D
  Height = 6
  Length = 6
  Placement = pos=(247,-25,86) rot=(0,0,1;0rad)
  Width = 16
FEATURE [Part::Box] Box810  label="Cube"
  AttacherType = Attacher::AttachEngine3D
  Height = 6
  Length = 3
  Placement = pos=(245,-25,86) rot=(0,0,1;0rad)
  Width = 32
FEATURE [Part::Box] Box811  label="Cube"
  AttacherType = Attacher::AttachEngine3D
  Height = 3
  Length = 16.5
  Placement = pos=(245,4,86) rot=(0,0,1;0rad)
  Width = 9
FEATURE [Part::Chamfer] Chamfer039025078004052
  Base = -> Box806
  Edges = 1 edges r=6: [Edge2]
FEATURE [Part::Chamfer] Chamfer039025078004053
  Base = -> Box807
  Edges = 1 edges r=6: [Edge2]
FEATURE [Part::Chamfer] Chamfer039025078004054
  Base = -> Box808
  Edges = 1 edges: [Edge7 r1=4 r2=2]
FEATURE [Part::Cylinder] Cylinder1492344  label="Cylinder"
  Angle = 360
  AttacherType = Attacher::AttachEngine3D
  FirstAngle = 0
  Height = 32
  Placement = pos=(260,-16,62) rot=(-1,0,0;1.5708rad)
  Radius = 20
  SecondAngle = 0
FEATURE [Part::Cylinder] Cylinder1492345  label="Cylinder"
  Angle = 360
  AttacherType = Attacher::AttachEngine3D
  FirstAngle = 0
  Height = 5
  Placement = pos=(277,14,84) rot=(0,1,0;1.5708rad)
  Radius = 0.9
  SecondAngle = 0
FEATURE [Part::Cylinder] Cylinder1492346  label="Cylinder"
  Angle = 360
  AttacherType = Attacher::AttachEngine3D
  FirstAngle = 0
  Height = 5
  Placement = pos=(277,-14,84) rot=(0,1,0;1.5708rad)
  Radius = 0.9
  SecondAngle = 0
FEATURE [Part::Cylinder] Cylinder1492347  label="Cylinder"
  Angle = 360
  AttacherType = Attacher::AttachEngine3D
  FirstAngle = 0
  Height = 15
  Placement = pos=(253,10,82) rot=(0,0,1;0rad)
  Radius = 1.6
  SecondAngle = 0
FEATURE [Part::Cylinder] Cylinder1492348  label="Cylinder"
  Angle = 360
  AttacherType = Attacher::AttachEngine3D
  FirstAngle = 0
  Height = 15
  Placement = pos=(250,-12.5,82) rot=(0,0,1;0rad)
  Radius = 1.6
  SecondAngle = 0
FEATURE [Part::Cylinder] Cylinder1492349  label="Cylinder"
  Angle = 360
  AttacherType = Attacher::AttachEngine3D
  FirstAngle = 0
  Height = 15
  Placement = pos=(253,10,82) rot=(0,0,1;0rad)
  Radius = 1.25
  SecondAngle = 0
FEATURE [Part::Cylinder] Cylinder1492350  label="Cylinder"
  Angle = 360
  AttacherType = Attacher::AttachEngine3D
  FirstAngle = 0
  Height = 15
  Placement = pos=(250,-12.5,82) rot=(0,0,1;0rad)
  Radius = 1.25
  SecondAngle = 0
FEATURE [Part::Cylinder] Cylinder1492351  label="Cylinder"
  Angle = 360
  AttacherType = Attacher::AttachEngine3D
  FirstAngle = 0
  Height = 8
  Placement = pos=(261.5,-22.85,92) rot=(0,-1,0;1.5708rad)
  Radius = 0.9
  SecondAngle = 0
FEATURE [Part::Cylinder] Cylinder1492352  label="Cylinder"
  Angle = 360
  AttacherType = Attacher::AttachEngine3D
  FirstAngle = 0
  Height = 8
  Placement = pos=(261.5,4.75,92) rot=(0,-1,0;1.5708rad)
  Radius = 0.9
  SecondAngle = 0
FEATURE [Part::Feature] Extrude007020012  label="HEX-BAR-32mm"
  Placement = pos=(277,-16,82) rot=(0,0,1;0rad)
  shape: bbox 6 x 32 x 5.196 mm, 8 faces (baked)
FEATURE [Part::Feature] Extrude007020013  label="HEX-BAR-32mm"
  Placement = pos=(243,-16,82) rot=(0,0,1;0rad)
  shape: bbox 6 x 32 x 5.196 mm, 8 faces (baked)
FEATURE [Part::Fillet] Fillet125007020032060003
  Base = -> Box804
  Edges = 2 edges r=5: [Edge2,Edge6]
FEATURE [Part::MultiFuse] Fusion004002009002027014004009002002008002004029002015013017006002012002031033002013006007008014029072011018024002019049062029014012006016002033001057009078004002010031016012003004006002003003002005025029
  Placement = pos=(18,0,0) rot=(0,0,1;0rad)
  Refine = true
  Shapes = -> [Box809,Box810,Box811,Chamfer039025078004052,Chamfer039025078004053,Chamfer039025078004054]
FEATURE [Part::MultiFuse] Fusion004002009002027014004009002002008002004029002015013017006002012002031033002013006007008014029072011018024002019049062029014012006016002033001057009078004002010031016012003004006002003003002005025030  label="Fusion"
  Refine = true
  Shapes = -> [Extrude007020012,Extrude007020013]
FEATURE [Part::Cut] Cut176013009033007019019008010045003002004008006010017027003005053020098001031003007007002011005005004026009004013005002003006024015007003004  label="Cut"
  Base = -> Box803
  Refine = true
  Tool = -> Fusion004002009002027014004009002002008002004029002015013017006002012002031033002013006007008014029072011018024002019049062029014012006016002033001057009078004002010031016012003004006002003003002005025030
FEATURE [Part::MultiFuse] Fusion004002009002027014004009002002008002004029002015013017006002012002031033002013006007008014029072011018024002019049062029014012006016002033001057009078004002010031016012003004006002003003002005025031  label="Fusion"
  Refine = true
  Shapes = -> [Cylinder1492346,Cylinder1492345]
FEATURE [Part::Cut] Cut176013009033007019019008010045003002004008006010017027003005053020098001031003007007002011005005004026009004013005002003006024015007003005  label="Cut"
  Base = -> Cut176013009033007019019008010045003002004008006010017027003005053020098001031003007007002011005005004026009004013005002003006024015007003004
  Refine = true
  Tool = -> Fusion004002009002027014004009002002008002004029002015013017006002012002031033002013006007008014029072011018024002019049062029014012006016002033001057009078004002010031016012003004006002003003002005025031
FEATURE [Part::Cut] Cut176013009033007019019008010045003002004008006010017027003005053020098001031003007007002011005005004026009004013005002003006024015007003006  label="Cut"
  Base = -> Cut176013009033007019019008010045003002004008006010017027003005053020098001031003007007002011005005004026009004013005002003006024015007003005
  Refine = true
  Tool = -> Cylinder1492344
FEATURE [Part::Cut] Cut176013009033007019019008010045003002004008006010017027003005053020098001031003007007002011005005004026009004013005002003006024015007003007  label="Cut"
  Base = -> Cut176013009033007019019008010045003002004008006010017027003005053020098001031003007007002011005005004026009004013005002003006024015007003006
  Refine = true
  Tool = -> Fillet125007020032060003
FEATURE [Part::MultiFuse] Fusion004002009002027014004009002002008002004029002015013017006002012002031033002013006007008014029072011018024002019049062029014012006016002033001057009078004002010031016012003004006002003003002005025032  label="Fusion"
  Placement = pos=(18,0,0) rot=(0,0,1;0rad)
  Refine = true
  Shapes = -> [Cylinder1492348,Cylinder1492347]
FEATURE [Part::Cut] Cut176013009033007019019008010045003002004008006010017027003005053020098001031003007007002011005005004026009004013005002003006024015007003002  label="Cut"
  Base = -> Fusion004002009002027014004009002002008002004029002015013017006002012002031033002013006007008014029072011018024002019049062029014012006016002033001057009078004002010031016012003004006002003003002005025029
  Refine = true
  Tool = -> Fusion004002009002027014004009002002008002004029002015013017006002012002031033002013006007008014029072011018024002019049062029014012006016002033001057009078004002010031016012003004006002003003002005025032
FEATURE [Part::Chamfer] Chamfer039025078004051
  Base = -> Cut176013009033007019019008010045003002004008006010017027003005053020098001031003007007002011005005004026009004013005002003006024015007003002
  Edges = 2 edges r=2: [Edge47,Edge50]
FEATURE [Part::Fillet] Fillet125007020032060002
  Base = -> Chamfer039025078004051
  Edges = 1 edges r=1.5: [Edge25]
FEATURE [Part::Fillet] Fillet125007020032060004
  Base = -> Fillet125007020032060002
  Edges = 2 edges r=6: [Edge51,Edge66]
FEATURE [Part::Fillet] Fillet125007020032060005
  Base = -> Fillet125007020032060004
  Edges = 1 edges r=2: [Edge2]
FEATURE [Part::MultiFuse] Fusion004002009002027014004009002002008002004029002015013017006002012002031033002013006007008014029072011018024002019049062029014012006016002033001057009078004002010031016012003004006002003003002005025033  label="Fusion"
  Placement = pos=(18,0,-3) rot=(0,0,1;0rad)
  Refine = true
  Shapes = -> [Cylinder1492350,Cylinder1492349]
FEATURE [Part::MultiFuse] Fusion004002009002027014004009002002008002004029002015013017006002012002031033002013006007008014029072011018024002019049062029014012006016002033001057009078004002010031016012003004006002003003002005025034  label="Fusion"
  Placement = pos=(18,0,0) rot=(0,0,1;0rad)
  Refine = true
  Shapes = -> [Cylinder1492352,Cylinder1492351]
FEATURE [Part::Cut] Cut176013009033007019019008010045003002004008006010017027003005053020098001031003007007002011005005004026009004013005002003006024015007003003  label="diff-front-lock-servo-mount"
  Base = -> Fillet125007020032060005
  Refine = true
  Tool = -> Fusion004002009002027014004009002002008002004029002015013017006002012002031033002013006007008014029072011018024002019049062029014012006016002033001057009078004002010031016012003004006002003003002005025034
FEATURE [Part::Feature] Cut176013009033007019019008010045003002004008006010017027003005053020098001031003007007002011005005004026009004013005002003006024015007003003001  label="diff-front-lock-servo-mount"
  shape: bbox 16.5 x 38 x 12 mm, 32 faces (baked)
FEATURE [Part::Box] Box812  label="Cube"
  AttacherType = Attacher::AttachEngine3D
  Height = 12
  Length = 2
  Placement = pos=(277.5,-25,86) rot=(0,0,1;0rad)
  Width = 40
FEATURE [Part::Cut] Cut176013009033007019019008010045003002004008006010017027003005053020098001031003007007002011005005004026009004013005002003006024015007003003002  label="diff-front-lock-servo-mount-HITEC"
  Base = -> Cut176013009033007019019008010045003002004008006010017027003005053020098001031003007007002011005005004026009004013005002003006024015007003003001
  Refine = true
  Tool = -> Box812
FEATURE [App::DocumentObjectGroup] Group016  label="Miscellaneus"
  Group = -> [Fusion041,Fusion088026007031024007008004058,Compound001,Cut176013009033007019019008010045003002004008006021005004004004004002012033009,Cylinder964,Fusion088026007031024007008004100051055007010008005020,Compound003002,Cut176013009033007019019008010045003002004008006021005004004004004002012018001,Cut176013009033007019019008010045003002004008006021005004004004004002012033009016002012007022002,+8 more]
FEATURE [App::DocumentObjectGroup] Group001  label="Parts"
  Group = -> [Group013,Group014,Group015,Group016,Group017,Group018,Group023]
FEATURE [Part::Box] Box813  label="Cube"
  AttacherType = Attacher::AttachEngine3D
  Height = 8
  Length = 4.5
  Placement = pos=(267,-9,78) rot=(0,0,1;0rad)
  Width = 15
FEATURE [Part::MultiFuse] Fusion004002009002027014004009002002008002004029002015013017006002012002031033002013006007008014029072011018024002019049062029014012006016002033001057009078004002010031016012003004006002003003002005025035  label="Fusion"
  Refine = true
  Shapes = -> [Box813,Box805]
FEATURE [Part::Cut] Cut176013009033007019019008010045003002004008006010017027003005053020098001031003007007002011005005004026009004013005002003006024015007003003003  label="Cut"
  Base = -> Cut176013009033007019019008010045003002004008006010017027003005053020098001031003007007002011005005004026009004013005002003006024015007003007
  Refine = true
  Tool = -> Fusion004002009002027014004009002002008002004029002015013017006002012002031033002013006007008014029072011018024002019049062029014012006016002033001057009078004002010031016012003004006002003003002005025035
FEATURE [Part::Cut] Cut176013009033007019019008010045003002004008006010017027003005053020098001031003007007002011005005004026009004013005002003006024015007003003004  label="diff-front-top"
  Base = -> Cut176013009033007019019008010045003002004008006010017027003005053020098001031003007007002011005005004026009004013005002003006024015007003003003
  Refine = true
  Tool = -> Fusion004002009002027014004009002002008002004029002015013017006002012002031033002013006007008014029072011018024002019049062029014012006016002033001057009078004002010031016012003004006002003003002005025033
FEATURE [App::DocumentObjectGroup] Group009  label="Front Axle"
  Group = -> [Group010,Group021,Group019,Cut176013009033007019019008010045003002004008006021005004004004004002012033009016002012007022024053,Cut176013009033007019019008010045003002004008006021005004004004004002012033009016002012007022024058,Part__Mirroring007002003002018002002002005004004002003004003003002,Cut176013009033007019019008010045003002004008006021005004004004004002012033009016002012007022019,+14 more]
